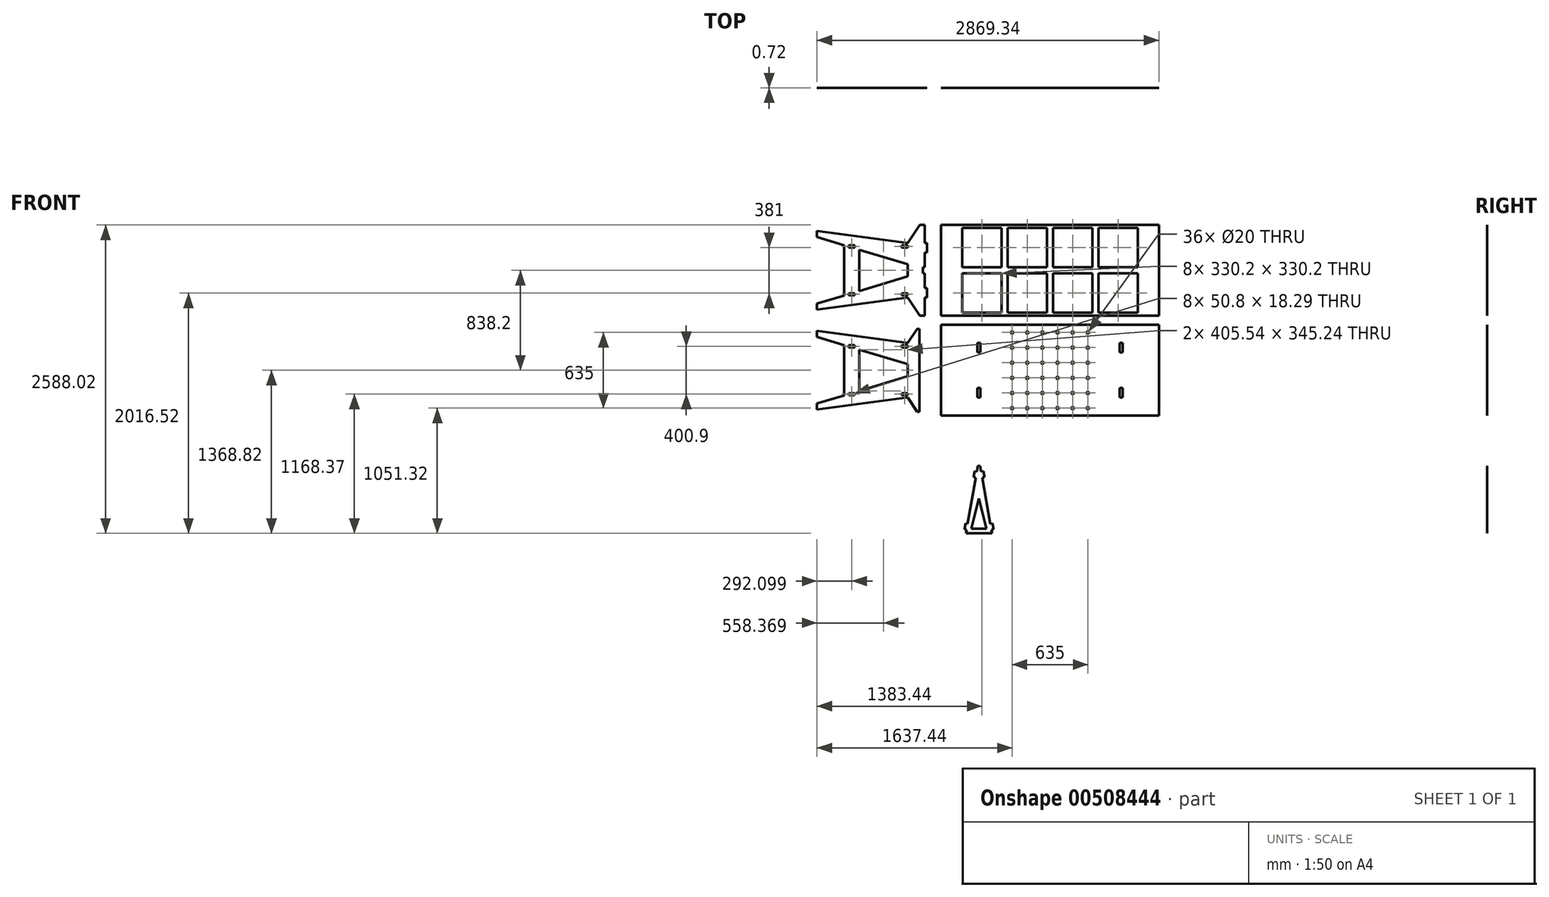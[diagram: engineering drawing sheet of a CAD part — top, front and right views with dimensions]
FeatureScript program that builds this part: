
annotation { "Feature Type Name" : "Feature", "Feature Type Description" : "" }
export const myFeature = defineFeature(function(context is Context, id is Id, definition is map)
    precondition{}
    {
        {
            assignVariable(context, id + "F0", {"name" : "ply34", "anyValue" : .72});
        }
        {
            var Q0;
            Q0=qCreatedBy(makeId("Front.planeOp"),FACE);
            var sketch = newSketch(context, id + "F1", { "sketchPlane" : qUnion([Q0])});
            skLineSegment(sketch, "E0.bottom", {"start": v(558.8, 1143) * mm, "end": v(2387.6, 1143) * mm});
            skLineSegment(sketch, "E0.top", {"start": v(558.8, 1905) * mm, "end": v(2387.6, 1905) * mm});
            skLineSegment(sketch, "E0.left", {"start": v(558.8, 1143) * mm, "end": v(558.8, 1905) * mm});
            skLineSegment(sketch, "E0.right", {"start": v(2387.6, 1143) * mm, "end": v(2387.6, 1905) * mm});
            skLineSegment(sketch, "E1.bottom", {"start": v(863.6, 1295.36) * mm, "end": v(888.66, 1295.36) * mm});
            skLineSegment(sketch, "E1.top", {"start": v(863.6, 1374.73) * mm, "end": v(888.66, 1374.73) * mm});
            skLineSegment(sketch, "E1.left", {"start": v(863.6, 1295.36) * mm, "end": v(863.6, 1374.73) * mm});
            skLineSegment(sketch, "E1.right", {"start": v(888.66, 1295.36) * mm, "end": v(888.66, 1374.73) * mm});
            skLineSegment(sketch, "E2", {"start": v(876.13, 1295.36) * mm, "end": v(876.13, 1143) * mm, "construction": true});
            skLineSegment(sketch, "E3", {"start": v(558.8, 1524) * mm, "end": v(2387.6, 1524) * mm, "construction": true});
            skLineSegment(sketch, "E4", {"start": v(2387.6, 1524) * mm, "end": v(1473.2, 1143) * mm, "construction": true});
            skLineSegment(sketch, "E5", {"start": v(1473.2, 1143) * mm, "end": v(1473.2, 1905) * mm, "construction": true});
            skLineSegment(sketch, "E6.MirrorCS", {"start": v(863.6, 1752.64) * mm, "end": v(863.6, 1673.27) * mm});
            skLineSegment(sketch, "E7.MirrorCS", {"start": v(863.6, 1673.27) * mm, "end": v(888.66, 1673.27) * mm});
            skLineSegment(sketch, "E8.MirrorCS", {"start": v(888.66, 1752.64) * mm, "end": v(888.66, 1673.27) * mm});
            skLineSegment(sketch, "E9.MirrorCS", {"start": v(863.6, 1752.64) * mm, "end": v(888.66, 1752.64) * mm});
            skLineSegment(sketch, "E10.MirrorCS", {"start": v(2082.8, 1752.64) * mm, "end": v(2082.8, 1673.27) * mm});
            skLineSegment(sketch, "E11.MirrorCS", {"start": v(2082.8, 1752.64) * mm, "end": v(2057.74, 1752.64) * mm});
            skLineSegment(sketch, "E12.MirrorCS", {"start": v(2057.74, 1752.64) * mm, "end": v(2057.74, 1673.27) * mm});
            skLineSegment(sketch, "E13.MirrorCS", {"start": v(2082.8, 1673.27) * mm, "end": v(2057.74, 1673.27) * mm});
            skLineSegment(sketch, "E14.MirrorCS", {"start": v(2082.8, 1295.36) * mm, "end": v(2082.8, 1374.73) * mm});
            skLineSegment(sketch, "E15.MirrorCS", {"start": v(2082.8, 1374.73) * mm, "end": v(2057.74, 1374.73) * mm});
            skLineSegment(sketch, "E16.MirrorCS", {"start": v(2057.74, 1295.36) * mm, "end": v(2057.74, 1374.73) * mm});
            skLineSegment(sketch, "E17.MirrorCS", {"start": v(2082.8, 1295.36) * mm, "end": v(2057.74, 1295.36) * mm});
            skCircle(sketch, "E18", {"center": v(1536.7, 1841.5) * mm, "radius": 10 * mm});
            skCircle(sketch, "E19.0.1.0", {"center": v(1536.7, 1714.5) * mm, "radius": 10 * mm});
            skCircle(sketch, "E19.0.2.0", {"center": v(1536.7, 1587.5) * mm, "radius": 10 * mm});
            skCircle(sketch, "E19.1.0.0", {"center": v(1663.7, 1841.5) * mm, "radius": 10 * mm});
            skCircle(sketch, "E19.1.1.0", {"center": v(1663.7, 1714.5) * mm, "radius": 10 * mm});
            skCircle(sketch, "E19.1.2.0", {"center": v(1663.7, 1587.5) * mm, "radius": 10 * mm});
            skCircle(sketch, "E19.2.0.0", {"center": v(1790.7, 1841.5) * mm, "radius": 10 * mm});
            skCircle(sketch, "E19.2.1.0", {"center": v(1790.7, 1714.5) * mm, "radius": 10 * mm});
            skCircle(sketch, "E19.2.2.0", {"center": v(1790.7, 1587.5) * mm, "radius": 10 * mm});
            skLineSegment(sketch, "E19.direction1", {"start": v(1536.7, 1841.5) * mm, "end": v(1663.7, 1841.5) * mm, "construction": true});
            skLineSegment(sketch, "E19.direction2", {"start": v(1536.7, 1841.5) * mm, "end": v(1536.7, 1714.5) * mm, "construction": true});
            skCircle(sketch, "E20.MirrorC", {"center": v(1409.7, 1841.5) * mm, "radius": 10 * mm});
            skCircle(sketch, "E21.MirrorC", {"center": v(1282.7, 1841.5) * mm, "radius": 10 * mm});
            skCircle(sketch, "E22.MirrorC", {"center": v(1155.7, 1841.5) * mm, "radius": 10 * mm});
            skCircle(sketch, "E23.MirrorC", {"center": v(1409.7, 1714.5) * mm, "radius": 10 * mm});
            skCircle(sketch, "E24.MirrorC", {"center": v(1282.7, 1714.5) * mm, "radius": 10 * mm});
            skCircle(sketch, "E25.MirrorC", {"center": v(1155.7, 1714.5) * mm, "radius": 10 * mm});
            skCircle(sketch, "E26.MirrorC", {"center": v(1409.7, 1587.5) * mm, "radius": 10 * mm});
            skCircle(sketch, "E27.MirrorC", {"center": v(1282.7, 1587.5) * mm, "radius": 10 * mm});
            skCircle(sketch, "E28.MirrorC", {"center": v(1155.7, 1587.5) * mm, "radius": 10 * mm});
            skCircle(sketch, "E29.MirrorC", {"center": v(1155.7, 1460.5) * mm, "radius": 10 * mm});
            skCircle(sketch, "E30.MirrorC", {"center": v(1409.7, 1206.5) * mm, "radius": 10 * mm});
            skCircle(sketch, "E31.MirrorC", {"center": v(1282.7, 1460.5) * mm, "radius": 10 * mm});
            skCircle(sketch, "E32.MirrorC", {"center": v(1155.7, 1333.5) * mm, "radius": 10 * mm});
            skCircle(sketch, "E33.MirrorC", {"center": v(1155.7, 1206.5) * mm, "radius": 10 * mm});
            skCircle(sketch, "E34.MirrorC", {"center": v(1282.7, 1206.5) * mm, "radius": 10 * mm});
            skCircle(sketch, "E35.MirrorC", {"center": v(1282.7, 1333.5) * mm, "radius": 10 * mm});
            skCircle(sketch, "E36.MirrorC", {"center": v(1409.7, 1333.5) * mm, "radius": 10 * mm});
            skCircle(sketch, "E37.MirrorC", {"center": v(1409.7, 1460.5) * mm, "radius": 10 * mm});
            skCircle(sketch, "E38.MirrorC", {"center": v(1663.7, 1460.5) * mm, "radius": 10 * mm});
            skCircle(sketch, "E39.MirrorC", {"center": v(1663.7, 1333.5) * mm, "radius": 10 * mm});
            skCircle(sketch, "E40.MirrorC", {"center": v(1536.7, 1206.5) * mm, "radius": 10 * mm});
            skCircle(sketch, "E41.MirrorC", {"center": v(1536.7, 1460.5) * mm, "radius": 10 * mm});
            skCircle(sketch, "E42.MirrorC", {"center": v(1790.7, 1206.5) * mm, "radius": 10 * mm});
            skCircle(sketch, "E43.MirrorC", {"center": v(1663.7, 1206.5) * mm, "radius": 10 * mm});
            skCircle(sketch, "E44.MirrorC", {"center": v(1790.7, 1460.5) * mm, "radius": 10 * mm});
            skCircle(sketch, "E45.MirrorC", {"center": v(1536.7, 1333.5) * mm, "radius": 10 * mm});
            skCircle(sketch, "E46.MirrorC", {"center": v(1790.7, 1333.5) * mm, "radius": 10 * mm});
            skLineSegment(sketch, "E47", {"start": v(558.8, 1943.1) * mm, "end": v(762, 1943.1) * mm});
            skLineSegment(sketch, "E48.MirrorCS", {"start": v(558.8, 1981.2) * mm, "end": v(2387.6, 1981.2) * mm});
            skLineSegment(sketch, "E49.MirrorCS", {"start": v(558.8, 2743.2) * mm, "end": v(558.8, 1981.2) * mm});
            skLineSegment(sketch, "E50.MirrorCS", {"start": v(2387.6, 2743.2) * mm, "end": v(2387.6, 1981.2) * mm});
            skLineSegment(sketch, "E51.MirrorCS", {"start": v(558.8, 2743.2) * mm, "end": v(2387.6, 2743.2) * mm});
            skLineSegment(sketch, "E52.MirrorCS", {"start": v(863.6, 2511.47) * mm, "end": v(888.66, 2511.47) * mm});
            skLineSegment(sketch, "E53.MirrorCS", {"start": v(888.66, 2590.84) * mm, "end": v(888.66, 2511.47) * mm});
            skLineSegment(sketch, "E54.MirrorCS", {"start": v(863.6, 2590.84) * mm, "end": v(863.6, 2511.47) * mm});
            skLineSegment(sketch, "E55.MirrorCS", {"start": v(863.6, 2590.84) * mm, "end": v(888.66, 2590.84) * mm});
            skLineSegment(sketch, "E56.MirrorCS", {"start": v(2082.8, 2590.84) * mm, "end": v(2082.8, 2511.47) * mm});
            skLineSegment(sketch, "E57.MirrorCS", {"start": v(2082.8, 2590.84) * mm, "end": v(2057.74, 2590.84) * mm});
            skLineSegment(sketch, "E58.MirrorCS", {"start": v(2057.74, 2590.84) * mm, "end": v(2057.74, 2511.47) * mm});
            skLineSegment(sketch, "E59.MirrorCS", {"start": v(2082.8, 2511.47) * mm, "end": v(2057.74, 2511.47) * mm});
            skLineSegment(sketch, "E60.MirrorCS", {"start": v(2082.8, 2212.93) * mm, "end": v(2057.74, 2212.93) * mm});
            skLineSegment(sketch, "E61.MirrorCS", {"start": v(2082.8, 2133.56) * mm, "end": v(2057.74, 2133.56) * mm});
            skLineSegment(sketch, "E62.MirrorCS", {"start": v(2057.74, 2133.56) * mm, "end": v(2057.74, 2212.93) * mm});
            skLineSegment(sketch, "E63.MirrorCS", {"start": v(2082.8, 2133.56) * mm, "end": v(2082.8, 2212.93) * mm});
            skLineSegment(sketch, "E64.MirrorCS", {"start": v(863.6, 2133.56) * mm, "end": v(888.66, 2133.56) * mm});
            skLineSegment(sketch, "E65.MirrorCS", {"start": v(863.6, 2212.93) * mm, "end": v(888.66, 2212.93) * mm});
            skLineSegment(sketch, "E66.MirrorCS", {"start": v(863.6, 2133.56) * mm, "end": v(863.6, 2212.93) * mm});
            skLineSegment(sketch, "E67.MirrorCS", {"start": v(888.66, 2133.56) * mm, "end": v(888.66, 2212.93) * mm});
            skCircle(sketch, "E68.MirrorC", {"center": v(1282.7, 2425.7) * mm, "radius": 10 * mm});
            skCircle(sketch, "E69.MirrorC", {"center": v(1155.7, 2425.7) * mm, "radius": 10 * mm});
            skCircle(sketch, "E70.MirrorC", {"center": v(1409.7, 2298.7) * mm, "radius": 10 * mm});
            skCircle(sketch, "E71.MirrorC", {"center": v(1282.7, 2171.7) * mm, "radius": 10 * mm});
            skCircle(sketch, "E72.MirrorC", {"center": v(1155.7, 2298.7) * mm, "radius": 10 * mm});
            skCircle(sketch, "E73.MirrorC", {"center": v(1282.7, 2044.7) * mm, "radius": 10 * mm});
            skCircle(sketch, "E74.MirrorC", {"center": v(1409.7, 2425.7) * mm, "radius": 10 * mm});
            skCircle(sketch, "E75.MirrorC", {"center": v(1409.7, 2044.7) * mm, "radius": 10 * mm});
            skCircle(sketch, "E76.MirrorC", {"center": v(1155.7, 2171.7) * mm, "radius": 10 * mm});
            skCircle(sketch, "E77.MirrorC", {"center": v(1282.7, 2679.7) * mm, "radius": 10 * mm});
            skCircle(sketch, "E78.MirrorC", {"center": v(1282.7, 2552.7) * mm, "radius": 10 * mm});
            skCircle(sketch, "E79.MirrorC", {"center": v(1409.7, 2679.7) * mm, "radius": 10 * mm});
            skCircle(sketch, "E80.MirrorC", {"center": v(1155.7, 2044.7) * mm, "radius": 10 * mm});
            skCircle(sketch, "E81.MirrorC", {"center": v(1155.7, 2552.7) * mm, "radius": 10 * mm});
            skCircle(sketch, "E82.MirrorC", {"center": v(1155.7, 2679.7) * mm, "radius": 10 * mm});
            skCircle(sketch, "E83.MirrorC", {"center": v(1409.7, 2552.7) * mm, "radius": 10 * mm});
            skCircle(sketch, "E84.MirrorC", {"center": v(1282.7, 2298.7) * mm, "radius": 10 * mm});
            skCircle(sketch, "E85.MirrorC", {"center": v(1409.7, 2171.7) * mm, "radius": 10 * mm});
            skCircle(sketch, "E86.MirrorC", {"center": v(1663.7, 2679.7) * mm, "radius": 10 * mm});
            skCircle(sketch, "E87.MirrorC", {"center": v(1790.7, 2298.7) * mm, "radius": 10 * mm});
            skCircle(sketch, "E88.MirrorC", {"center": v(1536.7, 2425.7) * mm, "radius": 10 * mm});
            skCircle(sketch, "E89.MirrorC", {"center": v(1663.7, 2298.7) * mm, "radius": 10 * mm});
            skCircle(sketch, "E90.MirrorC", {"center": v(1536.7, 2298.7) * mm, "radius": 10 * mm});
            skCircle(sketch, "E91.MirrorC", {"center": v(1663.7, 2425.7) * mm, "radius": 10 * mm});
            skCircle(sketch, "E92.MirrorC", {"center": v(1790.7, 2552.7) * mm, "radius": 10 * mm});
            skCircle(sketch, "E93.MirrorC", {"center": v(1663.7, 2552.7) * mm, "radius": 10 * mm});
            skCircle(sketch, "E94.MirrorC", {"center": v(1536.7, 2679.7) * mm, "radius": 10 * mm});
            skCircle(sketch, "E95.MirrorC", {"center": v(1536.7, 2552.7) * mm, "radius": 10 * mm});
            skCircle(sketch, "E96.MirrorC", {"center": v(1790.7, 2425.7) * mm, "radius": 10 * mm});
            skCircle(sketch, "E97.MirrorC", {"center": v(1790.7, 2679.7) * mm, "radius": 10 * mm});
            skCircle(sketch, "E98.MirrorC", {"center": v(1663.7, 2171.7) * mm, "radius": 10 * mm});
            skCircle(sketch, "E99.MirrorC", {"center": v(1790.7, 2171.7) * mm, "radius": 10 * mm});
            skCircle(sketch, "E100.MirrorC", {"center": v(1790.7, 2044.7) * mm, "radius": 10 * mm});
            skCircle(sketch, "E101.MirrorC", {"center": v(1663.7, 2044.7) * mm, "radius": 10 * mm});
            skCircle(sketch, "E102.MirrorC", {"center": v(1536.7, 2044.7) * mm, "radius": 10 * mm});
            skCircle(sketch, "E103.MirrorC", {"center": v(1536.7, 2171.7) * mm, "radius": 10 * mm});
            skPoint(sketch, "E104.positionSnap0", {"position": v(2387.6, 2362.2) * mm});
            skLineSegment(sketch, "E105", {"start": v(1536.7, 2552.7) * mm, "end": v(1663.7, 2552.7) * mm, "construction": true});
            skLineSegment(sketch, "E106", {"start": v(1663.7, 2425.7) * mm, "end": v(1663.7, 2552.7) * mm, "construction": true});
            skPoint(sketch, "E107.startSnap0", {"position": v(1600.2, 2552.7) * mm});
            skPoint(sketch, "E108.startSnap0", {"position": v(1663.7, 2489.2) * mm});
            skLineSegment(sketch, "E109", {"start": v(1473.2, 2743.2) * mm, "end": v(1473.2, 1981.2) * mm, "construction": true});
            skLineSegment(sketch, "E110", {"start": v(558.8, 2362.2) * mm, "end": v(2387.6, 2362.2) * mm, "construction": true});
            skLineSegment(sketch, "E111.bottom", {"start": v(1447.8, 2387.6) * mm, "end": v(1117.6, 2387.6) * mm});
            skLineSegment(sketch, "E111.top", {"start": v(1447.8, 2717.8) * mm, "end": v(1117.6, 2717.8) * mm});
            skLineSegment(sketch, "E111.left", {"start": v(1447.8, 2387.6) * mm, "end": v(1447.8, 2717.8) * mm});
            skLineSegment(sketch, "E111.right", {"start": v(1117.6, 2387.6) * mm, "end": v(1117.6, 2717.8) * mm});
            skLineSegment(sketch, "E112", {"start": v(1282.7, 2717.8) * mm, "end": v(1282.7, 2387.6) * mm, "construction": true});
            skLineSegment(sketch, "E113.MirrorCS", {"start": v(1498.6, 2387.6) * mm, "end": v(1498.6, 2717.8) * mm});
            skLineSegment(sketch, "E114.MirrorCS", {"start": v(1498.6, 2717.8) * mm, "end": v(1828.8, 2717.8) * mm});
            skLineSegment(sketch, "E115.MirrorCS", {"start": v(1828.8, 2387.6) * mm, "end": v(1828.8, 2717.8) * mm});
            skLineSegment(sketch, "E116.MirrorCS", {"start": v(1498.6, 2387.6) * mm, "end": v(1828.8, 2387.6) * mm});
            skLineSegment(sketch, "E117.MirrorCS", {"start": v(1663.7, 2717.8) * mm, "end": v(1663.7, 2387.6) * mm, "construction": true});
            skLineSegment(sketch, "E118.MirrorCS", {"start": v(1066.8, 2387.6) * mm, "end": v(1066.8, 2717.8) * mm});
            skLineSegment(sketch, "E119.MirrorCS", {"start": v(1066.8, 2717.8) * mm, "end": v(736.6, 2717.8) * mm});
            skLineSegment(sketch, "E120.MirrorCS", {"start": v(736.6, 2387.6) * mm, "end": v(736.6, 2717.8) * mm});
            skLineSegment(sketch, "E121.MirrorCS", {"start": v(1066.8, 2387.6) * mm, "end": v(736.6, 2387.6) * mm});
            skLineSegment(sketch, "E122.MirrorCS", {"start": v(1879.6, 2717.8) * mm, "end": v(2209.8, 2717.8) * mm});
            skLineSegment(sketch, "E123.MirrorCS", {"start": v(2209.8, 2387.6) * mm, "end": v(2209.8, 2717.8) * mm});
            skLineSegment(sketch, "E124.MirrorCS", {"start": v(1879.6, 2387.6) * mm, "end": v(2209.8, 2387.6) * mm});
            skLineSegment(sketch, "E125.MirrorCS", {"start": v(1879.6, 2387.6) * mm, "end": v(1879.6, 2717.8) * mm});
            skLineSegment(sketch, "E126.MirrorCS", {"start": v(1879.6, 2006.6) * mm, "end": v(2209.8, 2006.6) * mm});
            skLineSegment(sketch, "E127.MirrorCS", {"start": v(1498.6, 2006.6) * mm, "end": v(1828.8, 2006.6) * mm});
            skLineSegment(sketch, "E128.MirrorCS", {"start": v(1066.8, 2006.6) * mm, "end": v(736.6, 2006.6) * mm});
            skLineSegment(sketch, "E129.MirrorCS", {"start": v(1447.8, 2006.6) * mm, "end": v(1117.6, 2006.6) * mm});
            skLineSegment(sketch, "E130.MirrorCS", {"start": v(1066.8, 2336.8) * mm, "end": v(736.6, 2336.8) * mm});
            skLineSegment(sketch, "E131.MirrorCS", {"start": v(1879.6, 2336.8) * mm, "end": v(2209.8, 2336.8) * mm});
            skLineSegment(sketch, "E132.MirrorCS", {"start": v(1447.8, 2336.8) * mm, "end": v(1117.6, 2336.8) * mm});
            skLineSegment(sketch, "E133.MirrorCS", {"start": v(1498.6, 2336.8) * mm, "end": v(1828.8, 2336.8) * mm});
            skLineSegment(sketch, "E134.MirrorCS", {"start": v(2209.8, 2336.8) * mm, "end": v(2209.8, 2006.6) * mm});
            skLineSegment(sketch, "E135.MirrorCS", {"start": v(1828.8, 2336.8) * mm, "end": v(1828.8, 2006.6) * mm});
            skLineSegment(sketch, "E136.MirrorCS", {"start": v(1879.6, 2336.8) * mm, "end": v(1879.6, 2006.6) * mm});
            skLineSegment(sketch, "E137.MirrorCS", {"start": v(1498.6, 2336.8) * mm, "end": v(1498.6, 2006.6) * mm});
            skLineSegment(sketch, "E138.MirrorCS", {"start": v(1447.8, 2336.8) * mm, "end": v(1447.8, 2006.6) * mm});
            skLineSegment(sketch, "E139.MirrorCS", {"start": v(736.6, 2336.8) * mm, "end": v(736.6, 2006.6) * mm});
            skLineSegment(sketch, "E140.MirrorCS", {"start": v(1117.6, 2336.8) * mm, "end": v(1117.6, 2006.6) * mm});
            skLineSegment(sketch, "E141.MirrorCS", {"start": v(1066.8, 2336.8) * mm, "end": v(1066.8, 2006.6) * mm});
            skLineSegment(sketch, "E142.bottom", {"start": v(441.96, 2590.84) * mm, "end": v(406.4, 2590.84) * mm});
            skLineSegment(sketch, "E142.top", {"start": v(441.96, 2511.47) * mm, "end": v(406.4, 2511.47) * mm});
            skLineSegment(sketch, "E142.left", {"start": v(441.96, 2590.84) * mm, "end": v(441.96, 2511.47) * mm});
            skLineSegment(sketch, "E142.right", {"start": v(406.4, 2590.84) * mm, "end": v(406.4, 2511.47) * mm});
            skLineSegment(sketch, "E143.bottom", {"start": v(441.96, 2212.93) * mm, "end": v(406.4, 2212.93) * mm});
            skLineSegment(sketch, "E143.top", {"start": v(441.96, 2133.56) * mm, "end": v(406.4, 2133.56) * mm});
            skLineSegment(sketch, "E143.left", {"start": v(441.96, 2212.93) * mm, "end": v(441.96, 2133.56) * mm});
            skLineSegment(sketch, "E143.right", {"start": v(406.4, 2212.93) * mm, "end": v(406.4, 2133.56) * mm});
            skLineSegment(sketch, "E144", {"start": v(406.4, 2743.2) * mm, "end": v(406.4, 1981.2) * mm});
            skLineSegment(sketch, "E145", {"start": v(406.4, 1981.2) * mm, "end": v(381, 1981.2) * mm});
            skLineSegment(sketch, "E146", {"start": v(381, 1981.2) * mm, "end": v(279.4, 2133.56) * mm});
            skLineSegment(sketch, "E147", {"start": v(279.4, 2133.56) * mm, "end": v(-481.74, 2032) * mm});
            skLineSegment(sketch, "E148", {"start": v(558.8, 838.2) * mm, "end": v(2387.6, 838.2) * mm});
            skLineSegment(sketch, "E149", {"start": v(558.8, 838.2) * mm, "end": v(558.8, 801.62) * mm});
            skLineSegment(sketch, "E150", {"start": v(558.8, 801.62) * mm, "end": v(2387.6, 801.62) * mm});
            skLineSegment(sketch, "E151", {"start": v(2387.6, 801.62) * mm, "end": v(2387.6, 838.2) * mm});
            skLineSegment(sketch, "E152", {"start": v(863.6, 838.2) * mm, "end": v(863.6, 801.62) * mm});
            skLineSegment(sketch, "E153", {"start": v(888.66, 838.2) * mm, "end": v(888.66, 801.62) * mm});
            skLineSegment(sketch, "E154", {"start": v(863.6, 801.62) * mm, "end": v(869.77, 836.64) * mm});
            skLineSegment(sketch, "E155", {"start": v(869.77, 836.64) * mm, "end": v(887.79, 833.47) * mm});
            skLineSegment(sketch, "E156", {"start": v(887.79, 833.47) * mm, "end": v(727.39, -76.2) * mm});
            skLineSegment(sketch, "E157", {"start": v(441.96, 2362.2) * mm, "end": v(-481.74, 2362.2) * mm, "construction": true});
            skPoint(sketch, "E157.startSnap0", {"position": v(406.4, 2362.2) * mm});
            skPoint(sketch, "E157.endSnap0", {"position": v(406.4, 2362.2) * mm});
            skLineSegment(sketch, "E158", {"start": v(-481.74, 2032) * mm, "end": v(-481.74, 2082.8) * mm});
            skLineSegment(sketch, "E159", {"start": v(-481.74, 2082.8) * mm, "end": v(279.4, 2311.36) * mm, "construction": true});
            skLineSegment(sketch, "E160", {"start": v(-481.74, 2082.8) * mm, "end": v(-253.14, 2151.44) * mm});
            skLineSegment(sketch, "E161", {"start": v(-253.14, 2151.44) * mm, "end": v(-253.14, 2362.2) * mm});
            skLineSegment(sketch, "E162", {"start": v(-126.14, 2189.58) * mm, "end": v(-126.14, 2362.2) * mm});
            skLineSegment(sketch, "E163", {"start": v(279.4, 2311.36) * mm, "end": v(279.4, 2362.2) * mm});
            skLineSegment(sketch, "E164", {"start": v(-126.14, 2189.58) * mm, "end": v(279.4, 2311.36) * mm});
            skLineSegment(sketch, "E165.MirrorCS", {"start": v(-126.14, 2534.82) * mm, "end": v(-126.14, 2362.2) * mm});
            skLineSegment(sketch, "E166.MirrorCS", {"start": v(-253.14, 2572.96) * mm, "end": v(-253.14, 2362.2) * mm});
            skLineSegment(sketch, "E167.MirrorCS", {"start": v(-481.74, 2641.6) * mm, "end": v(-253.14, 2572.96) * mm});
            skLineSegment(sketch, "E168.MirrorCS", {"start": v(-481.74, 2692.4) * mm, "end": v(-481.74, 2641.6) * mm});
            skLineSegment(sketch, "E169.MirrorCS", {"start": v(279.4, 2413.04) * mm, "end": v(279.4, 2362.2) * mm});
            skLineSegment(sketch, "E170.MirrorCS", {"start": v(-126.14, 2534.82) * mm, "end": v(279.4, 2413.04) * mm});
            skLineSegment(sketch, "E171.MirrorCS", {"start": v(279.4, 2590.84) * mm, "end": v(-481.74, 2692.4) * mm});
            skLineSegment(sketch, "E172.MirrorCS", {"start": v(381, 2743.2) * mm, "end": v(279.4, 2590.84) * mm});
            skLineSegment(sketch, "E173.MirrorCS", {"start": v(406.4, 2743.2) * mm, "end": v(381, 2743.2) * mm});
            skLineSegment(sketch, "E174.bottom", {"start": v(279.4, 2170.9) * mm, "end": v(228.6, 2170.9) * mm});
            skLineSegment(sketch, "E174.top", {"start": v(279.4, 2152.6) * mm, "end": v(228.6, 2152.6) * mm});
            skLineSegment(sketch, "E174.left", {"start": v(279.4, 2170.9) * mm, "end": v(279.4, 2152.6) * mm});
            skLineSegment(sketch, "E174.right", {"start": v(228.6, 2170.9) * mm, "end": v(228.6, 2152.6) * mm});
            skLineSegment(sketch, "E175.bottom", {"start": v(-164.24, 2170.9) * mm, "end": v(-215.04, 2170.9) * mm});
            skLineSegment(sketch, "E175.top", {"start": v(-164.24, 2152.6) * mm, "end": v(-215.04, 2152.6) * mm});
            skLineSegment(sketch, "E175.left", {"start": v(-164.24, 2170.9) * mm, "end": v(-164.24, 2152.6) * mm});
            skLineSegment(sketch, "E175.right", {"start": v(-215.04, 2170.9) * mm, "end": v(-215.04, 2152.6) * mm});
            skLineSegment(sketch, "E176", {"start": v(-253.14, 2362.2) * mm, "end": v(-126.14, 2362.2) * mm, "construction": true});
            skPoint(sketch, "E177", {"position": v(-189.64, 2362.2) * mm});
            skPoint(sketch, "E178", {"position": v(-189.64, 2170.9) * mm});
            skLineSegment(sketch, "E179", {"start": v(279.4, 2161.75) * mm, "end": v(441.96, 2161.75) * mm, "construction": true});
            skLineSegment(sketch, "E180", {"start": v(-164.24, 2161.75) * mm, "end": v(441.96, 2161.75) * mm, "construction": true});
            skLineSegment(sketch, "E181", {"start": v(878.78, 835.06) * mm, "end": v(850.55, 674.97) * mm, "construction": true});
            skLineSegment(sketch, "E182", {"start": v(878.78, 835.06) * mm, "end": v(773.51, 238.06) * mm, "construction": true});
            skLineSegment(sketch, "E183", {"start": v(773.51, 238.06) * mm, "end": v(782.52, 236.48) * mm});
            skLineSegment(sketch, "E184", {"start": v(850.55, 674.97) * mm, "end": v(859.56, 673.38) * mm});
            skLineSegment(sketch, "E185", {"start": v(877.7, 776.22) * mm, "end": v(1028, -76.2) * mm});
            skLineSegment(sketch, "E186", {"start": v(877.7, 776.22) * mm, "end": v(895.7, 779.4) * mm});
            skLineSegment(sketch, "E187", {"start": v(782.52, 236.48) * mm, "end": v(764.5, 239.65) * mm});
            skLineSegment(sketch, "E188", {"start": v(764.5, 239.65) * mm, "end": v(755.69, 189.62) * mm});
            skLineSegment(sketch, "E189", {"start": v(755.69, 189.62) * mm, "end": v(773.7, 186.45) * mm});
            skLineSegment(sketch, "E190", {"start": v(859.56, 673.38) * mm, "end": v(841.55, 676.55) * mm});
            skLineSegment(sketch, "E191", {"start": v(841.55, 676.55) * mm, "end": v(832.73, 626.53) * mm});
            skLineSegment(sketch, "E192", {"start": v(832.73, 626.53) * mm, "end": v(850.74, 623.35) * mm});
            skLineSegment(sketch, "E193", {"start": v(868.17, 722.2) * mm, "end": v(887.22, 722.2) * mm});
            skLineSegment(sketch, "E194", {"start": v(877.7, 722.2) * mm, "end": v(877.7, 776.22) * mm, "construction": true});
            skLineSegment(sketch, "E195", {"start": v(768.18, 155.18) * mm, "end": v(987.2, 155.18) * mm});
            skLineSegment(sketch, "E196", {"start": v(814.2, 193.28) * mm, "end": v(941.2, 193.28) * mm});
            skPoint(sketch, "E197", {"position": v(877.7, 193.28) * mm});
            skLineSegment(sketch, "E198", {"start": v(814.2, 193.28) * mm, "end": v(877.7, 447.28) * mm});
            skLineSegment(sketch, "E199", {"start": v(877.7, 447.28) * mm, "end": v(941.2, 193.28) * mm});
            skLineSegment(sketch, "E200.MirrorCS", {"start": v(895.83, 673.38) * mm, "end": v(913.84, 676.55) * mm});
            skLineSegment(sketch, "E201.MirrorCS", {"start": v(913.84, 676.55) * mm, "end": v(922.66, 626.53) * mm});
            skLineSegment(sketch, "E202.MirrorCS", {"start": v(922.66, 626.53) * mm, "end": v(904.65, 623.35) * mm});
            skLineSegment(sketch, "E203.MirrorCS", {"start": v(999.7, 189.62) * mm, "end": v(981.68, 186.45) * mm});
            skLineSegment(sketch, "E204.MirrorCS", {"start": v(990.87, 239.65) * mm, "end": v(999.7, 189.62) * mm});
            skLineSegment(sketch, "E205.MirrorCS", {"start": v(972.86, 236.48) * mm, "end": v(990.87, 239.65) * mm});
            skLineSegment(sketch, "E206.MirrorCS", {"start": v(228.6, 2553.5) * mm, "end": v(228.6, 2571.8) * mm});
            skLineSegment(sketch, "E207.MirrorCS", {"start": v(279.4, 2553.5) * mm, "end": v(279.4, 2571.8) * mm});
            skLineSegment(sketch, "E208.MirrorCS", {"start": v(279.4, 2553.5) * mm, "end": v(228.6, 2553.5) * mm});
            skLineSegment(sketch, "E209.MirrorCS", {"start": v(279.4, 2571.8) * mm, "end": v(228.6, 2571.8) * mm});
            skPoint(sketch, "E210.MirrorP", {"position": v(-189.64, 2553.5) * mm});
            skLineSegment(sketch, "E211.MirrorCS", {"start": v(-164.24, 2571.8) * mm, "end": v(-215.04, 2571.8) * mm});
            skLineSegment(sketch, "E212.MirrorCS", {"start": v(-215.04, 2553.5) * mm, "end": v(-215.04, 2571.8) * mm});
            skLineSegment(sketch, "E213.MirrorCS", {"start": v(-164.24, 2553.5) * mm, "end": v(-215.04, 2553.5) * mm});
            skLineSegment(sketch, "E214.MirrorCS", {"start": v(-164.24, 2553.5) * mm, "end": v(-164.24, 2571.8) * mm});
            skLineSegment(sketch, "E215.MirrorCS", {"start": v(279.4, 1715.3) * mm, "end": v(279.4, 1733.6) * mm});
            skLineSegment(sketch, "E216.MirrorCS", {"start": v(279.4, 1332.7) * mm, "end": v(279.4, 1314.4) * mm});
            skLineSegment(sketch, "E217.MirrorCS", {"start": v(-164.24, 1715.3) * mm, "end": v(-215.04, 1715.3) * mm});
            skLineSegment(sketch, "E218.MirrorCS", {"start": v(-215.04, 1715.3) * mm, "end": v(-215.04, 1733.6) * mm});
            skLineSegment(sketch, "E219.MirrorCS", {"start": v(-164.24, 1733.6) * mm, "end": v(-215.04, 1733.6) * mm});
            skLineSegment(sketch, "E220.MirrorCS", {"start": v(-164.24, 1715.3) * mm, "end": v(-164.24, 1733.6) * mm});
            skLineSegment(sketch, "E221.MirrorCS", {"start": v(383.83, 1905) * mm, "end": v(381, 1905) * mm});
            skLineSegment(sketch, "E222.MirrorCS", {"start": v(228.6, 1332.7) * mm, "end": v(228.6, 1314.4) * mm});
            skLineSegment(sketch, "E223.MirrorCS", {"start": v(228.6, 1715.3) * mm, "end": v(228.6, 1733.6) * mm});
            skLineSegment(sketch, "E224.MirrorCS", {"start": v(279.4, 1332.7) * mm, "end": v(228.6, 1332.7) * mm});
            skLineSegment(sketch, "E225.MirrorCS", {"start": v(279.4, 1314.4) * mm, "end": v(228.6, 1314.4) * mm});
            skLineSegment(sketch, "E226.MirrorCS", {"start": v(-164.24, 1314.4) * mm, "end": v(-215.04, 1314.4) * mm});
            skLineSegment(sketch, "E227.MirrorCS", {"start": v(-481.74, 1193.8) * mm, "end": v(-481.74, 1244.6) * mm});
            skLineSegment(sketch, "E228.MirrorCS", {"start": v(-164.24, 1332.7) * mm, "end": v(-215.04, 1332.7) * mm});
            skLineSegment(sketch, "E229.MirrorCS", {"start": v(-215.04, 1332.7) * mm, "end": v(-215.04, 1314.4) * mm});
            skLineSegment(sketch, "E230.MirrorCS", {"start": v(279.4, 1473.16) * mm, "end": v(279.4, 1524) * mm});
            skLineSegment(sketch, "E231.MirrorCS", {"start": v(-164.24, 1332.7) * mm, "end": v(-164.24, 1314.4) * mm});
            skLineSegment(sketch, "E232.MirrorCS", {"start": v(383.83, 1143) * mm, "end": v(381, 1143) * mm});
            skLineSegment(sketch, "E233.MirrorCS", {"start": v(-481.74, 1854.2) * mm, "end": v(-481.74, 1803.4) * mm});
            skLineSegment(sketch, "E234.MirrorCS", {"start": v(279.4, 1715.3) * mm, "end": v(228.6, 1715.3) * mm});
            skLineSegment(sketch, "E235.MirrorCS", {"start": v(279.4, 1733.6) * mm, "end": v(228.6, 1733.6) * mm});
            skLineSegment(sketch, "E236.MirrorCS", {"start": v(279.4, 1574.84) * mm, "end": v(279.4, 1524) * mm});
            skLineSegment(sketch, "E237.MirrorCS", {"start": v(-481.74, 1803.4) * mm, "end": v(-253.14, 1734.76) * mm});
            skLineSegment(sketch, "E238.MirrorCS", {"start": v(-253.14, 1524) * mm, "end": v(-126.14, 1524) * mm, "construction": true});
            skLineSegment(sketch, "E239.MirrorCS", {"start": v(-126.14, 1696.62) * mm, "end": v(279.4, 1574.84) * mm});
            skLineSegment(sketch, "E240.MirrorCS", {"start": v(-126.14, 1351.38) * mm, "end": v(-126.14, 1524) * mm});
            skLineSegment(sketch, "E241.MirrorCS", {"start": v(-253.14, 1734.76) * mm, "end": v(-253.14, 1524) * mm});
            skLineSegment(sketch, "E242.MirrorCS", {"start": v(279.4, 1752.64) * mm, "end": v(-481.74, 1854.2) * mm});
            skLineSegment(sketch, "E243.MirrorCS", {"start": v(-253.14, 1313.24) * mm, "end": v(-253.14, 1524) * mm});
            skPoint(sketch, "E244.MirrorP", {"position": v(-189.64, 1715.3) * mm});
            skLineSegment(sketch, "E245.MirrorCS", {"start": v(-481.74, 1244.6) * mm, "end": v(-253.14, 1313.24) * mm});
            skPoint(sketch, "E246.MirrorP", {"position": v(-189.64, 1524) * mm});
            skPoint(sketch, "E247.MirrorP", {"position": v(-189.64, 1332.7) * mm});
            skLineSegment(sketch, "E248.MirrorCS", {"start": v(-126.14, 1351.38) * mm, "end": v(279.4, 1473.16) * mm});
            skLineSegment(sketch, "E249.MirrorCS", {"start": v(358.43, 1176.84) * mm, "end": v(279.4, 1295.36) * mm});
            skLineSegment(sketch, "E250.MirrorCS", {"start": v(-481.74, 1803.4) * mm, "end": v(279.4, 1574.84) * mm, "construction": true});
            skLineSegment(sketch, "E251.MirrorCS", {"start": v(-126.14, 1696.62) * mm, "end": v(-126.14, 1524) * mm});
            skLineSegment(sketch, "E252.MirrorCS", {"start": v(358.43, 1871.16) * mm, "end": v(279.4, 1752.64) * mm});
            skLineSegment(sketch, "E253.MirrorCS", {"start": v(279.4, 1295.36) * mm, "end": v(-481.74, 1193.8) * mm});
            skLineSegment(sketch, "E254", {"start": v(-481.74, 1524) * mm, "end": v(383.83, 1524) * mm, "construction": true});
            skLineSegment(sketch, "E255", {"start": v(383.83, 1176.84) * mm, "end": v(383.83, 1871.16) * mm});
            skPoint(sketch, "E256.orphan", {"position": v(406.4, 1143) * mm});
            skLineSegment(sketch, "E257", {"start": v(383.83, 1871.16) * mm, "end": v(358.43, 1871.16) * mm});
            skLineSegment(sketch, "E258", {"start": v(358.43, 1176.84) * mm, "end": v(383.83, 1176.84) * mm});
            skPoint(sketch, "E259.orphan", {"position": v(381, 1143) * mm});
            skLineSegment(sketch, "E260", {"start": v(406.4, 2743.2) * mm, "end": v(424.18, 2743.2) * mm});
            skPoint(sketch, "E260.endSnap0", {"position": v(424.18, 2590.84) * mm});
            skLineSegment(sketch, "E261", {"start": v(424.18, 2743.2) * mm, "end": v(424.18, 2590.84) * mm});
            skLineSegment(sketch, "E262", {"start": v(424.18, 2511.47) * mm, "end": v(424.18, 2212.93) * mm});
            skLineSegment(sketch, "E263", {"start": v(424.18, 2133.56) * mm, "end": v(424.18, 1981.2) * mm});
            skLineSegment(sketch, "E264", {"start": v(424.18, 1981.2) * mm, "end": v(406.4, 1981.2) * mm});
            skLineSegment(sketch, "E265.top", {"start": v(406.4, 2717.8) * mm, "end": v(424.18, 2717.8) * mm});
            skLineSegment(sketch, "E265.left", {"start": v(406.4, 2743.2) * mm, "end": v(406.4, 2717.8) * mm});
            skLineSegment(sketch, "E265.right", {"start": v(424.18, 2743.2) * mm, "end": v(424.18, 2717.8) * mm});
            skLineSegment(sketch, "E266.bottom", {"start": v(424.18, 2336.8) * mm, "end": v(406.4, 2336.8) * mm});
            skLineSegment(sketch, "E266.top", {"start": v(424.18, 2387.6) * mm, "end": v(406.4, 2387.6) * mm});
            skLineSegment(sketch, "E266.left", {"start": v(424.18, 2336.8) * mm, "end": v(424.18, 2387.6) * mm});
            skLineSegment(sketch, "E266.right", {"start": v(406.4, 2336.8) * mm, "end": v(406.4, 2387.6) * mm});
            skLineSegment(sketch, "E267.bottom", {"start": v(406.4, 2006.6) * mm, "end": v(424.18, 2006.6) * mm});
            skLineSegment(sketch, "E267.top", {"start": v(406.4, 1981.2) * mm, "end": v(424.18, 1981.2) * mm});
            skLineSegment(sketch, "E267.left", {"start": v(406.4, 2006.6) * mm, "end": v(406.4, 1981.2) * mm});
            skLineSegment(sketch, "E267.right", {"start": v(424.18, 2006.6) * mm, "end": v(424.18, 1981.2) * mm});
            skLineSegment(sketch, "E268.0", {"start": v(377.48, 1176.84) * mm, "end": v(377.48, 1871.16) * mm});
            skSolve(sketch);
        }
        {
            var Q0;
            {var subQ10=sQuery(id+"F1.wireOp",EDGE,"mAf3JBsy-TMgf-ZAlM-1Swj-JmzUZRKuhz1c");Q0=makeQuery(id+"F1.imprint","IMPRINT",FACE,{"disambiguationData":[TD([[makeQuery(id+"F1.imprint","IMPRINT",EDGE,{"derivedFrom":subQ10}),1.0]])]});}
            var Q1;
            {var subQ0=sQuery(id+"F1.wireOp",EDGE,"s7SXwr1m-1hA2-V0Zk-YU9T-9B9GOdkSBnw9");Q1=makeQuery(id+"F1.imprint","IMPRINT",FACE,{"disambiguationData":[TD([[makeQuery(id+"F1.imprint","IMPRINT",EDGE,{"derivedFrom":subQ0}),-1.0]])]});}
            var Q2;
            {var subQ0=sQuery(id+"F1.wireOp",EDGE,"N2ZZMMIE-rYt3-nwKZ-H1YN-OZv6ZI7qveUN");Q2=makeQuery(id+"F1.imprint","IMPRINT",FACE,{"disambiguationData":[TD([[makeQuery(id+"F1.imprint","IMPRINT",EDGE,{"derivedFrom":subQ0}),1.0]])]});}
            var Q3;
            {var subQ0=sQuery(id+"F1.wireOp",EDGE,"9ebe2d56-449b-47a5-8353-0fb5eb4cb9f70.MirrorCS");Q3=makeQuery(id+"F1.imprint","IMPRINT",FACE,{"disambiguationData":[TD([[makeQuery(id+"F1.imprint","IMPRINT",EDGE,{"derivedFrom":subQ0}),-1.0]])]});}
            var Q4;
            Q4=makeQuery(id+"F1.imprint","IMPRINT",FACE,{"disambiguationData":[TD([[makeQuery(id+"F1.imprint","IMPRINT",EDGE,{"derivedFrom":sQuery(id+"F1.wireOp",EDGE,"a0fd9d23-0f2f-4645-a1b7-4233243fae940.MirrorCS")}),1.0]])]});
            var Q5;
            {var subQ26=sQuery(id+"F1.wireOp",EDGE,"oeQHpsQD-rnvI-rLyI-L1zO-BZtazGxPJs8b");Q5=makeQuery(id+"F1.imprint","IMPRINT",FACE,{"disambiguationData":[TD([[makeQuery(id+"F1.imprint","IMPRINT",EDGE,{"derivedFrom":subQ26}),1.0]])]});}
            var Q6;
            Q6=makeQuery(id+"F1.imprint","IMPRINT",FACE,{"disambiguationData":[TD([[makeQuery(id+"F1.imprint","IMPRINT",EDGE,{"derivedFrom":sQuery(id+"F1.wireOp",EDGE,"E0.bottom")}),1.0]])]});
            var Q7;
            {var subQ0=sQuery(id+"F1.wireOp",EDGE,"xvaGzj0J-OEMp-EC2P-Z3wq-kDdIABfkp5yY");Q7=makeQuery(id+"F1.imprint","IMPRINT",FACE,{"disambiguationData":[TD([[makeQuery(id+"F1.imprint","IMPRINT",EDGE,{"derivedFrom":subQ0}),1.0]])]});}
            var Q8;
            Q8=makeQuery(id+"F1.imprint","IMPRINT",FACE,{"disambiguationData":[TD([[makeQuery(id+"F1.imprint","IMPRINT",EDGE,{"derivedFrom":sQuery(id+"F1.wireOp",EDGE,"AbsmaskG-t7lV-PoPT-sEhg-hebk6gVqelMg.bottom")}),1.0]])]});
            var Q9;
            Q9=makeQuery(id+"F1.imprint","IMPRINT",FACE,{"disambiguationData":[TD([[makeQuery(id+"F1.imprint","IMPRINT",EDGE,{"derivedFrom":sQuery(id+"F1.wireOp",EDGE,"Yeb76Brc-eH3c-p8nl-VyMf-ov4TZDuTgUcc.bottom")}),-1.0]])]});
            var Q10;
            {var subQ0=sQuery(id+"F1.wireOp",EDGE,"E51.MirrorCS");var subQ1=sQuery(id+"F1.wireOp",EDGE,"E49.MirrorCS");var subQ2=makeQuery(id+"F1.imprint","INTERSECT",VERTEX,{"derivedFrom":[subQ1,subQ0]});Q10=makeQuery(id+"F1.imprint","IMPRINT",FACE,{"disambiguationData":[TD([[makeQuery(id+"F1.imprint","IMPRINT",EDGE,{"disambiguationData":[TD([[subQ2,-1.0]])],"derivedFrom":subQ1}),1.0]])]});}
            var Q11;
            {var subQ0=sQuery(id+"F1.wireOp",EDGE,"RNtuIrKz-1knl-u3FS-AxBv-elPmaKCl8baw");var subQ1=sQuery(id+"F1.wireOp",EDGE,"E51.MirrorCS");var subQ2=makeQuery(id+"F1.imprint","INTERSECT",VERTEX,{"derivedFrom":[subQ1,subQ0]});Q11=makeQuery(id+"F1.imprint","IMPRINT",FACE,{"disambiguationData":[TD([[makeQuery(id+"F1.imprint","IMPRINT",EDGE,{"disambiguationData":[TD([[subQ2,1.0]])],"derivedFrom":subQ1}),-1.0]])]});}
            var Q12;
            {var subQ0=sQuery(id+"F1.wireOp",EDGE,"7UFrm05o-hojw-SgNx-ndEl-vP84DU8JNmmf");var subQ1=sQuery(id+"F1.wireOp",EDGE,"E51.MirrorCS");var subQ2=makeQuery(id+"F1.imprint","INTERSECT",VERTEX,{"derivedFrom":[subQ1,subQ0]});Q12=makeQuery(id+"F1.imprint","IMPRINT",FACE,{"disambiguationData":[TD([[makeQuery(id+"F1.imprint","IMPRINT",EDGE,{"disambiguationData":[TD([[subQ2,-1.0]])],"derivedFrom":subQ1}),-1.0]])]});}
            var Q13;
            {var subQ0=sQuery(id+"F1.wireOp",EDGE,"1122fb87-85ac-472b-868b-fc3012a12b32.1.0.0");var subQ1=sQuery(id+"F1.wireOp",EDGE,"E51.MirrorCS");var subQ2=makeQuery(id+"F1.imprint","INTERSECT",VERTEX,{"derivedFrom":[subQ1,subQ0]});Q13=makeQuery(id+"F1.imprint","IMPRINT",FACE,{"disambiguationData":[TD([[makeQuery(id+"F1.imprint","IMPRINT",EDGE,{"disambiguationData":[TD([[subQ2,1.0]])],"derivedFrom":subQ1}),-1.0]])]});}
            var Q14;
            {var subQ0=sQuery(id+"F1.wireOp",EDGE,"1122fb87-85ac-472b-868b-fc3012a12b32.1.0.0");var subQ1=sQuery(id+"F1.wireOp",EDGE,"E51.MirrorCS");var subQ2=makeQuery(id+"F1.imprint","INTERSECT",VERTEX,{"derivedFrom":[subQ1,subQ0]});Q14=makeQuery(id+"F1.imprint","IMPRINT",FACE,{"disambiguationData":[TD([[makeQuery(id+"F1.imprint","IMPRINT",EDGE,{"disambiguationData":[TD([[subQ2,-1.0]])],"derivedFrom":subQ1}),-1.0]])]});}
            var Q15;
            {var subQ0=sQuery(id+"F1.wireOp",EDGE,"1122fb87-85ac-472b-868b-fc3012a12b32.2.0.0");var subQ1=sQuery(id+"F1.wireOp",EDGE,"E51.MirrorCS");var subQ2=makeQuery(id+"F1.imprint","INTERSECT",VERTEX,{"derivedFrom":[subQ1,subQ0]});Q15=makeQuery(id+"F1.imprint","IMPRINT",FACE,{"disambiguationData":[TD([[makeQuery(id+"F1.imprint","IMPRINT",EDGE,{"disambiguationData":[TD([[subQ2,1.0]])],"derivedFrom":subQ1}),-1.0]])]});}
            var Q16;
            {var subQ0=sQuery(id+"F1.wireOp",EDGE,"RNtuIrKz-1knl-u3FS-AxBv-elPmaKCl8baw");var subQ1=sQuery(id+"F1.wireOp",EDGE,"E51.MirrorCS");var subQ2=makeQuery(id+"F1.imprint","INTERSECT",VERTEX,{"derivedFrom":[subQ1,subQ0]});Q16=makeQuery(id+"F1.imprint","IMPRINT",FACE,{"disambiguationData":[TD([[makeQuery(id+"F1.imprint","IMPRINT",EDGE,{"disambiguationData":[TD([[subQ2,-1.0]])],"derivedFrom":subQ1}),-1.0]])]});}
            var Q17;
            {var subQ0=sQuery(id+"F1.wireOp",EDGE,"1122fb87-85ac-472b-868b-fc3012a12b32.5.0.0");var subQ1=sQuery(id+"F1.wireOp",EDGE,"E51.MirrorCS");var subQ2=makeQuery(id+"F1.imprint","INTERSECT",VERTEX,{"derivedFrom":[subQ1,subQ0]});Q17=makeQuery(id+"F1.imprint","IMPRINT",FACE,{"disambiguationData":[TD([[makeQuery(id+"F1.imprint","IMPRINT",EDGE,{"disambiguationData":[TD([[subQ2,1.0]])],"derivedFrom":subQ1}),-1.0]])]});}
            var Q18;
            {var subQ0=sQuery(id+"F1.wireOp",EDGE,"1122fb87-85ac-472b-868b-fc3012a12b32.5.0.0");var subQ1=sQuery(id+"F1.wireOp",EDGE,"E51.MirrorCS");var subQ2=makeQuery(id+"F1.imprint","INTERSECT",VERTEX,{"derivedFrom":[subQ1,subQ0]});Q18=makeQuery(id+"F1.imprint","IMPRINT",FACE,{"disambiguationData":[TD([[makeQuery(id+"F1.imprint","IMPRINT",EDGE,{"disambiguationData":[TD([[subQ2,-1.0]])],"derivedFrom":subQ1}),-1.0]])]});}
            var Q19;
            {var subQ0=sQuery(id+"F1.wireOp",EDGE,"1122fb87-85ac-472b-868b-fc3012a12b32.6.0.0");var subQ1=sQuery(id+"F1.wireOp",EDGE,"E51.MirrorCS");var subQ2=makeQuery(id+"F1.imprint","INTERSECT",VERTEX,{"derivedFrom":[subQ1,subQ0]});Q19=makeQuery(id+"F1.imprint","IMPRINT",FACE,{"disambiguationData":[TD([[makeQuery(id+"F1.imprint","IMPRINT",EDGE,{"disambiguationData":[TD([[subQ2,-1.0]])],"derivedFrom":subQ1}),-1.0]])]});}
            var Q20;
            {var subQ0=sQuery(id+"F1.wireOp",EDGE,"1122fb87-85ac-472b-868b-fc3012a12b32.2.0.0");var subQ1=sQuery(id+"F1.wireOp",EDGE,"E51.MirrorCS");var subQ2=makeQuery(id+"F1.imprint","INTERSECT",VERTEX,{"derivedFrom":[subQ1,subQ0]});Q20=makeQuery(id+"F1.imprint","IMPRINT",FACE,{"disambiguationData":[TD([[makeQuery(id+"F1.imprint","IMPRINT",EDGE,{"disambiguationData":[TD([[subQ2,-1.0]])],"derivedFrom":subQ1}),-1.0]])]});}
            var Q21;
            {var subQ0=sQuery(id+"F1.wireOp",EDGE,"1122fb87-85ac-472b-868b-fc3012a12b32.3.0.0");var subQ1=sQuery(id+"F1.wireOp",EDGE,"E51.MirrorCS");var subQ2=makeQuery(id+"F1.imprint","INTERSECT",VERTEX,{"derivedFrom":[subQ1,subQ0]});Q21=makeQuery(id+"F1.imprint","IMPRINT",FACE,{"disambiguationData":[TD([[makeQuery(id+"F1.imprint","IMPRINT",EDGE,{"disambiguationData":[TD([[subQ2,-1.0]])],"derivedFrom":subQ1}),-1.0]])]});}
            var Q22;
            {var subQ0=sQuery(id+"F1.wireOp",EDGE,"1122fb87-85ac-472b-868b-fc3012a12b32.4.0.0");var subQ1=sQuery(id+"F1.wireOp",EDGE,"E51.MirrorCS");var subQ2=makeQuery(id+"F1.imprint","INTERSECT",VERTEX,{"derivedFrom":[subQ1,subQ0]});Q22=makeQuery(id+"F1.imprint","IMPRINT",FACE,{"disambiguationData":[TD([[makeQuery(id+"F1.imprint","IMPRINT",EDGE,{"disambiguationData":[TD([[subQ2,-1.0]])],"derivedFrom":subQ1}),-1.0]])]});}
            var Q23;
            {var subQ0=sQuery(id+"F1.wireOp",EDGE,"1122fb87-85ac-472b-868b-fc3012a12b32.8.0.0");var subQ1=sQuery(id+"F1.wireOp",EDGE,"E51.MirrorCS");var subQ2=makeQuery(id+"F1.imprint","INTERSECT",VERTEX,{"derivedFrom":[subQ1,subQ0]});Q23=makeQuery(id+"F1.imprint","IMPRINT",FACE,{"disambiguationData":[TD([[makeQuery(id+"F1.imprint","IMPRINT",EDGE,{"disambiguationData":[TD([[subQ2,-1.0]])],"derivedFrom":subQ1}),-1.0]])]});}
            var Q24;
            {var subQ0=sQuery(id+"F1.wireOp",EDGE,"1122fb87-85ac-472b-868b-fc3012a12b32.9.0.0");var subQ1=sQuery(id+"F1.wireOp",EDGE,"E51.MirrorCS");var subQ2=makeQuery(id+"F1.imprint","INTERSECT",VERTEX,{"derivedFrom":[subQ1,subQ0]});Q24=makeQuery(id+"F1.imprint","IMPRINT",FACE,{"disambiguationData":[TD([[makeQuery(id+"F1.imprint","IMPRINT",EDGE,{"disambiguationData":[TD([[subQ2,1.0]])],"derivedFrom":subQ1}),-1.0]])]});}
            var Q25;
            {var subQ0=sQuery(id+"F1.wireOp",EDGE,"1122fb87-85ac-472b-868b-fc3012a12b32.7.0.0");var subQ1=sQuery(id+"F1.wireOp",EDGE,"E51.MirrorCS");var subQ2=makeQuery(id+"F1.imprint","INTERSECT",VERTEX,{"derivedFrom":[subQ1,subQ0]});Q25=makeQuery(id+"F1.imprint","IMPRINT",FACE,{"disambiguationData":[TD([[makeQuery(id+"F1.imprint","IMPRINT",EDGE,{"disambiguationData":[TD([[subQ2,1.0]])],"derivedFrom":subQ1}),-1.0]])]});}
            var Q26;
            {var subQ0=sQuery(id+"F1.wireOp",EDGE,"1122fb87-85ac-472b-868b-fc3012a12b32.7.0.0");var subQ1=sQuery(id+"F1.wireOp",EDGE,"E51.MirrorCS");var subQ2=makeQuery(id+"F1.imprint","INTERSECT",VERTEX,{"derivedFrom":[subQ1,subQ0]});Q26=makeQuery(id+"F1.imprint","IMPRINT",FACE,{"disambiguationData":[TD([[makeQuery(id+"F1.imprint","IMPRINT",EDGE,{"disambiguationData":[TD([[subQ2,-1.0]])],"derivedFrom":subQ1}),-1.0]])]});}
            var Q27;
            {var subQ0=sQuery(id+"F1.wireOp",EDGE,"1122fb87-85ac-472b-868b-fc3012a12b32.8.0.0");var subQ1=sQuery(id+"F1.wireOp",EDGE,"E51.MirrorCS");var subQ2=makeQuery(id+"F1.imprint","INTERSECT",VERTEX,{"derivedFrom":[subQ1,subQ0]});Q27=makeQuery(id+"F1.imprint","IMPRINT",FACE,{"disambiguationData":[TD([[makeQuery(id+"F1.imprint","IMPRINT",EDGE,{"disambiguationData":[TD([[subQ2,1.0]])],"derivedFrom":subQ1}),-1.0]])]});}
            var Q28;
            {var subQ0=sQuery(id+"F1.wireOp",EDGE,"1122fb87-85ac-472b-868b-fc3012a12b32.10.0.0");var subQ1=sQuery(id+"F1.wireOp",EDGE,"E51.MirrorCS");var subQ2=makeQuery(id+"F1.imprint","INTERSECT",VERTEX,{"derivedFrom":[subQ1,subQ0]});Q28=makeQuery(id+"F1.imprint","IMPRINT",FACE,{"disambiguationData":[TD([[makeQuery(id+"F1.imprint","IMPRINT",EDGE,{"disambiguationData":[TD([[subQ2,-1.0]])],"derivedFrom":subQ1}),-1.0]])]});}
            var Q29;
            {var subQ0=sQuery(id+"F1.wireOp",EDGE,"1122fb87-85ac-472b-868b-fc3012a12b32.9.0.0");var subQ1=sQuery(id+"F1.wireOp",EDGE,"E51.MirrorCS");var subQ2=makeQuery(id+"F1.imprint","INTERSECT",VERTEX,{"derivedFrom":[subQ1,subQ0]});Q29=makeQuery(id+"F1.imprint","IMPRINT",FACE,{"disambiguationData":[TD([[makeQuery(id+"F1.imprint","IMPRINT",EDGE,{"disambiguationData":[TD([[subQ2,-1.0]])],"derivedFrom":subQ1}),-1.0]])]});}
            var Q30;
            {var subQ0=sQuery(id+"F1.wireOp",EDGE,"1122fb87-85ac-472b-868b-fc3012a12b32.10.0.0");var subQ1=sQuery(id+"F1.wireOp",EDGE,"E51.MirrorCS");var subQ2=makeQuery(id+"F1.imprint","INTERSECT",VERTEX,{"derivedFrom":[subQ1,subQ0]});Q30=makeQuery(id+"F1.imprint","IMPRINT",FACE,{"disambiguationData":[TD([[makeQuery(id+"F1.imprint","IMPRINT",EDGE,{"disambiguationData":[TD([[subQ2,1.0]])],"derivedFrom":subQ1}),-1.0]])]});}
            var Q31;
            {var subQ0=sQuery(id+"F1.wireOp",EDGE,"1122fb87-85ac-472b-868b-fc3012a12b32.6.0.0");var subQ1=sQuery(id+"F1.wireOp",EDGE,"E51.MirrorCS");var subQ2=makeQuery(id+"F1.imprint","INTERSECT",VERTEX,{"derivedFrom":[subQ1,subQ0]});Q31=makeQuery(id+"F1.imprint","IMPRINT",FACE,{"disambiguationData":[TD([[makeQuery(id+"F1.imprint","IMPRINT",EDGE,{"disambiguationData":[TD([[subQ2,1.0]])],"derivedFrom":subQ1}),-1.0]])]});}
            var Q32;
            {var subQ0=sQuery(id+"F1.wireOp",EDGE,"1122fb87-85ac-472b-868b-fc3012a12b32.4.0.0");var subQ1=sQuery(id+"F1.wireOp",EDGE,"E51.MirrorCS");var subQ2=makeQuery(id+"F1.imprint","INTERSECT",VERTEX,{"derivedFrom":[subQ1,subQ0]});Q32=makeQuery(id+"F1.imprint","IMPRINT",FACE,{"disambiguationData":[TD([[makeQuery(id+"F1.imprint","IMPRINT",EDGE,{"disambiguationData":[TD([[subQ2,1.0]])],"derivedFrom":subQ1}),-1.0]])]});}
            var Q33;
            {var subQ0=sQuery(id+"F1.wireOp",EDGE,"1122fb87-85ac-472b-868b-fc3012a12b32.3.0.0");var subQ1=sQuery(id+"F1.wireOp",EDGE,"E51.MirrorCS");var subQ2=makeQuery(id+"F1.imprint","INTERSECT",VERTEX,{"derivedFrom":[subQ1,subQ0]});Q33=makeQuery(id+"F1.imprint","IMPRINT",FACE,{"disambiguationData":[TD([[makeQuery(id+"F1.imprint","IMPRINT",EDGE,{"disambiguationData":[TD([[subQ2,1.0]])],"derivedFrom":subQ1}),-1.0]])]});}
            var Q34;
            {var subQ0=sQuery(id+"F1.wireOp",EDGE,"E51.MirrorCS");var subQ1=sQuery(id+"F1.wireOp",EDGE,"E50.MirrorCS");var subQ2=makeQuery(id+"F1.imprint","INTERSECT",VERTEX,{"derivedFrom":[subQ1,subQ0]});Q34=makeQuery(id+"F1.imprint","IMPRINT",FACE,{"disambiguationData":[TD([[makeQuery(id+"F1.imprint","IMPRINT",EDGE,{"disambiguationData":[TD([[subQ2,-1.0]])],"derivedFrom":subQ1}),-1.0]])]});}
            var Q35;
            {var subQ3=sQuery(id+"F1.wireOp",EDGE,"afe957d3-fdc2-43da-be9e-d4e8d3daa3b9.0");var subQ4=sQuery(id+"F1.wireOp",EDGE,"E50.MirrorCS");var subQ5=makeQuery(id+"F1.imprint","INTERSECT",VERTEX,{"derivedFrom":[subQ4,subQ3]});Q35=makeQuery(id+"F1.imprint","IMPRINT",FACE,{"disambiguationData":[TD([[makeQuery(id+"F1.imprint","IMPRINT",EDGE,{"disambiguationData":[TD([[subQ5,-1.0]])],"derivedFrom":subQ4}),-1.0]])]});}
            var Q36;
            {var subQ8=sQuery(id+"F1.wireOp",EDGE,"afe957d3-fdc2-43da-be9e-d4e8d3daa3b9.0");var subQ9=sQuery(id+"F1.wireOp",EDGE,"E49.MirrorCS");var subQ10=makeQuery(id+"F1.imprint","INTERSECT",VERTEX,{"derivedFrom":[subQ9,subQ8]});Q36=makeQuery(id+"F1.imprint","IMPRINT",FACE,{"disambiguationData":[TD([[makeQuery(id+"F1.imprint","IMPRINT",EDGE,{"disambiguationData":[TD([[subQ10,-1.0]])],"derivedFrom":subQ9}),1.0]])]});}
            var Q37;
            {var subQ0=sQuery(id+"F1.wireOp",EDGE,"E49.MirrorCS");var subQ1=sQuery(id+"F1.wireOp",EDGE,"E48.MirrorCS");var subQ2=makeQuery(id+"F1.imprint","INTERSECT",VERTEX,{"derivedFrom":[subQ1,subQ0]});Q37=makeQuery(id+"F1.imprint","IMPRINT",FACE,{"disambiguationData":[TD([[makeQuery(id+"F1.imprint","IMPRINT",EDGE,{"disambiguationData":[TD([[subQ2,-1.0]])],"derivedFrom":subQ1}),1.0]])]});}
            var Q38;
            {var subQ0=sQuery(id+"F1.wireOp",EDGE,"RNtuIrKz-1knl-u3FS-AxBv-elPmaKCl8baw");var subQ1=sQuery(id+"F1.wireOp",EDGE,"E48.MirrorCS");var subQ2=makeQuery(id+"F1.imprint","INTERSECT",VERTEX,{"derivedFrom":[subQ1,subQ0]});Q38=makeQuery(id+"F1.imprint","IMPRINT",FACE,{"disambiguationData":[TD([[makeQuery(id+"F1.imprint","IMPRINT",EDGE,{"disambiguationData":[TD([[subQ2,1.0]])],"derivedFrom":subQ1}),1.0]])]});}
            var Q39;
            {var subQ0=sQuery(id+"F1.wireOp",EDGE,"RNtuIrKz-1knl-u3FS-AxBv-elPmaKCl8baw");var subQ1=sQuery(id+"F1.wireOp",EDGE,"E48.MirrorCS");var subQ2=makeQuery(id+"F1.imprint","INTERSECT",VERTEX,{"derivedFrom":[subQ1,subQ0]});Q39=makeQuery(id+"F1.imprint","IMPRINT",FACE,{"disambiguationData":[TD([[makeQuery(id+"F1.imprint","IMPRINT",EDGE,{"disambiguationData":[TD([[subQ2,-1.0]])],"derivedFrom":subQ1}),1.0]])]});}
            var Q40;
            {var subQ0=sQuery(id+"F1.wireOp",EDGE,"1122fb87-85ac-472b-868b-fc3012a12b32.4.0.0");var subQ1=sQuery(id+"F1.wireOp",EDGE,"E48.MirrorCS");var subQ2=makeQuery(id+"F1.imprint","INTERSECT",VERTEX,{"derivedFrom":[subQ1,subQ0]});Q40=makeQuery(id+"F1.imprint","IMPRINT",FACE,{"disambiguationData":[TD([[makeQuery(id+"F1.imprint","IMPRINT",EDGE,{"disambiguationData":[TD([[subQ2,-1.0]])],"derivedFrom":subQ1}),1.0]])]});}
            var Q41;
            {var subQ0=sQuery(id+"F1.wireOp",EDGE,"E50.MirrorCS");var subQ1=sQuery(id+"F1.wireOp",EDGE,"E48.MirrorCS");var subQ2=makeQuery(id+"F1.imprint","INTERSECT",VERTEX,{"derivedFrom":[subQ1,subQ0]});Q41=makeQuery(id+"F1.imprint","IMPRINT",FACE,{"disambiguationData":[TD([[makeQuery(id+"F1.imprint","IMPRINT",EDGE,{"disambiguationData":[TD([[subQ2,1.0]])],"derivedFrom":subQ1}),1.0]])]});}
            var Q42;
            {var subQ0=sQuery(id+"F1.wireOp",EDGE,"1122fb87-85ac-472b-868b-fc3012a12b32.3.0.0");var subQ1=sQuery(id+"F1.wireOp",EDGE,"E48.MirrorCS");var subQ2=makeQuery(id+"F1.imprint","INTERSECT",VERTEX,{"derivedFrom":[subQ1,subQ0]});Q42=makeQuery(id+"F1.imprint","IMPRINT",FACE,{"disambiguationData":[TD([[makeQuery(id+"F1.imprint","IMPRINT",EDGE,{"disambiguationData":[TD([[subQ2,-1.0]])],"derivedFrom":subQ1}),1.0]])]});}
            var Q43;
            {var subQ0=sQuery(id+"F1.wireOp",EDGE,"1122fb87-85ac-472b-868b-fc3012a12b32.4.0.0");var subQ1=sQuery(id+"F1.wireOp",EDGE,"E48.MirrorCS");var subQ2=makeQuery(id+"F1.imprint","INTERSECT",VERTEX,{"derivedFrom":[subQ1,subQ0]});Q43=makeQuery(id+"F1.imprint","IMPRINT",FACE,{"disambiguationData":[TD([[makeQuery(id+"F1.imprint","IMPRINT",EDGE,{"disambiguationData":[TD([[subQ2,1.0]])],"derivedFrom":subQ1}),1.0]])]});}
            var Q44;
            {var subQ0=sQuery(id+"F1.wireOp",EDGE,"1122fb87-85ac-472b-868b-fc3012a12b32.5.0.0");var subQ1=sQuery(id+"F1.wireOp",EDGE,"E48.MirrorCS");var subQ2=makeQuery(id+"F1.imprint","INTERSECT",VERTEX,{"derivedFrom":[subQ1,subQ0]});Q44=makeQuery(id+"F1.imprint","IMPRINT",FACE,{"disambiguationData":[TD([[makeQuery(id+"F1.imprint","IMPRINT",EDGE,{"disambiguationData":[TD([[subQ2,-1.0]])],"derivedFrom":subQ1}),1.0]])]});}
            var Q45;
            {var subQ0=sQuery(id+"F1.wireOp",EDGE,"1122fb87-85ac-472b-868b-fc3012a12b32.5.0.0");var subQ1=sQuery(id+"F1.wireOp",EDGE,"E48.MirrorCS");var subQ2=makeQuery(id+"F1.imprint","INTERSECT",VERTEX,{"derivedFrom":[subQ1,subQ0]});Q45=makeQuery(id+"F1.imprint","IMPRINT",FACE,{"disambiguationData":[TD([[makeQuery(id+"F1.imprint","IMPRINT",EDGE,{"disambiguationData":[TD([[subQ2,1.0]])],"derivedFrom":subQ1}),1.0]])]});}
            var Q46;
            {var subQ0=sQuery(id+"F1.wireOp",EDGE,"1122fb87-85ac-472b-868b-fc3012a12b32.6.0.0");var subQ1=sQuery(id+"F1.wireOp",EDGE,"E48.MirrorCS");var subQ2=makeQuery(id+"F1.imprint","INTERSECT",VERTEX,{"derivedFrom":[subQ1,subQ0]});Q46=makeQuery(id+"F1.imprint","IMPRINT",FACE,{"disambiguationData":[TD([[makeQuery(id+"F1.imprint","IMPRINT",EDGE,{"disambiguationData":[TD([[subQ2,1.0]])],"derivedFrom":subQ1}),1.0]])]});}
            var Q47;
            {var subQ0=sQuery(id+"F1.wireOp",EDGE,"1122fb87-85ac-472b-868b-fc3012a12b32.6.0.0");var subQ1=sQuery(id+"F1.wireOp",EDGE,"E48.MirrorCS");var subQ2=makeQuery(id+"F1.imprint","INTERSECT",VERTEX,{"derivedFrom":[subQ1,subQ0]});Q47=makeQuery(id+"F1.imprint","IMPRINT",FACE,{"disambiguationData":[TD([[makeQuery(id+"F1.imprint","IMPRINT",EDGE,{"disambiguationData":[TD([[subQ2,-1.0]])],"derivedFrom":subQ1}),1.0]])]});}
            var Q48;
            {var subQ0=sQuery(id+"F1.wireOp",EDGE,"1122fb87-85ac-472b-868b-fc3012a12b32.7.0.0");var subQ1=sQuery(id+"F1.wireOp",EDGE,"E48.MirrorCS");var subQ2=makeQuery(id+"F1.imprint","INTERSECT",VERTEX,{"derivedFrom":[subQ1,subQ0]});Q48=makeQuery(id+"F1.imprint","IMPRINT",FACE,{"disambiguationData":[TD([[makeQuery(id+"F1.imprint","IMPRINT",EDGE,{"disambiguationData":[TD([[subQ2,1.0]])],"derivedFrom":subQ1}),1.0]])]});}
            var Q49;
            {var subQ0=sQuery(id+"F1.wireOp",EDGE,"1122fb87-85ac-472b-868b-fc3012a12b32.7.0.0");var subQ1=sQuery(id+"F1.wireOp",EDGE,"E48.MirrorCS");var subQ2=makeQuery(id+"F1.imprint","INTERSECT",VERTEX,{"derivedFrom":[subQ1,subQ0]});Q49=makeQuery(id+"F1.imprint","IMPRINT",FACE,{"disambiguationData":[TD([[makeQuery(id+"F1.imprint","IMPRINT",EDGE,{"disambiguationData":[TD([[subQ2,-1.0]])],"derivedFrom":subQ1}),1.0]])]});}
            var Q50;
            {var subQ0=sQuery(id+"F1.wireOp",EDGE,"1122fb87-85ac-472b-868b-fc3012a12b32.8.0.0");var subQ1=sQuery(id+"F1.wireOp",EDGE,"E48.MirrorCS");var subQ2=makeQuery(id+"F1.imprint","INTERSECT",VERTEX,{"derivedFrom":[subQ1,subQ0]});Q50=makeQuery(id+"F1.imprint","IMPRINT",FACE,{"disambiguationData":[TD([[makeQuery(id+"F1.imprint","IMPRINT",EDGE,{"disambiguationData":[TD([[subQ2,1.0]])],"derivedFrom":subQ1}),1.0]])]});}
            var Q51;
            {var subQ0=sQuery(id+"F1.wireOp",EDGE,"1122fb87-85ac-472b-868b-fc3012a12b32.8.0.0");var subQ1=sQuery(id+"F1.wireOp",EDGE,"E48.MirrorCS");var subQ2=makeQuery(id+"F1.imprint","INTERSECT",VERTEX,{"derivedFrom":[subQ1,subQ0]});Q51=makeQuery(id+"F1.imprint","IMPRINT",FACE,{"disambiguationData":[TD([[makeQuery(id+"F1.imprint","IMPRINT",EDGE,{"disambiguationData":[TD([[subQ2,-1.0]])],"derivedFrom":subQ1}),1.0]])]});}
            var Q52;
            {var subQ0=sQuery(id+"F1.wireOp",EDGE,"1122fb87-85ac-472b-868b-fc3012a12b32.9.0.0");var subQ1=sQuery(id+"F1.wireOp",EDGE,"E48.MirrorCS");var subQ2=makeQuery(id+"F1.imprint","INTERSECT",VERTEX,{"derivedFrom":[subQ1,subQ0]});Q52=makeQuery(id+"F1.imprint","IMPRINT",FACE,{"disambiguationData":[TD([[makeQuery(id+"F1.imprint","IMPRINT",EDGE,{"disambiguationData":[TD([[subQ2,1.0]])],"derivedFrom":subQ1}),1.0]])]});}
            var Q53;
            {var subQ0=sQuery(id+"F1.wireOp",EDGE,"1122fb87-85ac-472b-868b-fc3012a12b32.1.0.0");var subQ1=sQuery(id+"F1.wireOp",EDGE,"E48.MirrorCS");var subQ2=makeQuery(id+"F1.imprint","INTERSECT",VERTEX,{"derivedFrom":[subQ1,subQ0]});Q53=makeQuery(id+"F1.imprint","IMPRINT",FACE,{"disambiguationData":[TD([[makeQuery(id+"F1.imprint","IMPRINT",EDGE,{"disambiguationData":[TD([[subQ2,1.0]])],"derivedFrom":subQ1}),1.0]])]});}
            var Q54;
            {var subQ0=sQuery(id+"F1.wireOp",EDGE,"1122fb87-85ac-472b-868b-fc3012a12b32.9.0.0");var subQ1=sQuery(id+"F1.wireOp",EDGE,"E48.MirrorCS");var subQ2=makeQuery(id+"F1.imprint","INTERSECT",VERTEX,{"derivedFrom":[subQ1,subQ0]});Q54=makeQuery(id+"F1.imprint","IMPRINT",FACE,{"disambiguationData":[TD([[makeQuery(id+"F1.imprint","IMPRINT",EDGE,{"disambiguationData":[TD([[subQ2,-1.0]])],"derivedFrom":subQ1}),1.0]])]});}
            var Q55;
            {var subQ0=sQuery(id+"F1.wireOp",EDGE,"1122fb87-85ac-472b-868b-fc3012a12b32.1.0.0");var subQ1=sQuery(id+"F1.wireOp",EDGE,"E48.MirrorCS");var subQ2=makeQuery(id+"F1.imprint","INTERSECT",VERTEX,{"derivedFrom":[subQ1,subQ0]});Q55=makeQuery(id+"F1.imprint","IMPRINT",FACE,{"disambiguationData":[TD([[makeQuery(id+"F1.imprint","IMPRINT",EDGE,{"disambiguationData":[TD([[subQ2,-1.0]])],"derivedFrom":subQ1}),1.0]])]});}
            var Q56;
            {var subQ0=sQuery(id+"F1.wireOp",EDGE,"1122fb87-85ac-472b-868b-fc3012a12b32.10.0.0");var subQ1=sQuery(id+"F1.wireOp",EDGE,"E48.MirrorCS");var subQ2=makeQuery(id+"F1.imprint","INTERSECT",VERTEX,{"derivedFrom":[subQ1,subQ0]});Q56=makeQuery(id+"F1.imprint","IMPRINT",FACE,{"disambiguationData":[TD([[makeQuery(id+"F1.imprint","IMPRINT",EDGE,{"disambiguationData":[TD([[subQ2,1.0]])],"derivedFrom":subQ1}),1.0]])]});}
            var Q57;
            {var subQ0=sQuery(id+"F1.wireOp",EDGE,"1122fb87-85ac-472b-868b-fc3012a12b32.2.0.0");var subQ1=sQuery(id+"F1.wireOp",EDGE,"E48.MirrorCS");var subQ2=makeQuery(id+"F1.imprint","INTERSECT",VERTEX,{"derivedFrom":[subQ1,subQ0]});Q57=makeQuery(id+"F1.imprint","IMPRINT",FACE,{"disambiguationData":[TD([[makeQuery(id+"F1.imprint","IMPRINT",EDGE,{"disambiguationData":[TD([[subQ2,1.0]])],"derivedFrom":subQ1}),1.0]])]});}
            var Q58;
            {var subQ0=sQuery(id+"F1.wireOp",EDGE,"1122fb87-85ac-472b-868b-fc3012a12b32.10.0.0");var subQ1=sQuery(id+"F1.wireOp",EDGE,"E48.MirrorCS");var subQ2=makeQuery(id+"F1.imprint","INTERSECT",VERTEX,{"derivedFrom":[subQ1,subQ0]});Q58=makeQuery(id+"F1.imprint","IMPRINT",FACE,{"disambiguationData":[TD([[makeQuery(id+"F1.imprint","IMPRINT",EDGE,{"disambiguationData":[TD([[subQ2,-1.0]])],"derivedFrom":subQ1}),1.0]])]});}
            var Q59;
            {var subQ0=sQuery(id+"F1.wireOp",EDGE,"1122fb87-85ac-472b-868b-fc3012a12b32.2.0.0");var subQ1=sQuery(id+"F1.wireOp",EDGE,"E48.MirrorCS");var subQ2=makeQuery(id+"F1.imprint","INTERSECT",VERTEX,{"derivedFrom":[subQ1,subQ0]});Q59=makeQuery(id+"F1.imprint","IMPRINT",FACE,{"disambiguationData":[TD([[makeQuery(id+"F1.imprint","IMPRINT",EDGE,{"disambiguationData":[TD([[subQ2,-1.0]])],"derivedFrom":subQ1}),1.0]])]});}
            var Q60;
            {var subQ0=sQuery(id+"F1.wireOp",EDGE,"1122fb87-85ac-472b-868b-fc3012a12b32.3.0.0");var subQ1=sQuery(id+"F1.wireOp",EDGE,"E48.MirrorCS");var subQ2=makeQuery(id+"F1.imprint","INTERSECT",VERTEX,{"derivedFrom":[subQ1,subQ0]});Q60=makeQuery(id+"F1.imprint","IMPRINT",FACE,{"disambiguationData":[TD([[makeQuery(id+"F1.imprint","IMPRINT",EDGE,{"disambiguationData":[TD([[subQ2,1.0]])],"derivedFrom":subQ1}),1.0]])]});}
            var Q61;
            {var subQ0=sQuery(id+"F1.wireOp",EDGE,"7UFrm05o-hojw-SgNx-ndEl-vP84DU8JNmmf");var subQ1=sQuery(id+"F1.wireOp",EDGE,"E48.MirrorCS");var subQ2=makeQuery(id+"F1.imprint","INTERSECT",VERTEX,{"derivedFrom":[subQ1,subQ0]});Q61=makeQuery(id+"F1.imprint","IMPRINT",FACE,{"disambiguationData":[TD([[makeQuery(id+"F1.imprint","IMPRINT",EDGE,{"disambiguationData":[TD([[subQ2,-1.0]])],"derivedFrom":subQ1}),1.0]])]});}
            var Q62;
            {var subQ0=sQuery(id+"F1.wireOp",EDGE,"RNtuIrKz-1knl-u3FS-AxBv-elPmaKCl8baw");var subQ1=sQuery(id+"F1.wireOp",EDGE,"a13d30e3-1256-45f2-88c4-17f94fdc27e3.0.4.0");var subQ2=makeQuery(id+"F1.imprint","INTERSECT",VERTEX,{"derivedFrom":[subQ1,subQ0]});Q62=makeQuery(id+"F1.imprint","IMPRINT",FACE,{"disambiguationData":[TD([[makeQuery(id+"F1.imprint","IMPRINT",EDGE,{"disambiguationData":[TD([[subQ2,-1.0]])],"derivedFrom":subQ1}),-1.0]])]});}
            var Q63;
            {var subQ0=sQuery(id+"F1.wireOp",EDGE,"RNtuIrKz-1knl-u3FS-AxBv-elPmaKCl8baw");var subQ1=sQuery(id+"F1.wireOp",EDGE,"a13d30e3-1256-45f2-88c4-17f94fdc27e3.0.3.1");var subQ2=makeQuery(id+"F1.imprint","INTERSECT",VERTEX,{"derivedFrom":[subQ1,subQ0]});Q63=makeQuery(id+"F1.imprint","IMPRINT",FACE,{"disambiguationData":[TD([[makeQuery(id+"F1.imprint","IMPRINT",EDGE,{"disambiguationData":[TD([[subQ2,-1.0]])],"derivedFrom":subQ1}),-1.0]])]});}
            var Q64;
            {var subQ0=sQuery(id+"F1.wireOp",EDGE,"RNtuIrKz-1knl-u3FS-AxBv-elPmaKCl8baw");var subQ1=sQuery(id+"F1.wireOp",EDGE,"a13d30e3-1256-45f2-88c4-17f94fdc27e3.0.1.1");var subQ2=makeQuery(id+"F1.imprint","INTERSECT",VERTEX,{"derivedFrom":[subQ1,subQ0]});Q64=makeQuery(id+"F1.imprint","IMPRINT",FACE,{"disambiguationData":[TD([[makeQuery(id+"F1.imprint","IMPRINT",EDGE,{"disambiguationData":[TD([[subQ2,-1.0]])],"derivedFrom":subQ1}),-1.0]])]});}
            var Q65;
            {var subQ0=sQuery(id+"F1.wireOp",EDGE,"RNtuIrKz-1knl-u3FS-AxBv-elPmaKCl8baw");var subQ1=sQuery(id+"F1.wireOp",EDGE,"a13d30e3-1256-45f2-88c4-17f94fdc27e3.0.2.0");var subQ2=makeQuery(id+"F1.imprint","INTERSECT",VERTEX,{"derivedFrom":[subQ1,subQ0]});Q65=makeQuery(id+"F1.imprint","IMPRINT",FACE,{"disambiguationData":[TD([[makeQuery(id+"F1.imprint","IMPRINT",EDGE,{"disambiguationData":[TD([[subQ2,-1.0]])],"derivedFrom":subQ1}),-1.0]])]});}
            var Q66;
            {var subQ0=sQuery(id+"F1.wireOp",EDGE,"RNtuIrKz-1knl-u3FS-AxBv-elPmaKCl8baw");var subQ1=sQuery(id+"F1.wireOp",EDGE,"6uq4eEBE-zqJi-hSKM-aljM-bMrpigbcLfnv");var subQ2=makeQuery(id+"F1.imprint","INTERSECT",VERTEX,{"derivedFrom":[subQ1,subQ0]});Q66=makeQuery(id+"F1.imprint","IMPRINT",FACE,{"disambiguationData":[TD([[makeQuery(id+"F1.imprint","IMPRINT",EDGE,{"disambiguationData":[TD([[subQ2,-1.0]])],"derivedFrom":subQ1}),-1.0]])]});}
            var Q67;
            {var subQ0=sQuery(id+"F1.wireOp",EDGE,"RNtuIrKz-1knl-u3FS-AxBv-elPmaKCl8baw");var subQ1=sQuery(id+"F1.wireOp",EDGE,"6uq4eEBE-zqJi-hSKM-aljM-bMrpigbcLfnv");var subQ2=makeQuery(id+"F1.imprint","INTERSECT",VERTEX,{"derivedFrom":[subQ1,subQ0]});Q67=makeQuery(id+"F1.imprint","IMPRINT",FACE,{"disambiguationData":[TD([[makeQuery(id+"F1.imprint","IMPRINT",EDGE,{"disambiguationData":[TD([[subQ2,-1.0]])],"derivedFrom":subQ1}),1.0]])]});}
            var Q68;
            {var subQ0=sQuery(id+"F1.wireOp",EDGE,"RNtuIrKz-1knl-u3FS-AxBv-elPmaKCl8baw");var subQ1=sQuery(id+"F1.wireOp",EDGE,"a13d30e3-1256-45f2-88c4-17f94fdc27e3.0.4.1");var subQ2=makeQuery(id+"F1.imprint","INTERSECT",VERTEX,{"derivedFrom":[subQ1,subQ0]});Q68=makeQuery(id+"F1.imprint","IMPRINT",FACE,{"disambiguationData":[TD([[makeQuery(id+"F1.imprint","IMPRINT",EDGE,{"disambiguationData":[TD([[subQ2,-1.0]])],"derivedFrom":subQ1}),-1.0]])]});}
            var Q69;
            {var subQ0=sQuery(id+"F1.wireOp",EDGE,"RNtuIrKz-1knl-u3FS-AxBv-elPmaKCl8baw");var subQ1=sQuery(id+"F1.wireOp",EDGE,"a13d30e3-1256-45f2-88c4-17f94fdc27e3.0.2.1");var subQ2=makeQuery(id+"F1.imprint","INTERSECT",VERTEX,{"derivedFrom":[subQ1,subQ0]});Q69=makeQuery(id+"F1.imprint","IMPRINT",FACE,{"disambiguationData":[TD([[makeQuery(id+"F1.imprint","IMPRINT",EDGE,{"disambiguationData":[TD([[subQ2,-1.0]])],"derivedFrom":subQ1}),-1.0]])]});}
            var Q70;
            {var subQ0=sQuery(id+"F1.wireOp",EDGE,"RNtuIrKz-1knl-u3FS-AxBv-elPmaKCl8baw");var subQ1=sQuery(id+"F1.wireOp",EDGE,"a13d30e3-1256-45f2-88c4-17f94fdc27e3.0.1.0");var subQ2=makeQuery(id+"F1.imprint","INTERSECT",VERTEX,{"derivedFrom":[subQ1,subQ0]});Q70=makeQuery(id+"F1.imprint","IMPRINT",FACE,{"disambiguationData":[TD([[makeQuery(id+"F1.imprint","IMPRINT",EDGE,{"disambiguationData":[TD([[subQ2,-1.0]])],"derivedFrom":subQ1}),-1.0]])]});}
            var Q71;
            {var subQ0=sQuery(id+"F1.wireOp",EDGE,"RNtuIrKz-1knl-u3FS-AxBv-elPmaKCl8baw");var subQ1=sQuery(id+"F1.wireOp",EDGE,"a13d30e3-1256-45f2-88c4-17f94fdc27e3.0.3.0");var subQ2=makeQuery(id+"F1.imprint","INTERSECT",VERTEX,{"derivedFrom":[subQ1,subQ0]});Q71=makeQuery(id+"F1.imprint","IMPRINT",FACE,{"disambiguationData":[TD([[makeQuery(id+"F1.imprint","IMPRINT",EDGE,{"disambiguationData":[TD([[subQ2,-1.0]])],"derivedFrom":subQ1}),-1.0]])]});}
            var Q72;
            {var subQ0=sQuery(id+"F1.wireOp",EDGE,"RNtuIrKz-1knl-u3FS-AxBv-elPmaKCl8baw");var subQ1=sQuery(id+"F1.wireOp",EDGE,"IqfzKEuX-Kduy-EBgq-JfLB-lxs091du6jRf");var subQ2=makeQuery(id+"F1.imprint","INTERSECT",VERTEX,{"derivedFrom":[subQ1,subQ0]});Q72=makeQuery(id+"F1.imprint","IMPRINT",FACE,{"disambiguationData":[TD([[makeQuery(id+"F1.imprint","IMPRINT",EDGE,{"disambiguationData":[TD([[subQ2,-1.0]])],"derivedFrom":subQ1}),-1.0]])]});}
            var Q73;
            {var subQ0=sQuery(id+"F1.wireOp",EDGE,"1122fb87-85ac-472b-868b-fc3012a12b32.1.0.1");var subQ1=sQuery(id+"F1.wireOp",EDGE,"a13d30e3-1256-45f2-88c4-17f94fdc27e3.0.1.0");var subQ2=makeQuery(id+"F1.imprint","INTERSECT",VERTEX,{"derivedFrom":[subQ1,subQ0]});Q73=makeQuery(id+"F1.imprint","IMPRINT",FACE,{"disambiguationData":[TD([[makeQuery(id+"F1.imprint","IMPRINT",EDGE,{"disambiguationData":[TD([[subQ2,-1.0]])],"derivedFrom":subQ1}),-1.0]])]});}
            var Q74;
            {var subQ0=sQuery(id+"F1.wireOp",EDGE,"1122fb87-85ac-472b-868b-fc3012a12b32.2.0.1");var subQ1=sQuery(id+"F1.wireOp",EDGE,"IqfzKEuX-Kduy-EBgq-JfLB-lxs091du6jRf");var subQ2=makeQuery(id+"F1.imprint","INTERSECT",VERTEX,{"derivedFrom":[subQ1,subQ0]});Q74=makeQuery(id+"F1.imprint","IMPRINT",FACE,{"disambiguationData":[TD([[makeQuery(id+"F1.imprint","IMPRINT",EDGE,{"disambiguationData":[TD([[subQ2,-1.0]])],"derivedFrom":subQ1}),-1.0]])]});}
            var Q75;
            {var subQ0=sQuery(id+"F1.wireOp",EDGE,"1122fb87-85ac-472b-868b-fc3012a12b32.1.0.0");var subQ1=sQuery(id+"F1.wireOp",EDGE,"a13d30e3-1256-45f2-88c4-17f94fdc27e3.0.3.0");var subQ2=makeQuery(id+"F1.imprint","INTERSECT",VERTEX,{"derivedFrom":[subQ1,subQ0]});Q75=makeQuery(id+"F1.imprint","IMPRINT",FACE,{"disambiguationData":[TD([[makeQuery(id+"F1.imprint","IMPRINT",EDGE,{"disambiguationData":[TD([[subQ2,-1.0]])],"derivedFrom":subQ1}),-1.0]])]});}
            var Q76;
            {var subQ0=sQuery(id+"F1.wireOp",EDGE,"1122fb87-85ac-472b-868b-fc3012a12b32.2.0.1");var subQ1=sQuery(id+"F1.wireOp",EDGE,"a13d30e3-1256-45f2-88c4-17f94fdc27e3.0.2.1");var subQ2=makeQuery(id+"F1.imprint","INTERSECT",VERTEX,{"derivedFrom":[subQ1,subQ0]});Q76=makeQuery(id+"F1.imprint","IMPRINT",FACE,{"disambiguationData":[TD([[makeQuery(id+"F1.imprint","IMPRINT",EDGE,{"disambiguationData":[TD([[subQ2,-1.0]])],"derivedFrom":subQ1}),-1.0]])]});}
            var Q77;
            {var subQ0=sQuery(id+"F1.wireOp",EDGE,"1122fb87-85ac-472b-868b-fc3012a12b32.1.0.1");var subQ1=sQuery(id+"F1.wireOp",EDGE,"a13d30e3-1256-45f2-88c4-17f94fdc27e3.0.3.0");var subQ2=makeQuery(id+"F1.imprint","INTERSECT",VERTEX,{"derivedFrom":[subQ1,subQ0]});Q77=makeQuery(id+"F1.imprint","IMPRINT",FACE,{"disambiguationData":[TD([[makeQuery(id+"F1.imprint","IMPRINT",EDGE,{"disambiguationData":[TD([[subQ2,-1.0]])],"derivedFrom":subQ1}),-1.0]])]});}
            var Q78;
            {var subQ0=sQuery(id+"F1.wireOp",EDGE,"1122fb87-85ac-472b-868b-fc3012a12b32.1.0.0");var subQ1=sQuery(id+"F1.wireOp",EDGE,"a13d30e3-1256-45f2-88c4-17f94fdc27e3.0.1.0");var subQ2=makeQuery(id+"F1.imprint","INTERSECT",VERTEX,{"derivedFrom":[subQ1,subQ0]});Q78=makeQuery(id+"F1.imprint","IMPRINT",FACE,{"disambiguationData":[TD([[makeQuery(id+"F1.imprint","IMPRINT",EDGE,{"disambiguationData":[TD([[subQ2,-1.0]])],"derivedFrom":subQ1}),-1.0]])]});}
            var Q79;
            {var subQ0=sQuery(id+"F1.wireOp",EDGE,"1122fb87-85ac-472b-868b-fc3012a12b32.2.0.1");var subQ1=sQuery(id+"F1.wireOp",EDGE,"6uq4eEBE-zqJi-hSKM-aljM-bMrpigbcLfnv");var subQ2=makeQuery(id+"F1.imprint","INTERSECT",VERTEX,{"derivedFrom":[subQ1,subQ0]});Q79=makeQuery(id+"F1.imprint","IMPRINT",FACE,{"disambiguationData":[TD([[makeQuery(id+"F1.imprint","IMPRINT",EDGE,{"disambiguationData":[TD([[subQ2,-1.0]])],"derivedFrom":subQ1}),1.0]])]});}
            var Q80;
            {var subQ0=sQuery(id+"F1.wireOp",EDGE,"1122fb87-85ac-472b-868b-fc3012a12b32.1.0.1");var subQ1=sQuery(id+"F1.wireOp",EDGE,"IqfzKEuX-Kduy-EBgq-JfLB-lxs091du6jRf");var subQ2=makeQuery(id+"F1.imprint","INTERSECT",VERTEX,{"derivedFrom":[subQ1,subQ0]});Q80=makeQuery(id+"F1.imprint","IMPRINT",FACE,{"disambiguationData":[TD([[makeQuery(id+"F1.imprint","IMPRINT",EDGE,{"disambiguationData":[TD([[subQ2,-1.0]])],"derivedFrom":subQ1}),-1.0]])]});}
            var Q81;
            {var subQ0=sQuery(id+"F1.wireOp",EDGE,"1122fb87-85ac-472b-868b-fc3012a12b32.1.0.1");var subQ1=sQuery(id+"F1.wireOp",EDGE,"a13d30e3-1256-45f2-88c4-17f94fdc27e3.0.4.0");var subQ2=makeQuery(id+"F1.imprint","INTERSECT",VERTEX,{"derivedFrom":[subQ1,subQ0]});Q81=makeQuery(id+"F1.imprint","IMPRINT",FACE,{"disambiguationData":[TD([[makeQuery(id+"F1.imprint","IMPRINT",EDGE,{"disambiguationData":[TD([[subQ2,-1.0]])],"derivedFrom":subQ1}),-1.0]])]});}
            var Q82;
            {var subQ0=sQuery(id+"F1.wireOp",EDGE,"1122fb87-85ac-472b-868b-fc3012a12b32.1.0.1");var subQ1=sQuery(id+"F1.wireOp",EDGE,"a13d30e3-1256-45f2-88c4-17f94fdc27e3.0.3.1");var subQ2=makeQuery(id+"F1.imprint","INTERSECT",VERTEX,{"derivedFrom":[subQ1,subQ0]});Q82=makeQuery(id+"F1.imprint","IMPRINT",FACE,{"disambiguationData":[TD([[makeQuery(id+"F1.imprint","IMPRINT",EDGE,{"disambiguationData":[TD([[subQ2,-1.0]])],"derivedFrom":subQ1}),-1.0]])]});}
            var Q83;
            {var subQ0=sQuery(id+"F1.wireOp",EDGE,"1122fb87-85ac-472b-868b-fc3012a12b32.1.0.1");var subQ1=sQuery(id+"F1.wireOp",EDGE,"a13d30e3-1256-45f2-88c4-17f94fdc27e3.0.1.1");var subQ2=makeQuery(id+"F1.imprint","INTERSECT",VERTEX,{"derivedFrom":[subQ1,subQ0]});Q83=makeQuery(id+"F1.imprint","IMPRINT",FACE,{"disambiguationData":[TD([[makeQuery(id+"F1.imprint","IMPRINT",EDGE,{"disambiguationData":[TD([[subQ2,-1.0]])],"derivedFrom":subQ1}),-1.0]])]});}
            var Q84;
            {var subQ0=sQuery(id+"F1.wireOp",EDGE,"1122fb87-85ac-472b-868b-fc3012a12b32.1.0.0");var subQ1=sQuery(id+"F1.wireOp",EDGE,"a13d30e3-1256-45f2-88c4-17f94fdc27e3.0.4.0");var subQ2=makeQuery(id+"F1.imprint","INTERSECT",VERTEX,{"derivedFrom":[subQ1,subQ0]});Q84=makeQuery(id+"F1.imprint","IMPRINT",FACE,{"disambiguationData":[TD([[makeQuery(id+"F1.imprint","IMPRINT",EDGE,{"disambiguationData":[TD([[subQ2,-1.0]])],"derivedFrom":subQ1}),-1.0]])]});}
            var Q85;
            {var subQ0=sQuery(id+"F1.wireOp",EDGE,"1122fb87-85ac-472b-868b-fc3012a12b32.1.0.1");var subQ1=sQuery(id+"F1.wireOp",EDGE,"a13d30e3-1256-45f2-88c4-17f94fdc27e3.0.2.0");var subQ2=makeQuery(id+"F1.imprint","INTERSECT",VERTEX,{"derivedFrom":[subQ1,subQ0]});Q85=makeQuery(id+"F1.imprint","IMPRINT",FACE,{"disambiguationData":[TD([[makeQuery(id+"F1.imprint","IMPRINT",EDGE,{"disambiguationData":[TD([[subQ2,-1.0]])],"derivedFrom":subQ1}),-1.0]])]});}
            var Q86;
            {var subQ0=sQuery(id+"F1.wireOp",EDGE,"1122fb87-85ac-472b-868b-fc3012a12b32.2.0.1");var subQ1=sQuery(id+"F1.wireOp",EDGE,"a13d30e3-1256-45f2-88c4-17f94fdc27e3.0.3.1");var subQ2=makeQuery(id+"F1.imprint","INTERSECT",VERTEX,{"derivedFrom":[subQ1,subQ0]});Q86=makeQuery(id+"F1.imprint","IMPRINT",FACE,{"disambiguationData":[TD([[makeQuery(id+"F1.imprint","IMPRINT",EDGE,{"disambiguationData":[TD([[subQ2,-1.0]])],"derivedFrom":subQ1}),-1.0]])]});}
            var Q87;
            {var subQ0=sQuery(id+"F1.wireOp",EDGE,"1122fb87-85ac-472b-868b-fc3012a12b32.1.0.0");var subQ1=sQuery(id+"F1.wireOp",EDGE,"a13d30e3-1256-45f2-88c4-17f94fdc27e3.0.2.0");var subQ2=makeQuery(id+"F1.imprint","INTERSECT",VERTEX,{"derivedFrom":[subQ1,subQ0]});Q87=makeQuery(id+"F1.imprint","IMPRINT",FACE,{"disambiguationData":[TD([[makeQuery(id+"F1.imprint","IMPRINT",EDGE,{"disambiguationData":[TD([[subQ2,-1.0]])],"derivedFrom":subQ1}),-1.0]])]});}
            var Q88;
            {var subQ0=sQuery(id+"F1.wireOp",EDGE,"1122fb87-85ac-472b-868b-fc3012a12b32.2.0.1");var subQ1=sQuery(id+"F1.wireOp",EDGE,"a13d30e3-1256-45f2-88c4-17f94fdc27e3.0.1.1");var subQ2=makeQuery(id+"F1.imprint","INTERSECT",VERTEX,{"derivedFrom":[subQ1,subQ0]});Q88=makeQuery(id+"F1.imprint","IMPRINT",FACE,{"disambiguationData":[TD([[makeQuery(id+"F1.imprint","IMPRINT",EDGE,{"disambiguationData":[TD([[subQ2,-1.0]])],"derivedFrom":subQ1}),-1.0]])]});}
            var Q89;
            {var subQ0=sQuery(id+"F1.wireOp",EDGE,"1122fb87-85ac-472b-868b-fc3012a12b32.1.0.1");var subQ1=sQuery(id+"F1.wireOp",EDGE,"6uq4eEBE-zqJi-hSKM-aljM-bMrpigbcLfnv");var subQ2=makeQuery(id+"F1.imprint","INTERSECT",VERTEX,{"derivedFrom":[subQ1,subQ0]});Q89=makeQuery(id+"F1.imprint","IMPRINT",FACE,{"disambiguationData":[TD([[makeQuery(id+"F1.imprint","IMPRINT",EDGE,{"disambiguationData":[TD([[subQ2,-1.0]])],"derivedFrom":subQ1}),-1.0]])]});}
            var Q90;
            {var subQ0=sQuery(id+"F1.wireOp",EDGE,"1122fb87-85ac-472b-868b-fc3012a12b32.1.0.1");var subQ1=sQuery(id+"F1.wireOp",EDGE,"6uq4eEBE-zqJi-hSKM-aljM-bMrpigbcLfnv");var subQ2=makeQuery(id+"F1.imprint","INTERSECT",VERTEX,{"derivedFrom":[subQ1,subQ0]});Q90=makeQuery(id+"F1.imprint","IMPRINT",FACE,{"disambiguationData":[TD([[makeQuery(id+"F1.imprint","IMPRINT",EDGE,{"disambiguationData":[TD([[subQ2,-1.0]])],"derivedFrom":subQ1}),1.0]])]});}
            var Q91;
            {var subQ0=sQuery(id+"F1.wireOp",EDGE,"1122fb87-85ac-472b-868b-fc3012a12b32.1.0.1");var subQ1=sQuery(id+"F1.wireOp",EDGE,"a13d30e3-1256-45f2-88c4-17f94fdc27e3.0.4.1");var subQ2=makeQuery(id+"F1.imprint","INTERSECT",VERTEX,{"derivedFrom":[subQ1,subQ0]});Q91=makeQuery(id+"F1.imprint","IMPRINT",FACE,{"disambiguationData":[TD([[makeQuery(id+"F1.imprint","IMPRINT",EDGE,{"disambiguationData":[TD([[subQ2,-1.0]])],"derivedFrom":subQ1}),-1.0]])]});}
            var Q92;
            {var subQ0=sQuery(id+"F1.wireOp",EDGE,"1122fb87-85ac-472b-868b-fc3012a12b32.1.0.0");var subQ1=sQuery(id+"F1.wireOp",EDGE,"6uq4eEBE-zqJi-hSKM-aljM-bMrpigbcLfnv");var subQ2=makeQuery(id+"F1.imprint","INTERSECT",VERTEX,{"derivedFrom":[subQ1,subQ0]});Q92=makeQuery(id+"F1.imprint","IMPRINT",FACE,{"disambiguationData":[TD([[makeQuery(id+"F1.imprint","IMPRINT",EDGE,{"disambiguationData":[TD([[subQ2,-1.0]])],"derivedFrom":subQ1}),-1.0]])]});}
            var Q93;
            {var subQ0=sQuery(id+"F1.wireOp",EDGE,"1122fb87-85ac-472b-868b-fc3012a12b32.1.0.1");var subQ1=sQuery(id+"F1.wireOp",EDGE,"a13d30e3-1256-45f2-88c4-17f94fdc27e3.0.2.1");var subQ2=makeQuery(id+"F1.imprint","INTERSECT",VERTEX,{"derivedFrom":[subQ1,subQ0]});Q93=makeQuery(id+"F1.imprint","IMPRINT",FACE,{"disambiguationData":[TD([[makeQuery(id+"F1.imprint","IMPRINT",EDGE,{"disambiguationData":[TD([[subQ2,-1.0]])],"derivedFrom":subQ1}),-1.0]])]});}
            var Q94;
            {var subQ0=sQuery(id+"F1.wireOp",EDGE,"1122fb87-85ac-472b-868b-fc3012a12b32.2.0.1");var subQ1=sQuery(id+"F1.wireOp",EDGE,"a13d30e3-1256-45f2-88c4-17f94fdc27e3.0.4.1");var subQ2=makeQuery(id+"F1.imprint","INTERSECT",VERTEX,{"derivedFrom":[subQ1,subQ0]});Q94=makeQuery(id+"F1.imprint","IMPRINT",FACE,{"disambiguationData":[TD([[makeQuery(id+"F1.imprint","IMPRINT",EDGE,{"disambiguationData":[TD([[subQ2,-1.0]])],"derivedFrom":subQ1}),-1.0]])]});}
            var Q95;
            {var subQ0=sQuery(id+"F1.wireOp",EDGE,"1122fb87-85ac-472b-868b-fc3012a12b32.2.0.1");var subQ1=sQuery(id+"F1.wireOp",EDGE,"a13d30e3-1256-45f2-88c4-17f94fdc27e3.0.1.0");var subQ2=makeQuery(id+"F1.imprint","INTERSECT",VERTEX,{"derivedFrom":[subQ1,subQ0]});Q95=makeQuery(id+"F1.imprint","IMPRINT",FACE,{"disambiguationData":[TD([[makeQuery(id+"F1.imprint","IMPRINT",EDGE,{"disambiguationData":[TD([[subQ2,-1.0]])],"derivedFrom":subQ1}),-1.0]])]});}
            var Q96;
            {var subQ0=sQuery(id+"F1.wireOp",EDGE,"1122fb87-85ac-472b-868b-fc3012a12b32.2.0.1");var subQ1=sQuery(id+"F1.wireOp",EDGE,"6uq4eEBE-zqJi-hSKM-aljM-bMrpigbcLfnv");var subQ2=makeQuery(id+"F1.imprint","INTERSECT",VERTEX,{"derivedFrom":[subQ1,subQ0]});Q96=makeQuery(id+"F1.imprint","IMPRINT",FACE,{"disambiguationData":[TD([[makeQuery(id+"F1.imprint","IMPRINT",EDGE,{"disambiguationData":[TD([[subQ2,-1.0]])],"derivedFrom":subQ1}),-1.0]])]});}
            var Q97;
            {var subQ0=sQuery(id+"F1.wireOp",EDGE,"1122fb87-85ac-472b-868b-fc3012a12b32.2.0.1");var subQ1=sQuery(id+"F1.wireOp",EDGE,"a13d30e3-1256-45f2-88c4-17f94fdc27e3.0.3.0");var subQ2=makeQuery(id+"F1.imprint","INTERSECT",VERTEX,{"derivedFrom":[subQ1,subQ0]});Q97=makeQuery(id+"F1.imprint","IMPRINT",FACE,{"disambiguationData":[TD([[makeQuery(id+"F1.imprint","IMPRINT",EDGE,{"disambiguationData":[TD([[subQ2,-1.0]])],"derivedFrom":subQ1}),-1.0]])]});}
            var Q98;
            {var subQ0=sQuery(id+"F1.wireOp",EDGE,"1122fb87-85ac-472b-868b-fc3012a12b32.2.0.1");var subQ1=sQuery(id+"F1.wireOp",EDGE,"a13d30e3-1256-45f2-88c4-17f94fdc27e3.0.4.0");var subQ2=makeQuery(id+"F1.imprint","INTERSECT",VERTEX,{"derivedFrom":[subQ1,subQ0]});Q98=makeQuery(id+"F1.imprint","IMPRINT",FACE,{"disambiguationData":[TD([[makeQuery(id+"F1.imprint","IMPRINT",EDGE,{"disambiguationData":[TD([[subQ2,-1.0]])],"derivedFrom":subQ1}),-1.0]])]});}
            var Q99;
            {var subQ0=sQuery(id+"F1.wireOp",EDGE,"1122fb87-85ac-472b-868b-fc3012a12b32.2.0.1");var subQ1=sQuery(id+"F1.wireOp",EDGE,"a13d30e3-1256-45f2-88c4-17f94fdc27e3.0.2.0");var subQ2=makeQuery(id+"F1.imprint","INTERSECT",VERTEX,{"derivedFrom":[subQ1,subQ0]});Q99=makeQuery(id+"F1.imprint","IMPRINT",FACE,{"disambiguationData":[TD([[makeQuery(id+"F1.imprint","IMPRINT",EDGE,{"disambiguationData":[TD([[subQ2,-1.0]])],"derivedFrom":subQ1}),-1.0]])]});}
            var Q100;
            {var subQ0=sQuery(id+"F1.wireOp",EDGE,"1122fb87-85ac-472b-868b-fc3012a12b32.9.0.1");var subQ1=sQuery(id+"F1.wireOp",EDGE,"a13d30e3-1256-45f2-88c4-17f94fdc27e3.0.3.1");var subQ2=makeQuery(id+"F1.imprint","INTERSECT",VERTEX,{"derivedFrom":[subQ1,subQ0]});Q100=makeQuery(id+"F1.imprint","IMPRINT",FACE,{"disambiguationData":[TD([[makeQuery(id+"F1.imprint","IMPRINT",EDGE,{"disambiguationData":[TD([[subQ2,-1.0]])],"derivedFrom":subQ1}),-1.0]])]});}
            var Q101;
            {var subQ0=sQuery(id+"F1.wireOp",EDGE,"1122fb87-85ac-472b-868b-fc3012a12b32.9.0.1");var subQ1=sQuery(id+"F1.wireOp",EDGE,"a13d30e3-1256-45f2-88c4-17f94fdc27e3.0.1.1");var subQ2=makeQuery(id+"F1.imprint","INTERSECT",VERTEX,{"derivedFrom":[subQ1,subQ0]});Q101=makeQuery(id+"F1.imprint","IMPRINT",FACE,{"disambiguationData":[TD([[makeQuery(id+"F1.imprint","IMPRINT",EDGE,{"disambiguationData":[TD([[subQ2,-1.0]])],"derivedFrom":subQ1}),-1.0]])]});}
            var Q102;
            {var subQ0=sQuery(id+"F1.wireOp",EDGE,"1122fb87-85ac-472b-868b-fc3012a12b32.8.0.1");var subQ1=sQuery(id+"F1.wireOp",EDGE,"6uq4eEBE-zqJi-hSKM-aljM-bMrpigbcLfnv");var subQ2=makeQuery(id+"F1.imprint","INTERSECT",VERTEX,{"derivedFrom":[subQ1,subQ0]});Q102=makeQuery(id+"F1.imprint","IMPRINT",FACE,{"disambiguationData":[TD([[makeQuery(id+"F1.imprint","IMPRINT",EDGE,{"disambiguationData":[TD([[subQ2,-1.0]])],"derivedFrom":subQ1}),1.0]])]});}
            var Q103;
            {var subQ0=sQuery(id+"F1.wireOp",EDGE,"1122fb87-85ac-472b-868b-fc3012a12b32.8.0.0");var subQ1=sQuery(id+"F1.wireOp",EDGE,"a13d30e3-1256-45f2-88c4-17f94fdc27e3.0.4.0");var subQ2=makeQuery(id+"F1.imprint","INTERSECT",VERTEX,{"derivedFrom":[subQ1,subQ0]});Q103=makeQuery(id+"F1.imprint","IMPRINT",FACE,{"disambiguationData":[TD([[makeQuery(id+"F1.imprint","IMPRINT",EDGE,{"disambiguationData":[TD([[subQ2,-1.0]])],"derivedFrom":subQ1}),-1.0]])]});}
            var Q104;
            {var subQ0=sQuery(id+"F1.wireOp",EDGE,"1122fb87-85ac-472b-868b-fc3012a12b32.9.0.1");var subQ1=sQuery(id+"F1.wireOp",EDGE,"a13d30e3-1256-45f2-88c4-17f94fdc27e3.0.3.0");var subQ2=makeQuery(id+"F1.imprint","INTERSECT",VERTEX,{"derivedFrom":[subQ1,subQ0]});Q104=makeQuery(id+"F1.imprint","IMPRINT",FACE,{"disambiguationData":[TD([[makeQuery(id+"F1.imprint","IMPRINT",EDGE,{"disambiguationData":[TD([[subQ2,-1.0]])],"derivedFrom":subQ1}),-1.0]])]});}
            var Q105;
            {var subQ0=sQuery(id+"F1.wireOp",EDGE,"1122fb87-85ac-472b-868b-fc3012a12b32.8.0.1");var subQ1=sQuery(id+"F1.wireOp",EDGE,"a13d30e3-1256-45f2-88c4-17f94fdc27e3.0.4.1");var subQ2=makeQuery(id+"F1.imprint","INTERSECT",VERTEX,{"derivedFrom":[subQ1,subQ0]});Q105=makeQuery(id+"F1.imprint","IMPRINT",FACE,{"disambiguationData":[TD([[makeQuery(id+"F1.imprint","IMPRINT",EDGE,{"disambiguationData":[TD([[subQ2,-1.0]])],"derivedFrom":subQ1}),-1.0]])]});}
            var Q106;
            {var subQ0=sQuery(id+"F1.wireOp",EDGE,"1122fb87-85ac-472b-868b-fc3012a12b32.9.0.1");var subQ1=sQuery(id+"F1.wireOp",EDGE,"a13d30e3-1256-45f2-88c4-17f94fdc27e3.0.1.0");var subQ2=makeQuery(id+"F1.imprint","INTERSECT",VERTEX,{"derivedFrom":[subQ1,subQ0]});Q106=makeQuery(id+"F1.imprint","IMPRINT",FACE,{"disambiguationData":[TD([[makeQuery(id+"F1.imprint","IMPRINT",EDGE,{"disambiguationData":[TD([[subQ2,-1.0]])],"derivedFrom":subQ1}),-1.0]])]});}
            var Q107;
            {var subQ0=sQuery(id+"F1.wireOp",EDGE,"1122fb87-85ac-472b-868b-fc3012a12b32.8.0.0");var subQ1=sQuery(id+"F1.wireOp",EDGE,"6uq4eEBE-zqJi-hSKM-aljM-bMrpigbcLfnv");var subQ2=makeQuery(id+"F1.imprint","INTERSECT",VERTEX,{"derivedFrom":[subQ1,subQ0]});Q107=makeQuery(id+"F1.imprint","IMPRINT",FACE,{"disambiguationData":[TD([[makeQuery(id+"F1.imprint","IMPRINT",EDGE,{"disambiguationData":[TD([[subQ2,-1.0]])],"derivedFrom":subQ1}),-1.0]])]});}
            var Q108;
            {var subQ0=sQuery(id+"F1.wireOp",EDGE,"1122fb87-85ac-472b-868b-fc3012a12b32.9.0.1");var subQ1=sQuery(id+"F1.wireOp",EDGE,"6uq4eEBE-zqJi-hSKM-aljM-bMrpigbcLfnv");var subQ2=makeQuery(id+"F1.imprint","INTERSECT",VERTEX,{"derivedFrom":[subQ1,subQ0]});Q108=makeQuery(id+"F1.imprint","IMPRINT",FACE,{"disambiguationData":[TD([[makeQuery(id+"F1.imprint","IMPRINT",EDGE,{"disambiguationData":[TD([[subQ2,-1.0]])],"derivedFrom":subQ1}),-1.0]])]});}
            var Q109;
            {var subQ0=sQuery(id+"F1.wireOp",EDGE,"1122fb87-85ac-472b-868b-fc3012a12b32.9.0.1");var subQ1=sQuery(id+"F1.wireOp",EDGE,"a13d30e3-1256-45f2-88c4-17f94fdc27e3.0.4.0");var subQ2=makeQuery(id+"F1.imprint","INTERSECT",VERTEX,{"derivedFrom":[subQ1,subQ0]});Q109=makeQuery(id+"F1.imprint","IMPRINT",FACE,{"disambiguationData":[TD([[makeQuery(id+"F1.imprint","IMPRINT",EDGE,{"disambiguationData":[TD([[subQ2,-1.0]])],"derivedFrom":subQ1}),-1.0]])]});}
            var Q110;
            {var subQ0=sQuery(id+"F1.wireOp",EDGE,"1122fb87-85ac-472b-868b-fc3012a12b32.9.0.1");var subQ1=sQuery(id+"F1.wireOp",EDGE,"6uq4eEBE-zqJi-hSKM-aljM-bMrpigbcLfnv");var subQ2=makeQuery(id+"F1.imprint","INTERSECT",VERTEX,{"derivedFrom":[subQ1,subQ0]});Q110=makeQuery(id+"F1.imprint","IMPRINT",FACE,{"disambiguationData":[TD([[makeQuery(id+"F1.imprint","IMPRINT",EDGE,{"disambiguationData":[TD([[subQ2,-1.0]])],"derivedFrom":subQ1}),1.0]])]});}
            var Q111;
            {var subQ0=sQuery(id+"F1.wireOp",EDGE,"1122fb87-85ac-472b-868b-fc3012a12b32.8.0.1");var subQ1=sQuery(id+"F1.wireOp",EDGE,"a13d30e3-1256-45f2-88c4-17f94fdc27e3.0.2.1");var subQ2=makeQuery(id+"F1.imprint","INTERSECT",VERTEX,{"derivedFrom":[subQ1,subQ0]});Q111=makeQuery(id+"F1.imprint","IMPRINT",FACE,{"disambiguationData":[TD([[makeQuery(id+"F1.imprint","IMPRINT",EDGE,{"disambiguationData":[TD([[subQ2,-1.0]])],"derivedFrom":subQ1}),-1.0]])]});}
            var Q112;
            {var subQ0=sQuery(id+"F1.wireOp",EDGE,"1122fb87-85ac-472b-868b-fc3012a12b32.8.0.0");var subQ1=sQuery(id+"F1.wireOp",EDGE,"a13d30e3-1256-45f2-88c4-17f94fdc27e3.0.2.0");var subQ2=makeQuery(id+"F1.imprint","INTERSECT",VERTEX,{"derivedFrom":[subQ1,subQ0]});Q112=makeQuery(id+"F1.imprint","IMPRINT",FACE,{"disambiguationData":[TD([[makeQuery(id+"F1.imprint","IMPRINT",EDGE,{"disambiguationData":[TD([[subQ2,-1.0]])],"derivedFrom":subQ1}),-1.0]])]});}
            var Q113;
            {var subQ0=sQuery(id+"F1.wireOp",EDGE,"1122fb87-85ac-472b-868b-fc3012a12b32.9.0.1");var subQ1=sQuery(id+"F1.wireOp",EDGE,"a13d30e3-1256-45f2-88c4-17f94fdc27e3.0.4.1");var subQ2=makeQuery(id+"F1.imprint","INTERSECT",VERTEX,{"derivedFrom":[subQ1,subQ0]});Q113=makeQuery(id+"F1.imprint","IMPRINT",FACE,{"disambiguationData":[TD([[makeQuery(id+"F1.imprint","IMPRINT",EDGE,{"disambiguationData":[TD([[subQ2,-1.0]])],"derivedFrom":subQ1}),-1.0]])]});}
            var Q114;
            {var subQ0=sQuery(id+"F1.wireOp",EDGE,"1122fb87-85ac-472b-868b-fc3012a12b32.8.0.1");var subQ1=sQuery(id+"F1.wireOp",EDGE,"IqfzKEuX-Kduy-EBgq-JfLB-lxs091du6jRf");var subQ2=makeQuery(id+"F1.imprint","INTERSECT",VERTEX,{"derivedFrom":[subQ1,subQ0]});Q114=makeQuery(id+"F1.imprint","IMPRINT",FACE,{"disambiguationData":[TD([[makeQuery(id+"F1.imprint","IMPRINT",EDGE,{"disambiguationData":[TD([[subQ2,-1.0]])],"derivedFrom":subQ1}),-1.0]])]});}
            var Q115;
            {var subQ0=sQuery(id+"F1.wireOp",EDGE,"1122fb87-85ac-472b-868b-fc3012a12b32.9.0.1");var subQ1=sQuery(id+"F1.wireOp",EDGE,"a13d30e3-1256-45f2-88c4-17f94fdc27e3.0.2.0");var subQ2=makeQuery(id+"F1.imprint","INTERSECT",VERTEX,{"derivedFrom":[subQ1,subQ0]});Q115=makeQuery(id+"F1.imprint","IMPRINT",FACE,{"disambiguationData":[TD([[makeQuery(id+"F1.imprint","IMPRINT",EDGE,{"disambiguationData":[TD([[subQ2,-1.0]])],"derivedFrom":subQ1}),-1.0]])]});}
            var Q116;
            {var subQ0=sQuery(id+"F1.wireOp",EDGE,"1122fb87-85ac-472b-868b-fc3012a12b32.9.0.1");var subQ1=sQuery(id+"F1.wireOp",EDGE,"a13d30e3-1256-45f2-88c4-17f94fdc27e3.0.2.1");var subQ2=makeQuery(id+"F1.imprint","INTERSECT",VERTEX,{"derivedFrom":[subQ1,subQ0]});Q116=makeQuery(id+"F1.imprint","IMPRINT",FACE,{"disambiguationData":[TD([[makeQuery(id+"F1.imprint","IMPRINT",EDGE,{"disambiguationData":[TD([[subQ2,-1.0]])],"derivedFrom":subQ1}),-1.0]])]});}
            var Q117;
            {var subQ0=sQuery(id+"F1.wireOp",EDGE,"1122fb87-85ac-472b-868b-fc3012a12b32.9.0.1");var subQ1=sQuery(id+"F1.wireOp",EDGE,"IqfzKEuX-Kduy-EBgq-JfLB-lxs091du6jRf");var subQ2=makeQuery(id+"F1.imprint","INTERSECT",VERTEX,{"derivedFrom":[subQ1,subQ0]});Q117=makeQuery(id+"F1.imprint","IMPRINT",FACE,{"disambiguationData":[TD([[makeQuery(id+"F1.imprint","IMPRINT",EDGE,{"disambiguationData":[TD([[subQ2,-1.0]])],"derivedFrom":subQ1}),-1.0]])]});}
            var Q118;
            {var subQ0=sQuery(id+"F1.wireOp",EDGE,"1122fb87-85ac-472b-868b-fc3012a12b32.8.0.1");var subQ1=sQuery(id+"F1.wireOp",EDGE,"a13d30e3-1256-45f2-88c4-17f94fdc27e3.0.3.1");var subQ2=makeQuery(id+"F1.imprint","INTERSECT",VERTEX,{"derivedFrom":[subQ1,subQ0]});Q118=makeQuery(id+"F1.imprint","IMPRINT",FACE,{"disambiguationData":[TD([[makeQuery(id+"F1.imprint","IMPRINT",EDGE,{"disambiguationData":[TD([[subQ2,-1.0]])],"derivedFrom":subQ1}),-1.0]])]});}
            var Q119;
            {var subQ0=sQuery(id+"F1.wireOp",EDGE,"1122fb87-85ac-472b-868b-fc3012a12b32.8.0.0");var subQ1=sQuery(id+"F1.wireOp",EDGE,"a13d30e3-1256-45f2-88c4-17f94fdc27e3.0.3.0");var subQ2=makeQuery(id+"F1.imprint","INTERSECT",VERTEX,{"derivedFrom":[subQ1,subQ0]});Q119=makeQuery(id+"F1.imprint","IMPRINT",FACE,{"disambiguationData":[TD([[makeQuery(id+"F1.imprint","IMPRINT",EDGE,{"disambiguationData":[TD([[subQ2,-1.0]])],"derivedFrom":subQ1}),-1.0]])]});}
            var Q120;
            {var subQ0=sQuery(id+"F1.wireOp",EDGE,"1122fb87-85ac-472b-868b-fc3012a12b32.8.0.1");var subQ1=sQuery(id+"F1.wireOp",EDGE,"a13d30e3-1256-45f2-88c4-17f94fdc27e3.0.1.1");var subQ2=makeQuery(id+"F1.imprint","INTERSECT",VERTEX,{"derivedFrom":[subQ1,subQ0]});Q120=makeQuery(id+"F1.imprint","IMPRINT",FACE,{"disambiguationData":[TD([[makeQuery(id+"F1.imprint","IMPRINT",EDGE,{"disambiguationData":[TD([[subQ2,-1.0]])],"derivedFrom":subQ1}),-1.0]])]});}
            var Q121;
            {var subQ0=sQuery(id+"F1.wireOp",EDGE,"1122fb87-85ac-472b-868b-fc3012a12b32.8.0.0");var subQ1=sQuery(id+"F1.wireOp",EDGE,"a13d30e3-1256-45f2-88c4-17f94fdc27e3.0.1.0");var subQ2=makeQuery(id+"F1.imprint","INTERSECT",VERTEX,{"derivedFrom":[subQ1,subQ0]});Q121=makeQuery(id+"F1.imprint","IMPRINT",FACE,{"disambiguationData":[TD([[makeQuery(id+"F1.imprint","IMPRINT",EDGE,{"disambiguationData":[TD([[subQ2,-1.0]])],"derivedFrom":subQ1}),-1.0]])]});}
            var Q122;
            {var subQ0=sQuery(id+"F1.wireOp",EDGE,"1122fb87-85ac-472b-868b-fc3012a12b32.8.0.1");var subQ1=sQuery(id+"F1.wireOp",EDGE,"6uq4eEBE-zqJi-hSKM-aljM-bMrpigbcLfnv");var subQ2=makeQuery(id+"F1.imprint","INTERSECT",VERTEX,{"derivedFrom":[subQ1,subQ0]});Q122=makeQuery(id+"F1.imprint","IMPRINT",FACE,{"disambiguationData":[TD([[makeQuery(id+"F1.imprint","IMPRINT",EDGE,{"disambiguationData":[TD([[subQ2,-1.0]])],"derivedFrom":subQ1}),-1.0]])]});}
            var Q123;
            {var subQ0=sQuery(id+"F1.wireOp",EDGE,"1122fb87-85ac-472b-868b-fc3012a12b32.8.0.1");var subQ1=sQuery(id+"F1.wireOp",EDGE,"a13d30e3-1256-45f2-88c4-17f94fdc27e3.0.4.0");var subQ2=makeQuery(id+"F1.imprint","INTERSECT",VERTEX,{"derivedFrom":[subQ1,subQ0]});Q123=makeQuery(id+"F1.imprint","IMPRINT",FACE,{"disambiguationData":[TD([[makeQuery(id+"F1.imprint","IMPRINT",EDGE,{"disambiguationData":[TD([[subQ2,-1.0]])],"derivedFrom":subQ1}),-1.0]])]});}
            var Q124;
            {var subQ0=sQuery(id+"F1.wireOp",EDGE,"1122fb87-85ac-472b-868b-fc3012a12b32.8.0.1");var subQ1=sQuery(id+"F1.wireOp",EDGE,"a13d30e3-1256-45f2-88c4-17f94fdc27e3.0.2.0");var subQ2=makeQuery(id+"F1.imprint","INTERSECT",VERTEX,{"derivedFrom":[subQ1,subQ0]});Q124=makeQuery(id+"F1.imprint","IMPRINT",FACE,{"disambiguationData":[TD([[makeQuery(id+"F1.imprint","IMPRINT",EDGE,{"disambiguationData":[TD([[subQ2,-1.0]])],"derivedFrom":subQ1}),-1.0]])]});}
            var Q125;
            {var subQ0=sQuery(id+"F1.wireOp",EDGE,"1122fb87-85ac-472b-868b-fc3012a12b32.8.0.1");var subQ1=sQuery(id+"F1.wireOp",EDGE,"a13d30e3-1256-45f2-88c4-17f94fdc27e3.0.1.0");var subQ2=makeQuery(id+"F1.imprint","INTERSECT",VERTEX,{"derivedFrom":[subQ1,subQ0]});Q125=makeQuery(id+"F1.imprint","IMPRINT",FACE,{"disambiguationData":[TD([[makeQuery(id+"F1.imprint","IMPRINT",EDGE,{"disambiguationData":[TD([[subQ2,-1.0]])],"derivedFrom":subQ1}),-1.0]])]});}
            var Q126;
            {var subQ0=sQuery(id+"F1.wireOp",EDGE,"1122fb87-85ac-472b-868b-fc3012a12b32.8.0.1");var subQ1=sQuery(id+"F1.wireOp",EDGE,"a13d30e3-1256-45f2-88c4-17f94fdc27e3.0.3.0");var subQ2=makeQuery(id+"F1.imprint","INTERSECT",VERTEX,{"derivedFrom":[subQ1,subQ0]});Q126=makeQuery(id+"F1.imprint","IMPRINT",FACE,{"disambiguationData":[TD([[makeQuery(id+"F1.imprint","IMPRINT",EDGE,{"disambiguationData":[TD([[subQ2,-1.0]])],"derivedFrom":subQ1}),-1.0]])]});}
            var Q127;
            {var subQ0=sQuery(id+"F1.wireOp",EDGE,"1122fb87-85ac-472b-868b-fc3012a12b32.10.0.1");var subQ1=sQuery(id+"F1.wireOp",EDGE,"a13d30e3-1256-45f2-88c4-17f94fdc27e3.0.3.1");var subQ2=makeQuery(id+"F1.imprint","INTERSECT",VERTEX,{"derivedFrom":[subQ1,subQ0]});Q127=makeQuery(id+"F1.imprint","IMPRINT",FACE,{"disambiguationData":[TD([[makeQuery(id+"F1.imprint","IMPRINT",EDGE,{"disambiguationData":[TD([[subQ2,-1.0]])],"derivedFrom":subQ1}),-1.0]])]});}
            var Q128;
            {var subQ0=sQuery(id+"F1.wireOp",EDGE,"1122fb87-85ac-472b-868b-fc3012a12b32.10.0.1");var subQ1=sQuery(id+"F1.wireOp",EDGE,"a13d30e3-1256-45f2-88c4-17f94fdc27e3.0.1.1");var subQ2=makeQuery(id+"F1.imprint","INTERSECT",VERTEX,{"derivedFrom":[subQ1,subQ0]});Q128=makeQuery(id+"F1.imprint","IMPRINT",FACE,{"disambiguationData":[TD([[makeQuery(id+"F1.imprint","IMPRINT",EDGE,{"disambiguationData":[TD([[subQ2,-1.0]])],"derivedFrom":subQ1}),-1.0]])]});}
            var Q129;
            {var subQ0=sQuery(id+"F1.wireOp",EDGE,"1122fb87-85ac-472b-868b-fc3012a12b32.10.0.1");var subQ1=sQuery(id+"F1.wireOp",EDGE,"a13d30e3-1256-45f2-88c4-17f94fdc27e3.0.3.0");var subQ2=makeQuery(id+"F1.imprint","INTERSECT",VERTEX,{"derivedFrom":[subQ1,subQ0]});Q129=makeQuery(id+"F1.imprint","IMPRINT",FACE,{"disambiguationData":[TD([[makeQuery(id+"F1.imprint","IMPRINT",EDGE,{"disambiguationData":[TD([[subQ2,-1.0]])],"derivedFrom":subQ1}),-1.0]])]});}
            var Q130;
            {var subQ0=sQuery(id+"F1.wireOp",EDGE,"1122fb87-85ac-472b-868b-fc3012a12b32.10.0.1");var subQ1=sQuery(id+"F1.wireOp",EDGE,"a13d30e3-1256-45f2-88c4-17f94fdc27e3.0.1.0");var subQ2=makeQuery(id+"F1.imprint","INTERSECT",VERTEX,{"derivedFrom":[subQ1,subQ0]});Q130=makeQuery(id+"F1.imprint","IMPRINT",FACE,{"disambiguationData":[TD([[makeQuery(id+"F1.imprint","IMPRINT",EDGE,{"disambiguationData":[TD([[subQ2,-1.0]])],"derivedFrom":subQ1}),-1.0]])]});}
            var Q131;
            {var subQ0=sQuery(id+"F1.wireOp",EDGE,"1122fb87-85ac-472b-868b-fc3012a12b32.10.0.1");var subQ1=sQuery(id+"F1.wireOp",EDGE,"a13d30e3-1256-45f2-88c4-17f94fdc27e3.0.4.0");var subQ2=makeQuery(id+"F1.imprint","INTERSECT",VERTEX,{"derivedFrom":[subQ1,subQ0]});Q131=makeQuery(id+"F1.imprint","IMPRINT",FACE,{"disambiguationData":[TD([[makeQuery(id+"F1.imprint","IMPRINT",EDGE,{"disambiguationData":[TD([[subQ2,-1.0]])],"derivedFrom":subQ1}),-1.0]])]});}
            var Q132;
            {var subQ0=sQuery(id+"F1.wireOp",EDGE,"1122fb87-85ac-472b-868b-fc3012a12b32.10.0.1");var subQ1=sQuery(id+"F1.wireOp",EDGE,"a13d30e3-1256-45f2-88c4-17f94fdc27e3.0.4.1");var subQ2=makeQuery(id+"F1.imprint","INTERSECT",VERTEX,{"derivedFrom":[subQ1,subQ0]});Q132=makeQuery(id+"F1.imprint","IMPRINT",FACE,{"disambiguationData":[TD([[makeQuery(id+"F1.imprint","IMPRINT",EDGE,{"disambiguationData":[TD([[subQ2,-1.0]])],"derivedFrom":subQ1}),-1.0]])]});}
            var Q133;
            {var subQ0=sQuery(id+"F1.wireOp",EDGE,"1122fb87-85ac-472b-868b-fc3012a12b32.10.0.1");var subQ1=sQuery(id+"F1.wireOp",EDGE,"6uq4eEBE-zqJi-hSKM-aljM-bMrpigbcLfnv");var subQ2=makeQuery(id+"F1.imprint","INTERSECT",VERTEX,{"derivedFrom":[subQ1,subQ0]});Q133=makeQuery(id+"F1.imprint","IMPRINT",FACE,{"disambiguationData":[TD([[makeQuery(id+"F1.imprint","IMPRINT",EDGE,{"disambiguationData":[TD([[subQ2,-1.0]])],"derivedFrom":subQ1}),-1.0]])]});}
            var Q134;
            {var subQ0=sQuery(id+"F1.wireOp",EDGE,"1122fb87-85ac-472b-868b-fc3012a12b32.10.0.1");var subQ1=sQuery(id+"F1.wireOp",EDGE,"a13d30e3-1256-45f2-88c4-17f94fdc27e3.0.2.0");var subQ2=makeQuery(id+"F1.imprint","INTERSECT",VERTEX,{"derivedFrom":[subQ1,subQ0]});Q134=makeQuery(id+"F1.imprint","IMPRINT",FACE,{"disambiguationData":[TD([[makeQuery(id+"F1.imprint","IMPRINT",EDGE,{"disambiguationData":[TD([[subQ2,-1.0]])],"derivedFrom":subQ1}),-1.0]])]});}
            var Q135;
            {var subQ0=sQuery(id+"F1.wireOp",EDGE,"1122fb87-85ac-472b-868b-fc3012a12b32.10.0.1");var subQ1=sQuery(id+"F1.wireOp",EDGE,"IqfzKEuX-Kduy-EBgq-JfLB-lxs091du6jRf");var subQ2=makeQuery(id+"F1.imprint","INTERSECT",VERTEX,{"derivedFrom":[subQ1,subQ0]});Q135=makeQuery(id+"F1.imprint","IMPRINT",FACE,{"disambiguationData":[TD([[makeQuery(id+"F1.imprint","IMPRINT",EDGE,{"disambiguationData":[TD([[subQ2,-1.0]])],"derivedFrom":subQ1}),-1.0]])]});}
            var Q136;
            {var subQ0=sQuery(id+"F1.wireOp",EDGE,"1122fb87-85ac-472b-868b-fc3012a12b32.10.0.1");var subQ1=sQuery(id+"F1.wireOp",EDGE,"6uq4eEBE-zqJi-hSKM-aljM-bMrpigbcLfnv");var subQ2=makeQuery(id+"F1.imprint","INTERSECT",VERTEX,{"derivedFrom":[subQ1,subQ0]});Q136=makeQuery(id+"F1.imprint","IMPRINT",FACE,{"disambiguationData":[TD([[makeQuery(id+"F1.imprint","IMPRINT",EDGE,{"disambiguationData":[TD([[subQ2,-1.0]])],"derivedFrom":subQ1}),1.0]])]});}
            var Q137;
            {var subQ0=sQuery(id+"F1.wireOp",EDGE,"1122fb87-85ac-472b-868b-fc3012a12b32.10.0.1");var subQ1=sQuery(id+"F1.wireOp",EDGE,"a13d30e3-1256-45f2-88c4-17f94fdc27e3.0.2.1");var subQ2=makeQuery(id+"F1.imprint","INTERSECT",VERTEX,{"derivedFrom":[subQ1,subQ0]});Q137=makeQuery(id+"F1.imprint","IMPRINT",FACE,{"disambiguationData":[TD([[makeQuery(id+"F1.imprint","IMPRINT",EDGE,{"disambiguationData":[TD([[subQ2,-1.0]])],"derivedFrom":subQ1}),-1.0]])]});}
            var Q138;
            {var subQ0=sQuery(id+"F1.wireOp",EDGE,"1122fb87-85ac-472b-868b-fc3012a12b32.2.0.0");var subQ1=sQuery(id+"F1.wireOp",EDGE,"6uq4eEBE-zqJi-hSKM-aljM-bMrpigbcLfnv");var subQ2=makeQuery(id+"F1.imprint","INTERSECT",VERTEX,{"derivedFrom":[subQ1,subQ0]});Q138=makeQuery(id+"F1.imprint","IMPRINT",FACE,{"disambiguationData":[TD([[makeQuery(id+"F1.imprint","IMPRINT",EDGE,{"disambiguationData":[TD([[subQ2,-1.0]])],"derivedFrom":subQ1}),-1.0]])]});}
            var Q139;
            {var subQ0=sQuery(id+"F1.wireOp",EDGE,"1122fb87-85ac-472b-868b-fc3012a12b32.3.0.1");var subQ1=sQuery(id+"F1.wireOp",EDGE,"6uq4eEBE-zqJi-hSKM-aljM-bMrpigbcLfnv");var subQ2=makeQuery(id+"F1.imprint","INTERSECT",VERTEX,{"derivedFrom":[subQ1,subQ0]});Q139=makeQuery(id+"F1.imprint","IMPRINT",FACE,{"disambiguationData":[TD([[makeQuery(id+"F1.imprint","IMPRINT",EDGE,{"disambiguationData":[TD([[subQ2,-1.0]])],"derivedFrom":subQ1}),-1.0]])]});}
            var Q140;
            {var subQ0=sQuery(id+"F1.wireOp",EDGE,"1122fb87-85ac-472b-868b-fc3012a12b32.3.0.0");var subQ1=sQuery(id+"F1.wireOp",EDGE,"6uq4eEBE-zqJi-hSKM-aljM-bMrpigbcLfnv");var subQ2=makeQuery(id+"F1.imprint","INTERSECT",VERTEX,{"derivedFrom":[subQ1,subQ0]});Q140=makeQuery(id+"F1.imprint","IMPRINT",FACE,{"disambiguationData":[TD([[makeQuery(id+"F1.imprint","IMPRINT",EDGE,{"disambiguationData":[TD([[subQ2,-1.0]])],"derivedFrom":subQ1}),-1.0]])]});}
            var Q141;
            {var subQ0=sQuery(id+"F1.wireOp",EDGE,"1122fb87-85ac-472b-868b-fc3012a12b32.7.0.0");var subQ1=sQuery(id+"F1.wireOp",EDGE,"6uq4eEBE-zqJi-hSKM-aljM-bMrpigbcLfnv");var subQ2=makeQuery(id+"F1.imprint","INTERSECT",VERTEX,{"derivedFrom":[subQ1,subQ0]});Q141=makeQuery(id+"F1.imprint","IMPRINT",FACE,{"disambiguationData":[TD([[makeQuery(id+"F1.imprint","IMPRINT",EDGE,{"disambiguationData":[TD([[subQ2,-1.0]])],"derivedFrom":subQ1}),-1.0]])]});}
            var Q142;
            {var subQ0=sQuery(id+"F1.wireOp",EDGE,"9AYXCysi-gJ8l-qpYG-XvAO-eWvyKQmG9Npc");var subQ1=sQuery(id+"F1.wireOp",EDGE,"6uq4eEBE-zqJi-hSKM-aljM-bMrpigbcLfnv");var subQ2=makeQuery(id+"F1.imprint","INTERSECT",VERTEX,{"derivedFrom":[subQ1,subQ0]});Q142=makeQuery(id+"F1.imprint","IMPRINT",FACE,{"disambiguationData":[TD([[makeQuery(id+"F1.imprint","IMPRINT",EDGE,{"disambiguationData":[TD([[subQ2,-1.0]])],"derivedFrom":subQ1}),-1.0]])]});}
            var Q143;
            {var subQ0=sQuery(id+"F1.wireOp",EDGE,"1122fb87-85ac-472b-868b-fc3012a12b32.4.0.1");var subQ1=sQuery(id+"F1.wireOp",EDGE,"6uq4eEBE-zqJi-hSKM-aljM-bMrpigbcLfnv");var subQ2=makeQuery(id+"F1.imprint","INTERSECT",VERTEX,{"derivedFrom":[subQ1,subQ0]});Q143=makeQuery(id+"F1.imprint","IMPRINT",FACE,{"disambiguationData":[TD([[makeQuery(id+"F1.imprint","IMPRINT",EDGE,{"disambiguationData":[TD([[subQ2,-1.0]])],"derivedFrom":subQ1}),-1.0]])]});}
            var Q144;
            {var subQ0=sQuery(id+"F1.wireOp",EDGE,"1122fb87-85ac-472b-868b-fc3012a12b32.9.0.0");var subQ1=sQuery(id+"F1.wireOp",EDGE,"6uq4eEBE-zqJi-hSKM-aljM-bMrpigbcLfnv");var subQ2=makeQuery(id+"F1.imprint","INTERSECT",VERTEX,{"derivedFrom":[subQ1,subQ0]});Q144=makeQuery(id+"F1.imprint","IMPRINT",FACE,{"disambiguationData":[TD([[makeQuery(id+"F1.imprint","IMPRINT",EDGE,{"disambiguationData":[TD([[subQ2,-1.0]])],"derivedFrom":subQ1}),-1.0]])]});}
            var Q145;
            {var subQ0=sQuery(id+"F1.wireOp",EDGE,"1122fb87-85ac-472b-868b-fc3012a12b32.4.0.0");var subQ1=sQuery(id+"F1.wireOp",EDGE,"6uq4eEBE-zqJi-hSKM-aljM-bMrpigbcLfnv");var subQ2=makeQuery(id+"F1.imprint","INTERSECT",VERTEX,{"derivedFrom":[subQ1,subQ0]});Q145=makeQuery(id+"F1.imprint","IMPRINT",FACE,{"disambiguationData":[TD([[makeQuery(id+"F1.imprint","IMPRINT",EDGE,{"disambiguationData":[TD([[subQ2,-1.0]])],"derivedFrom":subQ1}),-1.0]])]});}
            var Q146;
            {var subQ0=sQuery(id+"F1.wireOp",EDGE,"1122fb87-85ac-472b-868b-fc3012a12b32.5.0.1");var subQ1=sQuery(id+"F1.wireOp",EDGE,"6uq4eEBE-zqJi-hSKM-aljM-bMrpigbcLfnv");var subQ2=makeQuery(id+"F1.imprint","INTERSECT",VERTEX,{"derivedFrom":[subQ1,subQ0]});Q146=makeQuery(id+"F1.imprint","IMPRINT",FACE,{"disambiguationData":[TD([[makeQuery(id+"F1.imprint","IMPRINT",EDGE,{"disambiguationData":[TD([[subQ2,-1.0]])],"derivedFrom":subQ1}),-1.0]])]});}
            var Q147;
            {var subQ0=sQuery(id+"F1.wireOp",EDGE,"7UFrm05o-hojw-SgNx-ndEl-vP84DU8JNmmf");var subQ1=sQuery(id+"F1.wireOp",EDGE,"6uq4eEBE-zqJi-hSKM-aljM-bMrpigbcLfnv");var subQ2=makeQuery(id+"F1.imprint","INTERSECT",VERTEX,{"derivedFrom":[subQ1,subQ0]});Q147=makeQuery(id+"F1.imprint","IMPRINT",FACE,{"disambiguationData":[TD([[makeQuery(id+"F1.imprint","IMPRINT",EDGE,{"disambiguationData":[TD([[subQ2,-1.0]])],"derivedFrom":subQ1}),-1.0]])]});}
            var Q148;
            {var subQ0=sQuery(id+"F1.wireOp",EDGE,"1122fb87-85ac-472b-868b-fc3012a12b32.5.0.0");var subQ1=sQuery(id+"F1.wireOp",EDGE,"6uq4eEBE-zqJi-hSKM-aljM-bMrpigbcLfnv");var subQ2=makeQuery(id+"F1.imprint","INTERSECT",VERTEX,{"derivedFrom":[subQ1,subQ0]});Q148=makeQuery(id+"F1.imprint","IMPRINT",FACE,{"disambiguationData":[TD([[makeQuery(id+"F1.imprint","IMPRINT",EDGE,{"disambiguationData":[TD([[subQ2,-1.0]])],"derivedFrom":subQ1}),-1.0]])]});}
            var Q149;
            {var subQ0=sQuery(id+"F1.wireOp",EDGE,"WklholZw-bksS-AMq5-miGy-PiFPOaJ55qhu");var subQ1=sQuery(id+"F1.wireOp",EDGE,"6uq4eEBE-zqJi-hSKM-aljM-bMrpigbcLfnv");var subQ2=makeQuery(id+"F1.imprint","INTERSECT",VERTEX,{"derivedFrom":[subQ1,subQ0]});Q149=makeQuery(id+"F1.imprint","IMPRINT",FACE,{"disambiguationData":[TD([[makeQuery(id+"F1.imprint","IMPRINT",EDGE,{"disambiguationData":[TD([[subQ2,1.0]])],"derivedFrom":subQ1}),-1.0]])]});}
            var Q150;
            {var subQ0=sQuery(id+"F1.wireOp",EDGE,"1122fb87-85ac-472b-868b-fc3012a12b32.6.0.1");var subQ1=sQuery(id+"F1.wireOp",EDGE,"6uq4eEBE-zqJi-hSKM-aljM-bMrpigbcLfnv");var subQ2=makeQuery(id+"F1.imprint","INTERSECT",VERTEX,{"derivedFrom":[subQ1,subQ0]});Q150=makeQuery(id+"F1.imprint","IMPRINT",FACE,{"disambiguationData":[TD([[makeQuery(id+"F1.imprint","IMPRINT",EDGE,{"disambiguationData":[TD([[subQ2,-1.0]])],"derivedFrom":subQ1}),-1.0]])]});}
            var Q151;
            {var subQ0=sQuery(id+"F1.wireOp",EDGE,"1122fb87-85ac-472b-868b-fc3012a12b32.6.0.0");var subQ1=sQuery(id+"F1.wireOp",EDGE,"6uq4eEBE-zqJi-hSKM-aljM-bMrpigbcLfnv");var subQ2=makeQuery(id+"F1.imprint","INTERSECT",VERTEX,{"derivedFrom":[subQ1,subQ0]});Q151=makeQuery(id+"F1.imprint","IMPRINT",FACE,{"disambiguationData":[TD([[makeQuery(id+"F1.imprint","IMPRINT",EDGE,{"disambiguationData":[TD([[subQ2,-1.0]])],"derivedFrom":subQ1}),-1.0]])]});}
            var Q152;
            {var subQ0=sQuery(id+"F1.wireOp",EDGE,"1122fb87-85ac-472b-868b-fc3012a12b32.7.0.1");var subQ1=sQuery(id+"F1.wireOp",EDGE,"6uq4eEBE-zqJi-hSKM-aljM-bMrpigbcLfnv");var subQ2=makeQuery(id+"F1.imprint","INTERSECT",VERTEX,{"derivedFrom":[subQ1,subQ0]});Q152=makeQuery(id+"F1.imprint","IMPRINT",FACE,{"disambiguationData":[TD([[makeQuery(id+"F1.imprint","IMPRINT",EDGE,{"disambiguationData":[TD([[subQ2,-1.0]])],"derivedFrom":subQ1}),-1.0]])]});}
            var Q153;
            {var subQ0=sQuery(id+"F1.wireOp",EDGE,"1122fb87-85ac-472b-868b-fc3012a12b32.3.0.1");var subQ1=sQuery(id+"F1.wireOp",EDGE,"a13d30e3-1256-45f2-88c4-17f94fdc27e3.0.1.0");var subQ2=makeQuery(id+"F1.imprint","INTERSECT",VERTEX,{"derivedFrom":[subQ1,subQ0]});Q153=makeQuery(id+"F1.imprint","IMPRINT",FACE,{"disambiguationData":[TD([[makeQuery(id+"F1.imprint","IMPRINT",EDGE,{"disambiguationData":[TD([[subQ2,-1.0]])],"derivedFrom":subQ1}),-1.0]])]});}
            var Q154;
            {var subQ0=sQuery(id+"F1.wireOp",EDGE,"1122fb87-85ac-472b-868b-fc3012a12b32.2.0.0");var subQ1=sQuery(id+"F1.wireOp",EDGE,"a13d30e3-1256-45f2-88c4-17f94fdc27e3.0.1.0");var subQ2=makeQuery(id+"F1.imprint","INTERSECT",VERTEX,{"derivedFrom":[subQ1,subQ0]});Q154=makeQuery(id+"F1.imprint","IMPRINT",FACE,{"disambiguationData":[TD([[makeQuery(id+"F1.imprint","IMPRINT",EDGE,{"disambiguationData":[TD([[subQ2,-1.0]])],"derivedFrom":subQ1}),-1.0]])]});}
            var Q155;
            {var subQ0=sQuery(id+"F1.wireOp",EDGE,"1122fb87-85ac-472b-868b-fc3012a12b32.9.0.0");var subQ1=sQuery(id+"F1.wireOp",EDGE,"a13d30e3-1256-45f2-88c4-17f94fdc27e3.0.1.0");var subQ2=makeQuery(id+"F1.imprint","INTERSECT",VERTEX,{"derivedFrom":[subQ1,subQ0]});Q155=makeQuery(id+"F1.imprint","IMPRINT",FACE,{"disambiguationData":[TD([[makeQuery(id+"F1.imprint","IMPRINT",EDGE,{"disambiguationData":[TD([[subQ2,-1.0]])],"derivedFrom":subQ1}),-1.0]])]});}
            var Q156;
            {var subQ0=sQuery(id+"F1.wireOp",EDGE,"1122fb87-85ac-472b-868b-fc3012a12b32.3.0.0");var subQ1=sQuery(id+"F1.wireOp",EDGE,"a13d30e3-1256-45f2-88c4-17f94fdc27e3.0.1.0");var subQ2=makeQuery(id+"F1.imprint","INTERSECT",VERTEX,{"derivedFrom":[subQ1,subQ0]});Q156=makeQuery(id+"F1.imprint","IMPRINT",FACE,{"disambiguationData":[TD([[makeQuery(id+"F1.imprint","IMPRINT",EDGE,{"disambiguationData":[TD([[subQ2,-1.0]])],"derivedFrom":subQ1}),-1.0]])]});}
            var Q157;
            {var subQ0=sQuery(id+"F1.wireOp",EDGE,"WklholZw-bksS-AMq5-miGy-PiFPOaJ55qhu");var subQ1=sQuery(id+"F1.wireOp",EDGE,"a13d30e3-1256-45f2-88c4-17f94fdc27e3.0.1.0");var subQ2=makeQuery(id+"F1.imprint","INTERSECT",VERTEX,{"derivedFrom":[subQ1,subQ0]});Q157=makeQuery(id+"F1.imprint","IMPRINT",FACE,{"disambiguationData":[TD([[makeQuery(id+"F1.imprint","IMPRINT",EDGE,{"disambiguationData":[TD([[subQ2,1.0]])],"derivedFrom":subQ1}),-1.0]])]});}
            var Q158;
            {var subQ0=sQuery(id+"F1.wireOp",EDGE,"1122fb87-85ac-472b-868b-fc3012a12b32.4.0.1");var subQ1=sQuery(id+"F1.wireOp",EDGE,"a13d30e3-1256-45f2-88c4-17f94fdc27e3.0.1.0");var subQ2=makeQuery(id+"F1.imprint","INTERSECT",VERTEX,{"derivedFrom":[subQ1,subQ0]});Q158=makeQuery(id+"F1.imprint","IMPRINT",FACE,{"disambiguationData":[TD([[makeQuery(id+"F1.imprint","IMPRINT",EDGE,{"disambiguationData":[TD([[subQ2,-1.0]])],"derivedFrom":subQ1}),-1.0]])]});}
            var Q159;
            {var subQ0=sQuery(id+"F1.wireOp",EDGE,"1122fb87-85ac-472b-868b-fc3012a12b32.4.0.0");var subQ1=sQuery(id+"F1.wireOp",EDGE,"a13d30e3-1256-45f2-88c4-17f94fdc27e3.0.1.0");var subQ2=makeQuery(id+"F1.imprint","INTERSECT",VERTEX,{"derivedFrom":[subQ1,subQ0]});Q159=makeQuery(id+"F1.imprint","IMPRINT",FACE,{"disambiguationData":[TD([[makeQuery(id+"F1.imprint","IMPRINT",EDGE,{"disambiguationData":[TD([[subQ2,-1.0]])],"derivedFrom":subQ1}),-1.0]])]});}
            var Q160;
            {var subQ0=sQuery(id+"F1.wireOp",EDGE,"1122fb87-85ac-472b-868b-fc3012a12b32.5.0.1");var subQ1=sQuery(id+"F1.wireOp",EDGE,"a13d30e3-1256-45f2-88c4-17f94fdc27e3.0.1.0");var subQ2=makeQuery(id+"F1.imprint","INTERSECT",VERTEX,{"derivedFrom":[subQ1,subQ0]});Q160=makeQuery(id+"F1.imprint","IMPRINT",FACE,{"disambiguationData":[TD([[makeQuery(id+"F1.imprint","IMPRINT",EDGE,{"disambiguationData":[TD([[subQ2,-1.0]])],"derivedFrom":subQ1}),-1.0]])]});}
            var Q161;
            {var subQ0=sQuery(id+"F1.wireOp",EDGE,"1122fb87-85ac-472b-868b-fc3012a12b32.5.0.0");var subQ1=sQuery(id+"F1.wireOp",EDGE,"a13d30e3-1256-45f2-88c4-17f94fdc27e3.0.1.0");var subQ2=makeQuery(id+"F1.imprint","INTERSECT",VERTEX,{"derivedFrom":[subQ1,subQ0]});Q161=makeQuery(id+"F1.imprint","IMPRINT",FACE,{"disambiguationData":[TD([[makeQuery(id+"F1.imprint","IMPRINT",EDGE,{"disambiguationData":[TD([[subQ2,-1.0]])],"derivedFrom":subQ1}),-1.0]])]});}
            var Q162;
            {var subQ0=sQuery(id+"F1.wireOp",EDGE,"1122fb87-85ac-472b-868b-fc3012a12b32.6.0.1");var subQ1=sQuery(id+"F1.wireOp",EDGE,"a13d30e3-1256-45f2-88c4-17f94fdc27e3.0.1.0");var subQ2=makeQuery(id+"F1.imprint","INTERSECT",VERTEX,{"derivedFrom":[subQ1,subQ0]});Q162=makeQuery(id+"F1.imprint","IMPRINT",FACE,{"disambiguationData":[TD([[makeQuery(id+"F1.imprint","IMPRINT",EDGE,{"disambiguationData":[TD([[subQ2,-1.0]])],"derivedFrom":subQ1}),-1.0]])]});}
            var Q163;
            {var subQ0=sQuery(id+"F1.wireOp",EDGE,"1122fb87-85ac-472b-868b-fc3012a12b32.6.0.0");var subQ1=sQuery(id+"F1.wireOp",EDGE,"a13d30e3-1256-45f2-88c4-17f94fdc27e3.0.1.0");var subQ2=makeQuery(id+"F1.imprint","INTERSECT",VERTEX,{"derivedFrom":[subQ1,subQ0]});Q163=makeQuery(id+"F1.imprint","IMPRINT",FACE,{"disambiguationData":[TD([[makeQuery(id+"F1.imprint","IMPRINT",EDGE,{"disambiguationData":[TD([[subQ2,-1.0]])],"derivedFrom":subQ1}),-1.0]])]});}
            var Q164;
            {var subQ0=sQuery(id+"F1.wireOp",EDGE,"1122fb87-85ac-472b-868b-fc3012a12b32.7.0.1");var subQ1=sQuery(id+"F1.wireOp",EDGE,"a13d30e3-1256-45f2-88c4-17f94fdc27e3.0.1.0");var subQ2=makeQuery(id+"F1.imprint","INTERSECT",VERTEX,{"derivedFrom":[subQ1,subQ0]});Q164=makeQuery(id+"F1.imprint","IMPRINT",FACE,{"disambiguationData":[TD([[makeQuery(id+"F1.imprint","IMPRINT",EDGE,{"disambiguationData":[TD([[subQ2,-1.0]])],"derivedFrom":subQ1}),-1.0]])]});}
            var Q165;
            {var subQ0=sQuery(id+"F1.wireOp",EDGE,"1122fb87-85ac-472b-868b-fc3012a12b32.7.0.0");var subQ1=sQuery(id+"F1.wireOp",EDGE,"a13d30e3-1256-45f2-88c4-17f94fdc27e3.0.1.0");var subQ2=makeQuery(id+"F1.imprint","INTERSECT",VERTEX,{"derivedFrom":[subQ1,subQ0]});Q165=makeQuery(id+"F1.imprint","IMPRINT",FACE,{"disambiguationData":[TD([[makeQuery(id+"F1.imprint","IMPRINT",EDGE,{"disambiguationData":[TD([[subQ2,-1.0]])],"derivedFrom":subQ1}),-1.0]])]});}
            var Q166;
            {var subQ0=sQuery(id+"F1.wireOp",EDGE,"9AYXCysi-gJ8l-qpYG-XvAO-eWvyKQmG9Npc");var subQ1=sQuery(id+"F1.wireOp",EDGE,"a13d30e3-1256-45f2-88c4-17f94fdc27e3.0.1.0");var subQ2=makeQuery(id+"F1.imprint","INTERSECT",VERTEX,{"derivedFrom":[subQ1,subQ0]});Q166=makeQuery(id+"F1.imprint","IMPRINT",FACE,{"disambiguationData":[TD([[makeQuery(id+"F1.imprint","IMPRINT",EDGE,{"disambiguationData":[TD([[subQ2,-1.0]])],"derivedFrom":subQ1}),-1.0]])]});}
            var Q167;
            {var subQ0=sQuery(id+"F1.wireOp",EDGE,"7UFrm05o-hojw-SgNx-ndEl-vP84DU8JNmmf");var subQ1=sQuery(id+"F1.wireOp",EDGE,"a13d30e3-1256-45f2-88c4-17f94fdc27e3.0.1.0");var subQ2=makeQuery(id+"F1.imprint","INTERSECT",VERTEX,{"derivedFrom":[subQ1,subQ0]});Q167=makeQuery(id+"F1.imprint","IMPRINT",FACE,{"disambiguationData":[TD([[makeQuery(id+"F1.imprint","IMPRINT",EDGE,{"disambiguationData":[TD([[subQ2,-1.0]])],"derivedFrom":subQ1}),-1.0]])]});}
            var Q168;
            {var subQ0=sQuery(id+"F1.wireOp",EDGE,"9AYXCysi-gJ8l-qpYG-XvAO-eWvyKQmG9Npc");var subQ1=sQuery(id+"F1.wireOp",EDGE,"a13d30e3-1256-45f2-88c4-17f94fdc27e3.0.2.0");var subQ2=makeQuery(id+"F1.imprint","INTERSECT",VERTEX,{"derivedFrom":[subQ1,subQ0]});Q168=makeQuery(id+"F1.imprint","IMPRINT",FACE,{"disambiguationData":[TD([[makeQuery(id+"F1.imprint","IMPRINT",EDGE,{"disambiguationData":[TD([[subQ2,-1.0]])],"derivedFrom":subQ1}),-1.0]])]});}
            var Q169;
            {var subQ0=sQuery(id+"F1.wireOp",EDGE,"1122fb87-85ac-472b-868b-fc3012a12b32.7.0.1");var subQ1=sQuery(id+"F1.wireOp",EDGE,"a13d30e3-1256-45f2-88c4-17f94fdc27e3.0.2.0");var subQ2=makeQuery(id+"F1.imprint","INTERSECT",VERTEX,{"derivedFrom":[subQ1,subQ0]});Q169=makeQuery(id+"F1.imprint","IMPRINT",FACE,{"disambiguationData":[TD([[makeQuery(id+"F1.imprint","IMPRINT",EDGE,{"disambiguationData":[TD([[subQ2,-1.0]])],"derivedFrom":subQ1}),-1.0]])]});}
            var Q170;
            {var subQ0=sQuery(id+"F1.wireOp",EDGE,"1122fb87-85ac-472b-868b-fc3012a12b32.6.0.1");var subQ1=sQuery(id+"F1.wireOp",EDGE,"a13d30e3-1256-45f2-88c4-17f94fdc27e3.0.2.0");var subQ2=makeQuery(id+"F1.imprint","INTERSECT",VERTEX,{"derivedFrom":[subQ1,subQ0]});Q170=makeQuery(id+"F1.imprint","IMPRINT",FACE,{"disambiguationData":[TD([[makeQuery(id+"F1.imprint","IMPRINT",EDGE,{"disambiguationData":[TD([[subQ2,-1.0]])],"derivedFrom":subQ1}),-1.0]])]});}
            var Q171;
            {var subQ0=sQuery(id+"F1.wireOp",EDGE,"1122fb87-85ac-472b-868b-fc3012a12b32.7.0.0");var subQ1=sQuery(id+"F1.wireOp",EDGE,"a13d30e3-1256-45f2-88c4-17f94fdc27e3.0.2.0");var subQ2=makeQuery(id+"F1.imprint","INTERSECT",VERTEX,{"derivedFrom":[subQ1,subQ0]});Q171=makeQuery(id+"F1.imprint","IMPRINT",FACE,{"disambiguationData":[TD([[makeQuery(id+"F1.imprint","IMPRINT",EDGE,{"disambiguationData":[TD([[subQ2,-1.0]])],"derivedFrom":subQ1}),-1.0]])]});}
            var Q172;
            {var subQ0=sQuery(id+"F1.wireOp",EDGE,"1122fb87-85ac-472b-868b-fc3012a12b32.6.0.0");var subQ1=sQuery(id+"F1.wireOp",EDGE,"a13d30e3-1256-45f2-88c4-17f94fdc27e3.0.2.0");var subQ2=makeQuery(id+"F1.imprint","INTERSECT",VERTEX,{"derivedFrom":[subQ1,subQ0]});Q172=makeQuery(id+"F1.imprint","IMPRINT",FACE,{"disambiguationData":[TD([[makeQuery(id+"F1.imprint","IMPRINT",EDGE,{"disambiguationData":[TD([[subQ2,-1.0]])],"derivedFrom":subQ1}),-1.0]])]});}
            var Q173;
            {var subQ0=sQuery(id+"F1.wireOp",EDGE,"1122fb87-85ac-472b-868b-fc3012a12b32.5.0.0");var subQ1=sQuery(id+"F1.wireOp",EDGE,"a13d30e3-1256-45f2-88c4-17f94fdc27e3.0.2.0");var subQ2=makeQuery(id+"F1.imprint","INTERSECT",VERTEX,{"derivedFrom":[subQ1,subQ0]});Q173=makeQuery(id+"F1.imprint","IMPRINT",FACE,{"disambiguationData":[TD([[makeQuery(id+"F1.imprint","IMPRINT",EDGE,{"disambiguationData":[TD([[subQ2,-1.0]])],"derivedFrom":subQ1}),-1.0]])]});}
            var Q174;
            {var subQ0=sQuery(id+"F1.wireOp",EDGE,"7UFrm05o-hojw-SgNx-ndEl-vP84DU8JNmmf");var subQ1=sQuery(id+"F1.wireOp",EDGE,"a13d30e3-1256-45f2-88c4-17f94fdc27e3.0.2.0");var subQ2=makeQuery(id+"F1.imprint","INTERSECT",VERTEX,{"derivedFrom":[subQ1,subQ0]});Q174=makeQuery(id+"F1.imprint","IMPRINT",FACE,{"disambiguationData":[TD([[makeQuery(id+"F1.imprint","IMPRINT",EDGE,{"disambiguationData":[TD([[subQ2,-1.0]])],"derivedFrom":subQ1}),-1.0]])]});}
            var Q175;
            {var subQ0=sQuery(id+"F1.wireOp",EDGE,"1122fb87-85ac-472b-868b-fc3012a12b32.9.0.0");var subQ1=sQuery(id+"F1.wireOp",EDGE,"a13d30e3-1256-45f2-88c4-17f94fdc27e3.0.2.0");var subQ2=makeQuery(id+"F1.imprint","INTERSECT",VERTEX,{"derivedFrom":[subQ1,subQ0]});Q175=makeQuery(id+"F1.imprint","IMPRINT",FACE,{"disambiguationData":[TD([[makeQuery(id+"F1.imprint","IMPRINT",EDGE,{"disambiguationData":[TD([[subQ2,-1.0]])],"derivedFrom":subQ1}),-1.0]])]});}
            var Q176;
            {var subQ0=sQuery(id+"F1.wireOp",EDGE,"WklholZw-bksS-AMq5-miGy-PiFPOaJ55qhu");var subQ1=sQuery(id+"F1.wireOp",EDGE,"a13d30e3-1256-45f2-88c4-17f94fdc27e3.0.2.0");var subQ2=makeQuery(id+"F1.imprint","INTERSECT",VERTEX,{"derivedFrom":[subQ1,subQ0]});Q176=makeQuery(id+"F1.imprint","IMPRINT",FACE,{"disambiguationData":[TD([[makeQuery(id+"F1.imprint","IMPRINT",EDGE,{"disambiguationData":[TD([[subQ2,1.0]])],"derivedFrom":subQ1}),-1.0]])]});}
            var Q177;
            {var subQ0=sQuery(id+"F1.wireOp",EDGE,"1122fb87-85ac-472b-868b-fc3012a12b32.2.0.0");var subQ1=sQuery(id+"F1.wireOp",EDGE,"a13d30e3-1256-45f2-88c4-17f94fdc27e3.0.2.0");var subQ2=makeQuery(id+"F1.imprint","INTERSECT",VERTEX,{"derivedFrom":[subQ1,subQ0]});Q177=makeQuery(id+"F1.imprint","IMPRINT",FACE,{"disambiguationData":[TD([[makeQuery(id+"F1.imprint","IMPRINT",EDGE,{"disambiguationData":[TD([[subQ2,-1.0]])],"derivedFrom":subQ1}),-1.0]])]});}
            var Q178;
            {var subQ0=sQuery(id+"F1.wireOp",EDGE,"1122fb87-85ac-472b-868b-fc3012a12b32.3.0.1");var subQ1=sQuery(id+"F1.wireOp",EDGE,"a13d30e3-1256-45f2-88c4-17f94fdc27e3.0.2.0");var subQ2=makeQuery(id+"F1.imprint","INTERSECT",VERTEX,{"derivedFrom":[subQ1,subQ0]});Q178=makeQuery(id+"F1.imprint","IMPRINT",FACE,{"disambiguationData":[TD([[makeQuery(id+"F1.imprint","IMPRINT",EDGE,{"disambiguationData":[TD([[subQ2,-1.0]])],"derivedFrom":subQ1}),-1.0]])]});}
            var Q179;
            {var subQ0=sQuery(id+"F1.wireOp",EDGE,"1122fb87-85ac-472b-868b-fc3012a12b32.3.0.0");var subQ1=sQuery(id+"F1.wireOp",EDGE,"a13d30e3-1256-45f2-88c4-17f94fdc27e3.0.2.0");var subQ2=makeQuery(id+"F1.imprint","INTERSECT",VERTEX,{"derivedFrom":[subQ1,subQ0]});Q179=makeQuery(id+"F1.imprint","IMPRINT",FACE,{"disambiguationData":[TD([[makeQuery(id+"F1.imprint","IMPRINT",EDGE,{"disambiguationData":[TD([[subQ2,-1.0]])],"derivedFrom":subQ1}),-1.0]])]});}
            var Q180;
            {var subQ0=sQuery(id+"F1.wireOp",EDGE,"1122fb87-85ac-472b-868b-fc3012a12b32.4.0.1");var subQ1=sQuery(id+"F1.wireOp",EDGE,"a13d30e3-1256-45f2-88c4-17f94fdc27e3.0.2.0");var subQ2=makeQuery(id+"F1.imprint","INTERSECT",VERTEX,{"derivedFrom":[subQ1,subQ0]});Q180=makeQuery(id+"F1.imprint","IMPRINT",FACE,{"disambiguationData":[TD([[makeQuery(id+"F1.imprint","IMPRINT",EDGE,{"disambiguationData":[TD([[subQ2,-1.0]])],"derivedFrom":subQ1}),-1.0]])]});}
            var Q181;
            {var subQ0=sQuery(id+"F1.wireOp",EDGE,"1122fb87-85ac-472b-868b-fc3012a12b32.4.0.0");var subQ1=sQuery(id+"F1.wireOp",EDGE,"a13d30e3-1256-45f2-88c4-17f94fdc27e3.0.2.0");var subQ2=makeQuery(id+"F1.imprint","INTERSECT",VERTEX,{"derivedFrom":[subQ1,subQ0]});Q181=makeQuery(id+"F1.imprint","IMPRINT",FACE,{"disambiguationData":[TD([[makeQuery(id+"F1.imprint","IMPRINT",EDGE,{"disambiguationData":[TD([[subQ2,-1.0]])],"derivedFrom":subQ1}),-1.0]])]});}
            var Q182;
            {var subQ0=sQuery(id+"F1.wireOp",EDGE,"1122fb87-85ac-472b-868b-fc3012a12b32.5.0.1");var subQ1=sQuery(id+"F1.wireOp",EDGE,"a13d30e3-1256-45f2-88c4-17f94fdc27e3.0.2.0");var subQ2=makeQuery(id+"F1.imprint","INTERSECT",VERTEX,{"derivedFrom":[subQ1,subQ0]});Q182=makeQuery(id+"F1.imprint","IMPRINT",FACE,{"disambiguationData":[TD([[makeQuery(id+"F1.imprint","IMPRINT",EDGE,{"disambiguationData":[TD([[subQ2,-1.0]])],"derivedFrom":subQ1}),-1.0]])]});}
            var Q183;
            {var subQ0=sQuery(id+"F1.wireOp",EDGE,"1122fb87-85ac-472b-868b-fc3012a12b32.9.0.0");var subQ1=sQuery(id+"F1.wireOp",EDGE,"a13d30e3-1256-45f2-88c4-17f94fdc27e3.0.3.0");var subQ2=makeQuery(id+"F1.imprint","INTERSECT",VERTEX,{"derivedFrom":[subQ1,subQ0]});Q183=makeQuery(id+"F1.imprint","IMPRINT",FACE,{"disambiguationData":[TD([[makeQuery(id+"F1.imprint","IMPRINT",EDGE,{"disambiguationData":[TD([[subQ2,-1.0]])],"derivedFrom":subQ1}),-1.0]])]});}
            var Q184;
            {var subQ0=sQuery(id+"F1.wireOp",EDGE,"1122fb87-85ac-472b-868b-fc3012a12b32.3.0.1");var subQ1=sQuery(id+"F1.wireOp",EDGE,"a13d30e3-1256-45f2-88c4-17f94fdc27e3.0.3.0");var subQ2=makeQuery(id+"F1.imprint","INTERSECT",VERTEX,{"derivedFrom":[subQ1,subQ0]});Q184=makeQuery(id+"F1.imprint","IMPRINT",FACE,{"disambiguationData":[TD([[makeQuery(id+"F1.imprint","IMPRINT",EDGE,{"disambiguationData":[TD([[subQ2,-1.0]])],"derivedFrom":subQ1}),-1.0]])]});}
            var Q185;
            {var subQ0=sQuery(id+"F1.wireOp",EDGE,"1122fb87-85ac-472b-868b-fc3012a12b32.2.0.0");var subQ1=sQuery(id+"F1.wireOp",EDGE,"a13d30e3-1256-45f2-88c4-17f94fdc27e3.0.3.0");var subQ2=makeQuery(id+"F1.imprint","INTERSECT",VERTEX,{"derivedFrom":[subQ1,subQ0]});Q185=makeQuery(id+"F1.imprint","IMPRINT",FACE,{"disambiguationData":[TD([[makeQuery(id+"F1.imprint","IMPRINT",EDGE,{"disambiguationData":[TD([[subQ2,-1.0]])],"derivedFrom":subQ1}),-1.0]])]});}
            var Q186;
            {var subQ0=sQuery(id+"F1.wireOp",EDGE,"1122fb87-85ac-472b-868b-fc3012a12b32.3.0.0");var subQ1=sQuery(id+"F1.wireOp",EDGE,"a13d30e3-1256-45f2-88c4-17f94fdc27e3.0.3.0");var subQ2=makeQuery(id+"F1.imprint","INTERSECT",VERTEX,{"derivedFrom":[subQ1,subQ0]});Q186=makeQuery(id+"F1.imprint","IMPRINT",FACE,{"disambiguationData":[TD([[makeQuery(id+"F1.imprint","IMPRINT",EDGE,{"disambiguationData":[TD([[subQ2,-1.0]])],"derivedFrom":subQ1}),-1.0]])]});}
            var Q187;
            {var subQ0=sQuery(id+"F1.wireOp",EDGE,"WklholZw-bksS-AMq5-miGy-PiFPOaJ55qhu");var subQ1=sQuery(id+"F1.wireOp",EDGE,"a13d30e3-1256-45f2-88c4-17f94fdc27e3.0.3.0");var subQ2=makeQuery(id+"F1.imprint","INTERSECT",VERTEX,{"derivedFrom":[subQ1,subQ0]});Q187=makeQuery(id+"F1.imprint","IMPRINT",FACE,{"disambiguationData":[TD([[makeQuery(id+"F1.imprint","IMPRINT",EDGE,{"disambiguationData":[TD([[subQ2,1.0]])],"derivedFrom":subQ1}),-1.0]])]});}
            var Q188;
            {var subQ0=sQuery(id+"F1.wireOp",EDGE,"1122fb87-85ac-472b-868b-fc3012a12b32.4.0.1");var subQ1=sQuery(id+"F1.wireOp",EDGE,"a13d30e3-1256-45f2-88c4-17f94fdc27e3.0.3.0");var subQ2=makeQuery(id+"F1.imprint","INTERSECT",VERTEX,{"derivedFrom":[subQ1,subQ0]});Q188=makeQuery(id+"F1.imprint","IMPRINT",FACE,{"disambiguationData":[TD([[makeQuery(id+"F1.imprint","IMPRINT",EDGE,{"disambiguationData":[TD([[subQ2,-1.0]])],"derivedFrom":subQ1}),-1.0]])]});}
            var Q189;
            {var subQ0=sQuery(id+"F1.wireOp",EDGE,"1122fb87-85ac-472b-868b-fc3012a12b32.4.0.0");var subQ1=sQuery(id+"F1.wireOp",EDGE,"a13d30e3-1256-45f2-88c4-17f94fdc27e3.0.3.0");var subQ2=makeQuery(id+"F1.imprint","INTERSECT",VERTEX,{"derivedFrom":[subQ1,subQ0]});Q189=makeQuery(id+"F1.imprint","IMPRINT",FACE,{"disambiguationData":[TD([[makeQuery(id+"F1.imprint","IMPRINT",EDGE,{"disambiguationData":[TD([[subQ2,-1.0]])],"derivedFrom":subQ1}),-1.0]])]});}
            var Q190;
            {var subQ0=sQuery(id+"F1.wireOp",EDGE,"1122fb87-85ac-472b-868b-fc3012a12b32.5.0.1");var subQ1=sQuery(id+"F1.wireOp",EDGE,"a13d30e3-1256-45f2-88c4-17f94fdc27e3.0.3.0");var subQ2=makeQuery(id+"F1.imprint","INTERSECT",VERTEX,{"derivedFrom":[subQ1,subQ0]});Q190=makeQuery(id+"F1.imprint","IMPRINT",FACE,{"disambiguationData":[TD([[makeQuery(id+"F1.imprint","IMPRINT",EDGE,{"disambiguationData":[TD([[subQ2,-1.0]])],"derivedFrom":subQ1}),-1.0]])]});}
            var Q191;
            {var subQ0=sQuery(id+"F1.wireOp",EDGE,"1122fb87-85ac-472b-868b-fc3012a12b32.5.0.0");var subQ1=sQuery(id+"F1.wireOp",EDGE,"a13d30e3-1256-45f2-88c4-17f94fdc27e3.0.3.0");var subQ2=makeQuery(id+"F1.imprint","INTERSECT",VERTEX,{"derivedFrom":[subQ1,subQ0]});Q191=makeQuery(id+"F1.imprint","IMPRINT",FACE,{"disambiguationData":[TD([[makeQuery(id+"F1.imprint","IMPRINT",EDGE,{"disambiguationData":[TD([[subQ2,-1.0]])],"derivedFrom":subQ1}),-1.0]])]});}
            var Q192;
            {var subQ0=sQuery(id+"F1.wireOp",EDGE,"1122fb87-85ac-472b-868b-fc3012a12b32.6.0.1");var subQ1=sQuery(id+"F1.wireOp",EDGE,"a13d30e3-1256-45f2-88c4-17f94fdc27e3.0.3.0");var subQ2=makeQuery(id+"F1.imprint","INTERSECT",VERTEX,{"derivedFrom":[subQ1,subQ0]});Q192=makeQuery(id+"F1.imprint","IMPRINT",FACE,{"disambiguationData":[TD([[makeQuery(id+"F1.imprint","IMPRINT",EDGE,{"disambiguationData":[TD([[subQ2,-1.0]])],"derivedFrom":subQ1}),-1.0]])]});}
            var Q193;
            {var subQ0=sQuery(id+"F1.wireOp",EDGE,"1122fb87-85ac-472b-868b-fc3012a12b32.6.0.0");var subQ1=sQuery(id+"F1.wireOp",EDGE,"a13d30e3-1256-45f2-88c4-17f94fdc27e3.0.3.0");var subQ2=makeQuery(id+"F1.imprint","INTERSECT",VERTEX,{"derivedFrom":[subQ1,subQ0]});Q193=makeQuery(id+"F1.imprint","IMPRINT",FACE,{"disambiguationData":[TD([[makeQuery(id+"F1.imprint","IMPRINT",EDGE,{"disambiguationData":[TD([[subQ2,-1.0]])],"derivedFrom":subQ1}),-1.0]])]});}
            var Q194;
            {var subQ0=sQuery(id+"F1.wireOp",EDGE,"1122fb87-85ac-472b-868b-fc3012a12b32.7.0.1");var subQ1=sQuery(id+"F1.wireOp",EDGE,"a13d30e3-1256-45f2-88c4-17f94fdc27e3.0.3.0");var subQ2=makeQuery(id+"F1.imprint","INTERSECT",VERTEX,{"derivedFrom":[subQ1,subQ0]});Q194=makeQuery(id+"F1.imprint","IMPRINT",FACE,{"disambiguationData":[TD([[makeQuery(id+"F1.imprint","IMPRINT",EDGE,{"disambiguationData":[TD([[subQ2,-1.0]])],"derivedFrom":subQ1}),-1.0]])]});}
            var Q195;
            {var subQ0=sQuery(id+"F1.wireOp",EDGE,"1122fb87-85ac-472b-868b-fc3012a12b32.7.0.0");var subQ1=sQuery(id+"F1.wireOp",EDGE,"a13d30e3-1256-45f2-88c4-17f94fdc27e3.0.3.0");var subQ2=makeQuery(id+"F1.imprint","INTERSECT",VERTEX,{"derivedFrom":[subQ1,subQ0]});Q195=makeQuery(id+"F1.imprint","IMPRINT",FACE,{"disambiguationData":[TD([[makeQuery(id+"F1.imprint","IMPRINT",EDGE,{"disambiguationData":[TD([[subQ2,-1.0]])],"derivedFrom":subQ1}),-1.0]])]});}
            var Q196;
            {var subQ0=sQuery(id+"F1.wireOp",EDGE,"9AYXCysi-gJ8l-qpYG-XvAO-eWvyKQmG9Npc");var subQ1=sQuery(id+"F1.wireOp",EDGE,"a13d30e3-1256-45f2-88c4-17f94fdc27e3.0.3.0");var subQ2=makeQuery(id+"F1.imprint","INTERSECT",VERTEX,{"derivedFrom":[subQ1,subQ0]});Q196=makeQuery(id+"F1.imprint","IMPRINT",FACE,{"disambiguationData":[TD([[makeQuery(id+"F1.imprint","IMPRINT",EDGE,{"disambiguationData":[TD([[subQ2,-1.0]])],"derivedFrom":subQ1}),-1.0]])]});}
            var Q197;
            {var subQ0=sQuery(id+"F1.wireOp",EDGE,"7UFrm05o-hojw-SgNx-ndEl-vP84DU8JNmmf");var subQ1=sQuery(id+"F1.wireOp",EDGE,"a13d30e3-1256-45f2-88c4-17f94fdc27e3.0.3.0");var subQ2=makeQuery(id+"F1.imprint","INTERSECT",VERTEX,{"derivedFrom":[subQ1,subQ0]});Q197=makeQuery(id+"F1.imprint","IMPRINT",FACE,{"disambiguationData":[TD([[makeQuery(id+"F1.imprint","IMPRINT",EDGE,{"disambiguationData":[TD([[subQ2,-1.0]])],"derivedFrom":subQ1}),-1.0]])]});}
            var Q198;
            {var subQ0=sQuery(id+"F1.wireOp",EDGE,"1122fb87-85ac-472b-868b-fc3012a12b32.6.0.0");var subQ1=sQuery(id+"F1.wireOp",EDGE,"a13d30e3-1256-45f2-88c4-17f94fdc27e3.0.4.0");var subQ2=makeQuery(id+"F1.imprint","INTERSECT",VERTEX,{"derivedFrom":[subQ1,subQ0]});Q198=makeQuery(id+"F1.imprint","IMPRINT",FACE,{"disambiguationData":[TD([[makeQuery(id+"F1.imprint","IMPRINT",EDGE,{"disambiguationData":[TD([[subQ2,-1.0]])],"derivedFrom":subQ1}),-1.0]])]});}
            var Q199;
            {var subQ0=sQuery(id+"F1.wireOp",EDGE,"1122fb87-85ac-472b-868b-fc3012a12b32.7.0.1");var subQ1=sQuery(id+"F1.wireOp",EDGE,"a13d30e3-1256-45f2-88c4-17f94fdc27e3.0.4.0");var subQ2=makeQuery(id+"F1.imprint","INTERSECT",VERTEX,{"derivedFrom":[subQ1,subQ0]});Q199=makeQuery(id+"F1.imprint","IMPRINT",FACE,{"disambiguationData":[TD([[makeQuery(id+"F1.imprint","IMPRINT",EDGE,{"disambiguationData":[TD([[subQ2,-1.0]])],"derivedFrom":subQ1}),-1.0]])]});}
            var Q200;
            {var subQ0=sQuery(id+"F1.wireOp",EDGE,"9AYXCysi-gJ8l-qpYG-XvAO-eWvyKQmG9Npc");var subQ1=sQuery(id+"F1.wireOp",EDGE,"a13d30e3-1256-45f2-88c4-17f94fdc27e3.0.4.0");var subQ2=makeQuery(id+"F1.imprint","INTERSECT",VERTEX,{"derivedFrom":[subQ1,subQ0]});Q200=makeQuery(id+"F1.imprint","IMPRINT",FACE,{"disambiguationData":[TD([[makeQuery(id+"F1.imprint","IMPRINT",EDGE,{"disambiguationData":[TD([[subQ2,-1.0]])],"derivedFrom":subQ1}),-1.0]])]});}
            var Q201;
            {var subQ0=sQuery(id+"F1.wireOp",EDGE,"7UFrm05o-hojw-SgNx-ndEl-vP84DU8JNmmf");var subQ1=sQuery(id+"F1.wireOp",EDGE,"a13d30e3-1256-45f2-88c4-17f94fdc27e3.0.4.0");var subQ2=makeQuery(id+"F1.imprint","INTERSECT",VERTEX,{"derivedFrom":[subQ1,subQ0]});Q201=makeQuery(id+"F1.imprint","IMPRINT",FACE,{"disambiguationData":[TD([[makeQuery(id+"F1.imprint","IMPRINT",EDGE,{"disambiguationData":[TD([[subQ2,-1.0]])],"derivedFrom":subQ1}),-1.0]])]});}
            var Q202;
            {var subQ0=sQuery(id+"F1.wireOp",EDGE,"1122fb87-85ac-472b-868b-fc3012a12b32.6.0.1");var subQ1=sQuery(id+"F1.wireOp",EDGE,"a13d30e3-1256-45f2-88c4-17f94fdc27e3.0.4.0");var subQ2=makeQuery(id+"F1.imprint","INTERSECT",VERTEX,{"derivedFrom":[subQ1,subQ0]});Q202=makeQuery(id+"F1.imprint","IMPRINT",FACE,{"disambiguationData":[TD([[makeQuery(id+"F1.imprint","IMPRINT",EDGE,{"disambiguationData":[TD([[subQ2,-1.0]])],"derivedFrom":subQ1}),-1.0]])]});}
            var Q203;
            {var subQ0=sQuery(id+"F1.wireOp",EDGE,"1122fb87-85ac-472b-868b-fc3012a12b32.7.0.0");var subQ1=sQuery(id+"F1.wireOp",EDGE,"a13d30e3-1256-45f2-88c4-17f94fdc27e3.0.4.0");var subQ2=makeQuery(id+"F1.imprint","INTERSECT",VERTEX,{"derivedFrom":[subQ1,subQ0]});Q203=makeQuery(id+"F1.imprint","IMPRINT",FACE,{"disambiguationData":[TD([[makeQuery(id+"F1.imprint","IMPRINT",EDGE,{"disambiguationData":[TD([[subQ2,-1.0]])],"derivedFrom":subQ1}),-1.0]])]});}
            var Q204;
            {var subQ0=sQuery(id+"F1.wireOp",EDGE,"1122fb87-85ac-472b-868b-fc3012a12b32.9.0.0");var subQ1=sQuery(id+"F1.wireOp",EDGE,"a13d30e3-1256-45f2-88c4-17f94fdc27e3.0.4.0");var subQ2=makeQuery(id+"F1.imprint","INTERSECT",VERTEX,{"derivedFrom":[subQ1,subQ0]});Q204=makeQuery(id+"F1.imprint","IMPRINT",FACE,{"disambiguationData":[TD([[makeQuery(id+"F1.imprint","IMPRINT",EDGE,{"disambiguationData":[TD([[subQ2,-1.0]])],"derivedFrom":subQ1}),-1.0]])]});}
            var Q205;
            {var subQ0=sQuery(id+"F1.wireOp",EDGE,"WklholZw-bksS-AMq5-miGy-PiFPOaJ55qhu");var subQ1=sQuery(id+"F1.wireOp",EDGE,"a13d30e3-1256-45f2-88c4-17f94fdc27e3.0.4.0");var subQ2=makeQuery(id+"F1.imprint","INTERSECT",VERTEX,{"derivedFrom":[subQ1,subQ0]});Q205=makeQuery(id+"F1.imprint","IMPRINT",FACE,{"disambiguationData":[TD([[makeQuery(id+"F1.imprint","IMPRINT",EDGE,{"disambiguationData":[TD([[subQ2,1.0]])],"derivedFrom":subQ1}),-1.0]])]});}
            var Q206;
            {var subQ0=sQuery(id+"F1.wireOp",EDGE,"1122fb87-85ac-472b-868b-fc3012a12b32.2.0.0");var subQ1=sQuery(id+"F1.wireOp",EDGE,"a13d30e3-1256-45f2-88c4-17f94fdc27e3.0.4.0");var subQ2=makeQuery(id+"F1.imprint","INTERSECT",VERTEX,{"derivedFrom":[subQ1,subQ0]});Q206=makeQuery(id+"F1.imprint","IMPRINT",FACE,{"disambiguationData":[TD([[makeQuery(id+"F1.imprint","IMPRINT",EDGE,{"disambiguationData":[TD([[subQ2,-1.0]])],"derivedFrom":subQ1}),-1.0]])]});}
            var Q207;
            {var subQ0=sQuery(id+"F1.wireOp",EDGE,"1122fb87-85ac-472b-868b-fc3012a12b32.3.0.1");var subQ1=sQuery(id+"F1.wireOp",EDGE,"a13d30e3-1256-45f2-88c4-17f94fdc27e3.0.4.0");var subQ2=makeQuery(id+"F1.imprint","INTERSECT",VERTEX,{"derivedFrom":[subQ1,subQ0]});Q207=makeQuery(id+"F1.imprint","IMPRINT",FACE,{"disambiguationData":[TD([[makeQuery(id+"F1.imprint","IMPRINT",EDGE,{"disambiguationData":[TD([[subQ2,-1.0]])],"derivedFrom":subQ1}),-1.0]])]});}
            var Q208;
            {var subQ0=sQuery(id+"F1.wireOp",EDGE,"1122fb87-85ac-472b-868b-fc3012a12b32.3.0.0");var subQ1=sQuery(id+"F1.wireOp",EDGE,"a13d30e3-1256-45f2-88c4-17f94fdc27e3.0.4.0");var subQ2=makeQuery(id+"F1.imprint","INTERSECT",VERTEX,{"derivedFrom":[subQ1,subQ0]});Q208=makeQuery(id+"F1.imprint","IMPRINT",FACE,{"disambiguationData":[TD([[makeQuery(id+"F1.imprint","IMPRINT",EDGE,{"disambiguationData":[TD([[subQ2,-1.0]])],"derivedFrom":subQ1}),-1.0]])]});}
            var Q209;
            {var subQ0=sQuery(id+"F1.wireOp",EDGE,"1122fb87-85ac-472b-868b-fc3012a12b32.4.0.1");var subQ1=sQuery(id+"F1.wireOp",EDGE,"a13d30e3-1256-45f2-88c4-17f94fdc27e3.0.4.0");var subQ2=makeQuery(id+"F1.imprint","INTERSECT",VERTEX,{"derivedFrom":[subQ1,subQ0]});Q209=makeQuery(id+"F1.imprint","IMPRINT",FACE,{"disambiguationData":[TD([[makeQuery(id+"F1.imprint","IMPRINT",EDGE,{"disambiguationData":[TD([[subQ2,-1.0]])],"derivedFrom":subQ1}),-1.0]])]});}
            var Q210;
            {var subQ0=sQuery(id+"F1.wireOp",EDGE,"1122fb87-85ac-472b-868b-fc3012a12b32.4.0.0");var subQ1=sQuery(id+"F1.wireOp",EDGE,"a13d30e3-1256-45f2-88c4-17f94fdc27e3.0.4.0");var subQ2=makeQuery(id+"F1.imprint","INTERSECT",VERTEX,{"derivedFrom":[subQ1,subQ0]});Q210=makeQuery(id+"F1.imprint","IMPRINT",FACE,{"disambiguationData":[TD([[makeQuery(id+"F1.imprint","IMPRINT",EDGE,{"disambiguationData":[TD([[subQ2,-1.0]])],"derivedFrom":subQ1}),-1.0]])]});}
            var Q211;
            {var subQ0=sQuery(id+"F1.wireOp",EDGE,"1122fb87-85ac-472b-868b-fc3012a12b32.5.0.1");var subQ1=sQuery(id+"F1.wireOp",EDGE,"a13d30e3-1256-45f2-88c4-17f94fdc27e3.0.4.0");var subQ2=makeQuery(id+"F1.imprint","INTERSECT",VERTEX,{"derivedFrom":[subQ1,subQ0]});Q211=makeQuery(id+"F1.imprint","IMPRINT",FACE,{"disambiguationData":[TD([[makeQuery(id+"F1.imprint","IMPRINT",EDGE,{"disambiguationData":[TD([[subQ2,-1.0]])],"derivedFrom":subQ1}),-1.0]])]});}
            var Q212;
            {var subQ0=sQuery(id+"F1.wireOp",EDGE,"1122fb87-85ac-472b-868b-fc3012a12b32.5.0.0");var subQ1=sQuery(id+"F1.wireOp",EDGE,"a13d30e3-1256-45f2-88c4-17f94fdc27e3.0.4.0");var subQ2=makeQuery(id+"F1.imprint","INTERSECT",VERTEX,{"derivedFrom":[subQ1,subQ0]});Q212=makeQuery(id+"F1.imprint","IMPRINT",FACE,{"disambiguationData":[TD([[makeQuery(id+"F1.imprint","IMPRINT",EDGE,{"disambiguationData":[TD([[subQ2,-1.0]])],"derivedFrom":subQ1}),-1.0]])]});}
            var Q213;
            {var subQ0=sQuery(id+"F1.wireOp",EDGE,"1122fb87-85ac-472b-868b-fc3012a12b32.3.0.1");var subQ1=sQuery(id+"F1.wireOp",EDGE,"IqfzKEuX-Kduy-EBgq-JfLB-lxs091du6jRf");var subQ2=makeQuery(id+"F1.imprint","INTERSECT",VERTEX,{"derivedFrom":[subQ1,subQ0]});Q213=makeQuery(id+"F1.imprint","IMPRINT",FACE,{"disambiguationData":[TD([[makeQuery(id+"F1.imprint","IMPRINT",EDGE,{"disambiguationData":[TD([[subQ2,-1.0]])],"derivedFrom":subQ1}),-1.0]])]});}
            var Q214;
            {var subQ0=sQuery(id+"F1.wireOp",EDGE,"1122fb87-85ac-472b-868b-fc3012a12b32.3.0.1");var subQ1=sQuery(id+"F1.wireOp",EDGE,"a13d30e3-1256-45f2-88c4-17f94fdc27e3.0.2.1");var subQ2=makeQuery(id+"F1.imprint","INTERSECT",VERTEX,{"derivedFrom":[subQ1,subQ0]});Q214=makeQuery(id+"F1.imprint","IMPRINT",FACE,{"disambiguationData":[TD([[makeQuery(id+"F1.imprint","IMPRINT",EDGE,{"disambiguationData":[TD([[subQ2,-1.0]])],"derivedFrom":subQ1}),-1.0]])]});}
            var Q215;
            {var subQ0=sQuery(id+"F1.wireOp",EDGE,"1122fb87-85ac-472b-868b-fc3012a12b32.3.0.1");var subQ1=sQuery(id+"F1.wireOp",EDGE,"a13d30e3-1256-45f2-88c4-17f94fdc27e3.0.4.1");var subQ2=makeQuery(id+"F1.imprint","INTERSECT",VERTEX,{"derivedFrom":[subQ1,subQ0]});Q215=makeQuery(id+"F1.imprint","IMPRINT",FACE,{"disambiguationData":[TD([[makeQuery(id+"F1.imprint","IMPRINT",EDGE,{"disambiguationData":[TD([[subQ2,-1.0]])],"derivedFrom":subQ1}),-1.0]])]});}
            var Q216;
            {var subQ0=sQuery(id+"F1.wireOp",EDGE,"1122fb87-85ac-472b-868b-fc3012a12b32.3.0.1");var subQ1=sQuery(id+"F1.wireOp",EDGE,"6uq4eEBE-zqJi-hSKM-aljM-bMrpigbcLfnv");var subQ2=makeQuery(id+"F1.imprint","INTERSECT",VERTEX,{"derivedFrom":[subQ1,subQ0]});Q216=makeQuery(id+"F1.imprint","IMPRINT",FACE,{"disambiguationData":[TD([[makeQuery(id+"F1.imprint","IMPRINT",EDGE,{"disambiguationData":[TD([[subQ2,-1.0]])],"derivedFrom":subQ1}),1.0]])]});}
            var Q217;
            {var subQ0=sQuery(id+"F1.wireOp",EDGE,"1122fb87-85ac-472b-868b-fc3012a12b32.3.0.1");var subQ1=sQuery(id+"F1.wireOp",EDGE,"a13d30e3-1256-45f2-88c4-17f94fdc27e3.0.3.1");var subQ2=makeQuery(id+"F1.imprint","INTERSECT",VERTEX,{"derivedFrom":[subQ1,subQ0]});Q217=makeQuery(id+"F1.imprint","IMPRINT",FACE,{"disambiguationData":[TD([[makeQuery(id+"F1.imprint","IMPRINT",EDGE,{"disambiguationData":[TD([[subQ2,-1.0]])],"derivedFrom":subQ1}),-1.0]])]});}
            var Q218;
            {var subQ0=sQuery(id+"F1.wireOp",EDGE,"1122fb87-85ac-472b-868b-fc3012a12b32.3.0.1");var subQ1=sQuery(id+"F1.wireOp",EDGE,"a13d30e3-1256-45f2-88c4-17f94fdc27e3.0.1.1");var subQ2=makeQuery(id+"F1.imprint","INTERSECT",VERTEX,{"derivedFrom":[subQ1,subQ0]});Q218=makeQuery(id+"F1.imprint","IMPRINT",FACE,{"disambiguationData":[TD([[makeQuery(id+"F1.imprint","IMPRINT",EDGE,{"disambiguationData":[TD([[subQ2,-1.0]])],"derivedFrom":subQ1}),-1.0]])]});}
            var Q219;
            {var subQ0=sQuery(id+"F1.wireOp",EDGE,"1122fb87-85ac-472b-868b-fc3012a12b32.4.0.1");var subQ1=sQuery(id+"F1.wireOp",EDGE,"a13d30e3-1256-45f2-88c4-17f94fdc27e3.0.2.1");var subQ2=makeQuery(id+"F1.imprint","INTERSECT",VERTEX,{"derivedFrom":[subQ1,subQ0]});Q219=makeQuery(id+"F1.imprint","IMPRINT",FACE,{"disambiguationData":[TD([[makeQuery(id+"F1.imprint","IMPRINT",EDGE,{"disambiguationData":[TD([[subQ2,-1.0]])],"derivedFrom":subQ1}),-1.0]])]});}
            var Q220;
            {var subQ0=sQuery(id+"F1.wireOp",EDGE,"1122fb87-85ac-472b-868b-fc3012a12b32.4.0.1");var subQ1=sQuery(id+"F1.wireOp",EDGE,"IqfzKEuX-Kduy-EBgq-JfLB-lxs091du6jRf");var subQ2=makeQuery(id+"F1.imprint","INTERSECT",VERTEX,{"derivedFrom":[subQ1,subQ0]});Q220=makeQuery(id+"F1.imprint","IMPRINT",FACE,{"disambiguationData":[TD([[makeQuery(id+"F1.imprint","IMPRINT",EDGE,{"disambiguationData":[TD([[subQ2,-1.0]])],"derivedFrom":subQ1}),-1.0]])]});}
            var Q221;
            {var subQ0=sQuery(id+"F1.wireOp",EDGE,"1122fb87-85ac-472b-868b-fc3012a12b32.4.0.1");var subQ1=sQuery(id+"F1.wireOp",EDGE,"a13d30e3-1256-45f2-88c4-17f94fdc27e3.0.4.1");var subQ2=makeQuery(id+"F1.imprint","INTERSECT",VERTEX,{"derivedFrom":[subQ1,subQ0]});Q221=makeQuery(id+"F1.imprint","IMPRINT",FACE,{"disambiguationData":[TD([[makeQuery(id+"F1.imprint","IMPRINT",EDGE,{"disambiguationData":[TD([[subQ2,-1.0]])],"derivedFrom":subQ1}),-1.0]])]});}
            var Q222;
            {var subQ0=sQuery(id+"F1.wireOp",EDGE,"1122fb87-85ac-472b-868b-fc3012a12b32.4.0.1");var subQ1=sQuery(id+"F1.wireOp",EDGE,"6uq4eEBE-zqJi-hSKM-aljM-bMrpigbcLfnv");var subQ2=makeQuery(id+"F1.imprint","INTERSECT",VERTEX,{"derivedFrom":[subQ1,subQ0]});Q222=makeQuery(id+"F1.imprint","IMPRINT",FACE,{"disambiguationData":[TD([[makeQuery(id+"F1.imprint","IMPRINT",EDGE,{"disambiguationData":[TD([[subQ2,-1.0]])],"derivedFrom":subQ1}),1.0]])]});}
            var Q223;
            {var subQ0=sQuery(id+"F1.wireOp",EDGE,"1122fb87-85ac-472b-868b-fc3012a12b32.4.0.1");var subQ1=sQuery(id+"F1.wireOp",EDGE,"a13d30e3-1256-45f2-88c4-17f94fdc27e3.0.3.1");var subQ2=makeQuery(id+"F1.imprint","INTERSECT",VERTEX,{"derivedFrom":[subQ1,subQ0]});Q223=makeQuery(id+"F1.imprint","IMPRINT",FACE,{"disambiguationData":[TD([[makeQuery(id+"F1.imprint","IMPRINT",EDGE,{"disambiguationData":[TD([[subQ2,-1.0]])],"derivedFrom":subQ1}),-1.0]])]});}
            var Q224;
            {var subQ0=sQuery(id+"F1.wireOp",EDGE,"1122fb87-85ac-472b-868b-fc3012a12b32.4.0.1");var subQ1=sQuery(id+"F1.wireOp",EDGE,"a13d30e3-1256-45f2-88c4-17f94fdc27e3.0.1.1");var subQ2=makeQuery(id+"F1.imprint","INTERSECT",VERTEX,{"derivedFrom":[subQ1,subQ0]});Q224=makeQuery(id+"F1.imprint","IMPRINT",FACE,{"disambiguationData":[TD([[makeQuery(id+"F1.imprint","IMPRINT",EDGE,{"disambiguationData":[TD([[subQ2,-1.0]])],"derivedFrom":subQ1}),-1.0]])]});}
            var Q225;
            {var subQ0=sQuery(id+"F1.wireOp",EDGE,"1122fb87-85ac-472b-868b-fc3012a12b32.5.0.1");var subQ1=sQuery(id+"F1.wireOp",EDGE,"IqfzKEuX-Kduy-EBgq-JfLB-lxs091du6jRf");var subQ2=makeQuery(id+"F1.imprint","INTERSECT",VERTEX,{"derivedFrom":[subQ1,subQ0]});Q225=makeQuery(id+"F1.imprint","IMPRINT",FACE,{"disambiguationData":[TD([[makeQuery(id+"F1.imprint","IMPRINT",EDGE,{"disambiguationData":[TD([[subQ2,-1.0]])],"derivedFrom":subQ1}),-1.0]])]});}
            var Q226;
            {var subQ0=sQuery(id+"F1.wireOp",EDGE,"1122fb87-85ac-472b-868b-fc3012a12b32.5.0.1");var subQ1=sQuery(id+"F1.wireOp",EDGE,"a13d30e3-1256-45f2-88c4-17f94fdc27e3.0.4.1");var subQ2=makeQuery(id+"F1.imprint","INTERSECT",VERTEX,{"derivedFrom":[subQ1,subQ0]});Q226=makeQuery(id+"F1.imprint","IMPRINT",FACE,{"disambiguationData":[TD([[makeQuery(id+"F1.imprint","IMPRINT",EDGE,{"disambiguationData":[TD([[subQ2,-1.0]])],"derivedFrom":subQ1}),-1.0]])]});}
            var Q227;
            {var subQ0=sQuery(id+"F1.wireOp",EDGE,"1122fb87-85ac-472b-868b-fc3012a12b32.5.0.1");var subQ1=sQuery(id+"F1.wireOp",EDGE,"a13d30e3-1256-45f2-88c4-17f94fdc27e3.0.2.1");var subQ2=makeQuery(id+"F1.imprint","INTERSECT",VERTEX,{"derivedFrom":[subQ1,subQ0]});Q227=makeQuery(id+"F1.imprint","IMPRINT",FACE,{"disambiguationData":[TD([[makeQuery(id+"F1.imprint","IMPRINT",EDGE,{"disambiguationData":[TD([[subQ2,-1.0]])],"derivedFrom":subQ1}),-1.0]])]});}
            var Q228;
            {var subQ0=sQuery(id+"F1.wireOp",EDGE,"1122fb87-85ac-472b-868b-fc3012a12b32.5.0.1");var subQ1=sQuery(id+"F1.wireOp",EDGE,"6uq4eEBE-zqJi-hSKM-aljM-bMrpigbcLfnv");var subQ2=makeQuery(id+"F1.imprint","INTERSECT",VERTEX,{"derivedFrom":[subQ1,subQ0]});Q228=makeQuery(id+"F1.imprint","IMPRINT",FACE,{"disambiguationData":[TD([[makeQuery(id+"F1.imprint","IMPRINT",EDGE,{"disambiguationData":[TD([[subQ2,-1.0]])],"derivedFrom":subQ1}),1.0]])]});}
            var Q229;
            {var subQ0=sQuery(id+"F1.wireOp",EDGE,"1122fb87-85ac-472b-868b-fc3012a12b32.5.0.1");var subQ1=sQuery(id+"F1.wireOp",EDGE,"a13d30e3-1256-45f2-88c4-17f94fdc27e3.0.3.1");var subQ2=makeQuery(id+"F1.imprint","INTERSECT",VERTEX,{"derivedFrom":[subQ1,subQ0]});Q229=makeQuery(id+"F1.imprint","IMPRINT",FACE,{"disambiguationData":[TD([[makeQuery(id+"F1.imprint","IMPRINT",EDGE,{"disambiguationData":[TD([[subQ2,-1.0]])],"derivedFrom":subQ1}),-1.0]])]});}
            var Q230;
            {var subQ0=sQuery(id+"F1.wireOp",EDGE,"1122fb87-85ac-472b-868b-fc3012a12b32.5.0.1");var subQ1=sQuery(id+"F1.wireOp",EDGE,"a13d30e3-1256-45f2-88c4-17f94fdc27e3.0.1.1");var subQ2=makeQuery(id+"F1.imprint","INTERSECT",VERTEX,{"derivedFrom":[subQ1,subQ0]});Q230=makeQuery(id+"F1.imprint","IMPRINT",FACE,{"disambiguationData":[TD([[makeQuery(id+"F1.imprint","IMPRINT",EDGE,{"disambiguationData":[TD([[subQ2,-1.0]])],"derivedFrom":subQ1}),-1.0]])]});}
            var Q231;
            {var subQ0=sQuery(id+"F1.wireOp",EDGE,"1122fb87-85ac-472b-868b-fc3012a12b32.6.0.1");var subQ1=sQuery(id+"F1.wireOp",EDGE,"a13d30e3-1256-45f2-88c4-17f94fdc27e3.0.2.1");var subQ2=makeQuery(id+"F1.imprint","INTERSECT",VERTEX,{"derivedFrom":[subQ1,subQ0]});Q231=makeQuery(id+"F1.imprint","IMPRINT",FACE,{"disambiguationData":[TD([[makeQuery(id+"F1.imprint","IMPRINT",EDGE,{"disambiguationData":[TD([[subQ2,-1.0]])],"derivedFrom":subQ1}),-1.0]])]});}
            var Q232;
            {var subQ0=sQuery(id+"F1.wireOp",EDGE,"1122fb87-85ac-472b-868b-fc3012a12b32.6.0.1");var subQ1=sQuery(id+"F1.wireOp",EDGE,"a13d30e3-1256-45f2-88c4-17f94fdc27e3.0.4.1");var subQ2=makeQuery(id+"F1.imprint","INTERSECT",VERTEX,{"derivedFrom":[subQ1,subQ0]});Q232=makeQuery(id+"F1.imprint","IMPRINT",FACE,{"disambiguationData":[TD([[makeQuery(id+"F1.imprint","IMPRINT",EDGE,{"disambiguationData":[TD([[subQ2,-1.0]])],"derivedFrom":subQ1}),-1.0]])]});}
            var Q233;
            {var subQ0=sQuery(id+"F1.wireOp",EDGE,"1122fb87-85ac-472b-868b-fc3012a12b32.6.0.1");var subQ1=sQuery(id+"F1.wireOp",EDGE,"IqfzKEuX-Kduy-EBgq-JfLB-lxs091du6jRf");var subQ2=makeQuery(id+"F1.imprint","INTERSECT",VERTEX,{"derivedFrom":[subQ1,subQ0]});Q233=makeQuery(id+"F1.imprint","IMPRINT",FACE,{"disambiguationData":[TD([[makeQuery(id+"F1.imprint","IMPRINT",EDGE,{"disambiguationData":[TD([[subQ2,-1.0]])],"derivedFrom":subQ1}),-1.0]])]});}
            var Q234;
            {var subQ0=sQuery(id+"F1.wireOp",EDGE,"1122fb87-85ac-472b-868b-fc3012a12b32.6.0.1");var subQ1=sQuery(id+"F1.wireOp",EDGE,"a13d30e3-1256-45f2-88c4-17f94fdc27e3.0.3.1");var subQ2=makeQuery(id+"F1.imprint","INTERSECT",VERTEX,{"derivedFrom":[subQ1,subQ0]});Q234=makeQuery(id+"F1.imprint","IMPRINT",FACE,{"disambiguationData":[TD([[makeQuery(id+"F1.imprint","IMPRINT",EDGE,{"disambiguationData":[TD([[subQ2,-1.0]])],"derivedFrom":subQ1}),-1.0]])]});}
            var Q235;
            {var subQ0=sQuery(id+"F1.wireOp",EDGE,"1122fb87-85ac-472b-868b-fc3012a12b32.6.0.1");var subQ1=sQuery(id+"F1.wireOp",EDGE,"6uq4eEBE-zqJi-hSKM-aljM-bMrpigbcLfnv");var subQ2=makeQuery(id+"F1.imprint","INTERSECT",VERTEX,{"derivedFrom":[subQ1,subQ0]});Q235=makeQuery(id+"F1.imprint","IMPRINT",FACE,{"disambiguationData":[TD([[makeQuery(id+"F1.imprint","IMPRINT",EDGE,{"disambiguationData":[TD([[subQ2,-1.0]])],"derivedFrom":subQ1}),1.0]])]});}
            var Q236;
            {var subQ0=sQuery(id+"F1.wireOp",EDGE,"1122fb87-85ac-472b-868b-fc3012a12b32.6.0.1");var subQ1=sQuery(id+"F1.wireOp",EDGE,"a13d30e3-1256-45f2-88c4-17f94fdc27e3.0.1.1");var subQ2=makeQuery(id+"F1.imprint","INTERSECT",VERTEX,{"derivedFrom":[subQ1,subQ0]});Q236=makeQuery(id+"F1.imprint","IMPRINT",FACE,{"disambiguationData":[TD([[makeQuery(id+"F1.imprint","IMPRINT",EDGE,{"disambiguationData":[TD([[subQ2,-1.0]])],"derivedFrom":subQ1}),-1.0]])]});}
            var Q237;
            {var subQ0=sQuery(id+"F1.wireOp",EDGE,"1122fb87-85ac-472b-868b-fc3012a12b32.7.0.1");var subQ1=sQuery(id+"F1.wireOp",EDGE,"6uq4eEBE-zqJi-hSKM-aljM-bMrpigbcLfnv");var subQ2=makeQuery(id+"F1.imprint","INTERSECT",VERTEX,{"derivedFrom":[subQ1,subQ0]});Q237=makeQuery(id+"F1.imprint","IMPRINT",FACE,{"disambiguationData":[TD([[makeQuery(id+"F1.imprint","IMPRINT",EDGE,{"disambiguationData":[TD([[subQ2,-1.0]])],"derivedFrom":subQ1}),1.0]])]});}
            var Q238;
            {var subQ0=sQuery(id+"F1.wireOp",EDGE,"1122fb87-85ac-472b-868b-fc3012a12b32.7.0.1");var subQ1=sQuery(id+"F1.wireOp",EDGE,"a13d30e3-1256-45f2-88c4-17f94fdc27e3.0.4.1");var subQ2=makeQuery(id+"F1.imprint","INTERSECT",VERTEX,{"derivedFrom":[subQ1,subQ0]});Q238=makeQuery(id+"F1.imprint","IMPRINT",FACE,{"disambiguationData":[TD([[makeQuery(id+"F1.imprint","IMPRINT",EDGE,{"disambiguationData":[TD([[subQ2,-1.0]])],"derivedFrom":subQ1}),-1.0]])]});}
            var Q239;
            {var subQ0=sQuery(id+"F1.wireOp",EDGE,"1122fb87-85ac-472b-868b-fc3012a12b32.7.0.1");var subQ1=sQuery(id+"F1.wireOp",EDGE,"a13d30e3-1256-45f2-88c4-17f94fdc27e3.0.2.1");var subQ2=makeQuery(id+"F1.imprint","INTERSECT",VERTEX,{"derivedFrom":[subQ1,subQ0]});Q239=makeQuery(id+"F1.imprint","IMPRINT",FACE,{"disambiguationData":[TD([[makeQuery(id+"F1.imprint","IMPRINT",EDGE,{"disambiguationData":[TD([[subQ2,-1.0]])],"derivedFrom":subQ1}),-1.0]])]});}
            var Q240;
            {var subQ0=sQuery(id+"F1.wireOp",EDGE,"1122fb87-85ac-472b-868b-fc3012a12b32.7.0.1");var subQ1=sQuery(id+"F1.wireOp",EDGE,"IqfzKEuX-Kduy-EBgq-JfLB-lxs091du6jRf");var subQ2=makeQuery(id+"F1.imprint","INTERSECT",VERTEX,{"derivedFrom":[subQ1,subQ0]});Q240=makeQuery(id+"F1.imprint","IMPRINT",FACE,{"disambiguationData":[TD([[makeQuery(id+"F1.imprint","IMPRINT",EDGE,{"disambiguationData":[TD([[subQ2,-1.0]])],"derivedFrom":subQ1}),-1.0]])]});}
            var Q241;
            {var subQ0=sQuery(id+"F1.wireOp",EDGE,"1122fb87-85ac-472b-868b-fc3012a12b32.7.0.1");var subQ1=sQuery(id+"F1.wireOp",EDGE,"a13d30e3-1256-45f2-88c4-17f94fdc27e3.0.3.1");var subQ2=makeQuery(id+"F1.imprint","INTERSECT",VERTEX,{"derivedFrom":[subQ1,subQ0]});Q241=makeQuery(id+"F1.imprint","IMPRINT",FACE,{"disambiguationData":[TD([[makeQuery(id+"F1.imprint","IMPRINT",EDGE,{"disambiguationData":[TD([[subQ2,-1.0]])],"derivedFrom":subQ1}),-1.0]])]});}
            var Q242;
            {var subQ0=sQuery(id+"F1.wireOp",EDGE,"1122fb87-85ac-472b-868b-fc3012a12b32.7.0.1");var subQ1=sQuery(id+"F1.wireOp",EDGE,"a13d30e3-1256-45f2-88c4-17f94fdc27e3.0.1.1");var subQ2=makeQuery(id+"F1.imprint","INTERSECT",VERTEX,{"derivedFrom":[subQ1,subQ0]});Q242=makeQuery(id+"F1.imprint","IMPRINT",FACE,{"disambiguationData":[TD([[makeQuery(id+"F1.imprint","IMPRINT",EDGE,{"disambiguationData":[TD([[subQ2,-1.0]])],"derivedFrom":subQ1}),-1.0]])]});}
            var Q243;
            {var subQ3=sQuery(id+"F1.wireOp",EDGE,"lT3caQUp-7fkk-oJsE-IIBZ-dWKZlLfLGzlh");Q243=makeQuery(id+"F1.imprint","IMPRINT",FACE,{"disambiguationData":[TD([[makeQuery(id+"F1.imprint","IMPRINT",EDGE,{"derivedFrom":subQ3}),1.0]])]});}
            var Q244;
            {var subQ0=sQuery(id+"F1.wireOp",EDGE,"482af6a0-1903-4b05-83aa-6ef149d7ce10.1");Q244=makeQuery(id+"F1.imprint","IMPRINT",FACE,{"disambiguationData":[TD([[makeQuery(id+"F1.imprint","IMPRINT",EDGE,{"derivedFrom":subQ0}),1.0]])]});}
            var Q245;
            {var subQ9=sQuery(id+"F1.wireOp",EDGE,"C4clxQaj-lqoT-T4Zx-6NgX-D8VWOoOf61GK");Q245=makeQuery(id+"F1.imprint","IMPRINT",FACE,{"disambiguationData":[TD([[makeQuery(id+"F1.imprint","IMPRINT",EDGE,{"derivedFrom":subQ9}),1.0]])]});}
            var Q246;
            {var subQ13=sQuery(id+"F1.wireOp",EDGE,"O6UPYSY0-emfk-z3gh-tUcF-rXbmS0BsRFMJ.bottom");Q246=makeQuery(id+"F1.imprint","IMPRINT",FACE,{"disambiguationData":[TD([[makeQuery(id+"F1.imprint","IMPRINT",EDGE,{"derivedFrom":subQ13}),1.0]])]});}
            var Q247;
            {var subQ10=sQuery(id+"F1.wireOp",EDGE,"KMUZViEf-TnLA-kmT8-466D-RJTt4dFkFstP.bottom");Q247=makeQuery(id+"F1.imprint","IMPRINT",FACE,{"disambiguationData":[TD([[makeQuery(id+"F1.imprint","IMPRINT",EDGE,{"derivedFrom":subQ10}),-1.0]])]});}
            var Q248;
            {var subQ11=sQuery(id+"F1.wireOp",EDGE,"59e32a3a-5665-4a53-9582-045fd37ad6320.MirrorCS");Q248=makeQuery(id+"F1.imprint","IMPRINT",FACE,{"disambiguationData":[TD([[makeQuery(id+"F1.imprint","IMPRINT",EDGE,{"derivedFrom":subQ11}),1.0]])]});}
            var Q249;
            {var subQ0=sQuery(id+"F1.wireOp",EDGE,"J55gWL4n-IN0f-33U7-3SXX-em1Zf4m61p5m");Q249=makeQuery(id+"F1.imprint","IMPRINT",FACE,{"disambiguationData":[TD([[makeQuery(id+"F1.imprint","IMPRINT",EDGE,{"derivedFrom":subQ0}),-1.0]])]});}
            var Q250;
            {var subQ0=sQuery(id+"F1.wireOp",EDGE,"8f29c0e0-161e-4b79-b4d1-194ac79dd8834.MirrorCS");Q250=makeQuery(id+"F1.imprint","IMPRINT",FACE,{"disambiguationData":[TD([[makeQuery(id+"F1.imprint","IMPRINT",EDGE,{"derivedFrom":subQ0}),-1.0]])]});}
            var Q251;
            {var subQ0=sQuery(id+"F1.wireOp",EDGE,"8f29c0e0-161e-4b79-b4d1-194ac79dd8832.MirrorCS");Q251=makeQuery(id+"F1.imprint","IMPRINT",FACE,{"disambiguationData":[TD([[makeQuery(id+"F1.imprint","IMPRINT",EDGE,{"derivedFrom":subQ0}),-1.0]])]});}
            var Q252;
            {var subQ0=sQuery(id+"F1.wireOp",EDGE,"p9qtpjec-kYh1-UPlk-B21C-cUk12FXXUcXK");Q252=makeQuery(id+"F1.imprint","IMPRINT",FACE,{"disambiguationData":[TD([[makeQuery(id+"F1.imprint","IMPRINT",EDGE,{"derivedFrom":subQ0}),-1.0]])]});}
            var Q253;
            {var subQ5=sQuery(id+"F1.wireOp",EDGE,"E193");Q253=makeQuery(id+"F1.imprint","IMPRINT",FACE,{"disambiguationData":[TD([[makeQuery(id+"F1.imprint","IMPRINT",EDGE,{"derivedFrom":subQ5}),-1.0]])]});}
            var Q254;
            {var subQ0=sQuery(id+"F1.wireOp",EDGE,"E200.MirrorCS");Q254=makeQuery(id+"F1.imprint","IMPRINT",FACE,{"disambiguationData":[TD([[makeQuery(id+"F1.imprint","IMPRINT",EDGE,{"derivedFrom":subQ0}),-1.0]])]});}
            var Q255;
            {var subQ0=sQuery(id+"F1.wireOp",EDGE,"E191");Q255=makeQuery(id+"F1.imprint","IMPRINT",FACE,{"disambiguationData":[TD([[makeQuery(id+"F1.imprint","IMPRINT",EDGE,{"derivedFrom":subQ0}),1.0]])]});}
            var Q256;
            {var subQ0=sQuery(id+"F1.wireOp",EDGE,"E188");Q256=makeQuery(id+"F1.imprint","IMPRINT",FACE,{"disambiguationData":[TD([[makeQuery(id+"F1.imprint","IMPRINT",EDGE,{"derivedFrom":subQ0}),1.0]])]});}
            var Q257;
            {var subQ0=sQuery(id+"F1.wireOp",EDGE,"E203.MirrorCS");Q257=makeQuery(id+"F1.imprint","IMPRINT",FACE,{"disambiguationData":[TD([[makeQuery(id+"F1.imprint","IMPRINT",EDGE,{"derivedFrom":subQ0}),-1.0]])]});}
            var Q258;
            {var subQ6=sQuery(id+"F1.wireOp",EDGE,"E145");Q258=makeQuery(id+"F1.imprint","IMPRINT",FACE,{"disambiguationData":[TD([[makeQuery(id+"F1.imprint","IMPRINT",EDGE,{"derivedFrom":subQ6}),-1.0]])]});}
            var Q259;
            {var subQ0=sQuery(id+"F1.wireOp",EDGE,"E142.bottom");Q259=makeQuery(id+"F1.imprint","IMPRINT",FACE,{"disambiguationData":[TD([[makeQuery(id+"F1.imprint","IMPRINT",EDGE,{"derivedFrom":subQ0}),1.0]])]});}
            var Q260;
            {var subQ0=sQuery(id+"F1.wireOp",EDGE,"E143.bottom");Q260=makeQuery(id+"F1.imprint","IMPRINT",FACE,{"disambiguationData":[TD([[makeQuery(id+"F1.imprint","IMPRINT",EDGE,{"derivedFrom":subQ0}),1.0]])]});}
            var Q261;
            Q261=makeQuery(id+"F1.imprint","IMPRINT",FACE,{"disambiguationData":[TD([[makeQuery(id+"F1.imprint","IMPRINT",EDGE,{"derivedFrom":sQuery(id+"F1.wireOp",EDGE,"E215.MirrorCS")}),-1.0]])]});
            var Q262;
            {var subQ3=sQuery(id+"F1.wireOp",EDGE,"E261");Q262=makeQuery(id+"F1.imprint","IMPRINT",FACE,{"disambiguationData":[TD([[makeQuery(id+"F1.imprint","IMPRINT",EDGE,{"derivedFrom":subQ3}),-1.0]])]});}
            var Q263;
            {var subQ5=sQuery(id+"F1.wireOp",EDGE,"E266.top");Q263=makeQuery(id+"F1.imprint","IMPRINT",FACE,{"disambiguationData":[TD([[makeQuery(id+"F1.imprint","IMPRINT",EDGE,{"derivedFrom":subQ5}),-1.0]])]});}
            var Q264;
            {var subQ5=sQuery(id+"F1.wireOp",EDGE,"E266.bottom");Q264=makeQuery(id+"F1.imprint","IMPRINT",FACE,{"disambiguationData":[TD([[makeQuery(id+"F1.imprint","IMPRINT",EDGE,{"derivedFrom":subQ5}),1.0]])]});}
            var Q265;
            {var subQ3=sQuery(id+"F1.wireOp",EDGE,"E263");Q265=makeQuery(id+"F1.imprint","IMPRINT",FACE,{"disambiguationData":[TD([[makeQuery(id+"F1.imprint","IMPRINT",EDGE,{"derivedFrom":subQ3}),-1.0]])]});}
            extrude(context, id + "F2", {"entities" : qUnion([Q0, Q1, Q2, Q3, Q4, Q5, Q6, Q7, Q8, Q9, Q10, Q11, Q12, Q13, Q14, Q15, Q16, Q17, Q18, Q19, Q20, Q21, Q22, Q23, Q24, Q25, Q26, Q27, Q28, Q29, Q30, Q31, Q32, Q33, Q34, Q35, Q36, Q37, Q38, Q39, Q40, Q41, Q42, Q43, Q44, Q45, Q46, Q47, Q48, Q49, Q50, Q51, Q52, Q53, Q54, Q55, Q56, Q57, Q58, Q59, Q60, Q61, Q62, Q63, Q64, Q65, Q66, Q67, Q68, Q69, Q70, Q71, Q72, Q73, Q74, Q75, Q76, Q77, Q78, Q79, Q80, Q81, Q82, Q83, Q84, Q85, Q86, Q87, Q88, Q89, Q90, Q91, Q92, Q93, Q94, Q95, Q96, Q97, Q98, Q99, Q100, Q101, Q102, Q103, Q104, Q105, Q106, Q107, Q108, Q109, Q110, Q111, Q112, Q113, Q114, Q115, Q116, Q117, Q118, Q119, Q120, Q121, Q122, Q123, Q124, Q125, Q126, Q127, Q128, Q129, Q130, Q131, Q132, Q133, Q134, Q135, Q136, Q137, Q138, Q139, Q140, Q141, Q142, Q143, Q144, Q145, Q146, Q147, Q148, Q149, Q150, Q151, Q152, Q153, Q154, Q155, Q156, Q157, Q158, Q159, Q160, Q161, Q162, Q163, Q164, Q165, Q166, Q167, Q168, Q169, Q170, Q171, Q172, Q173, Q174, Q175, Q176, Q177, Q178, Q179, Q180, Q181, Q182, Q183, Q184, Q185, Q186, Q187, Q188, Q189, Q190, Q191, Q192, Q193, Q194, Q195, Q196, Q197, Q198, Q199, Q200, Q201, Q202, Q203, Q204, Q205, Q206, Q207, Q208, Q209, Q210, Q211, Q212, Q213, Q214, Q215, Q216, Q217, Q218, Q219, Q220, Q221, Q222, Q223, Q224, Q225, Q226, Q227, Q228, Q229, Q230, Q231, Q232, Q233, Q234, Q235, Q236, Q237, Q238, Q239, Q240, Q241, Q242, Q243, Q244, Q245, Q246, Q247, Q248, Q249, Q250, Q251, Q252, Q253, Q254, Q255, Q256, Q257, Q258, Q259, Q260, Q261, Q262, Q263, Q264, Q265]), "depth" : (getVariable(context, 'ply34')) * mm, "offsetDistance" : 25.4 * mm});
        }
    });
